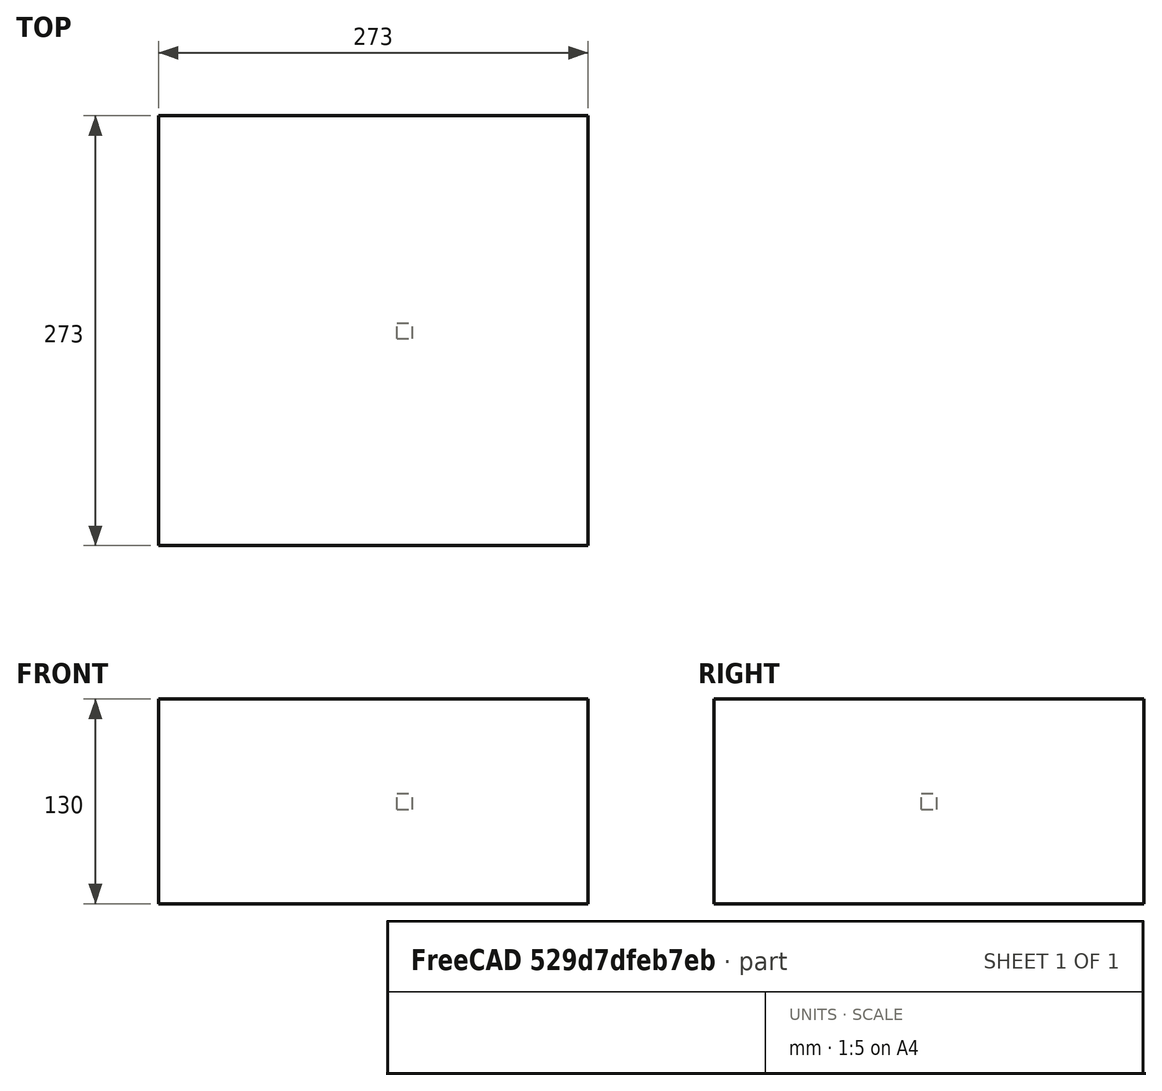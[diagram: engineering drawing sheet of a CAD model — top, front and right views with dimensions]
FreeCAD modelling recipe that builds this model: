
FCSTD DOCUMENT  (FreeCAD 0.20RUnknown)
Label: polarArray-3b
License: All rights reserved
LicenseURL: http://en.wikipedia.org/wiki/All_rights_reserved
objects: App::DocumentObjectGroupPython×1251, Part::FeaturePython×3, App::Part×3
note: 2 computed .brp shape members not serialized (recipe doc carries the construction recipe); baked Part::Feature solids carry a one-line shape summary decoded from their .brp

FEATURE [App::DocumentObjectGroupPython] HALFPI  # scripted group (container) (typed FeaturePython)
  name = HALFPI
  value = pi/2.
FEATURE [App::DocumentObjectGroupPython] PI  # scripted group (container) (typed FeaturePython)
  name = PI
  value = 1.*pi
FEATURE [App::DocumentObjectGroupPython] TWOPI  # scripted group (container) (typed FeaturePython)
  name = TWOPI
  value = 2.*pi
FEATURE [App::DocumentObjectGroupPython] Constants  # scripted group (container) (typed FeaturePython)
  Group = -> [HALFPI,PI,TWOPI]
FEATURE [App::DocumentObjectGroupPython] Variables  # scripted group (container) (typed FeaturePython)
FEATURE [App::DocumentObjectGroupPython] Quantities  # scripted group (container) (typed FeaturePython)
FEATURE [App::DocumentObjectGroupPython] Isotopes  # scripted group (container) (typed FeaturePython)
FEATURE [App::DocumentObjectGroupPython] Elements  # scripted group (container) (typed FeaturePython)
FEATURE [App::DocumentObjectGroupPython] Matrix  # scripted group (container) (typed FeaturePython)
FEATURE [App::DocumentObjectGroupPython] Surfaces  # scripted group (container) (typed FeaturePython)
FEATURE [App::DocumentObjectGroupPython] Opticals  # scripted group (container) (typed FeaturePython)
  Group = -> [Matrix,Surfaces]
FEATURE [App::DocumentObjectGroupPython] G4Isotopes  # scripted group (container) (typed FeaturePython)
FEATURE [App::DocumentObjectGroupPython] H_element  # scripted group (container) (typed FeaturePython)
  Z = 1
  atom_value = 1.008
  formula = H
  name = H_element
FEATURE [App::DocumentObjectGroupPython] He_element  # scripted group (container) (typed FeaturePython)
  Z = 2
  atom_value = 4.0026
  formula = He
  name = He_element
FEATURE [App::DocumentObjectGroupPython] Li_element  # scripted group (container) (typed FeaturePython)
  Z = 3
  atom_value = 6.94
  formula = Li
  name = Li_element
FEATURE [App::DocumentObjectGroupPython] Be_element  # scripted group (container) (typed FeaturePython)
  Z = 4
  atom_value = 9.01218
  formula = Be
  name = Be_element
FEATURE [App::DocumentObjectGroupPython] B_element  # scripted group (container) (typed FeaturePython)
  Z = 5
  atom_value = 10.81
  formula = B
  name = B_element
FEATURE [App::DocumentObjectGroupPython] C_element  # scripted group (container) (typed FeaturePython)
  Z = 6
  atom_value = 12.011
  formula = C
  name = C_element
FEATURE [App::DocumentObjectGroupPython] N_element  # scripted group (container) (typed FeaturePython)
  Z = 7
  atom_value = 14.007
  formula = N
  name = N_element
FEATURE [App::DocumentObjectGroupPython] O_element  # scripted group (container) (typed FeaturePython)
  Z = 8
  atom_value = 15.999
  formula = O
  name = O_element
FEATURE [App::DocumentObjectGroupPython] F_element  # scripted group (container) (typed FeaturePython)
  Z = 9
  atom_value = 18.9984
  formula = F
  name = F_element
FEATURE [App::DocumentObjectGroupPython] Ne_element  # scripted group (container) (typed FeaturePython)
  Z = 10
  atom_value = 20.1797
  formula = Ne
  name = Ne_element
FEATURE [App::DocumentObjectGroupPython] Na_element  # scripted group (container) (typed FeaturePython)
  Z = 11
  atom_value = 22.9898
  formula = Na
  name = Na_element
FEATURE [App::DocumentObjectGroupPython] Mg_element  # scripted group (container) (typed FeaturePython)
  Z = 12
  atom_value = 24.305
  formula = Mg
  name = Mg_element
FEATURE [App::DocumentObjectGroupPython] Al_element  # scripted group (container) (typed FeaturePython)
  Z = 13
  atom_value = 26.9815
  formula = Al
  name = Al_element
FEATURE [App::DocumentObjectGroupPython] Si_element  # scripted group (container) (typed FeaturePython)
  Z = 14
  atom_value = 28.085
  formula = Si
  name = Si_element
FEATURE [App::DocumentObjectGroupPython] P_element  # scripted group (container) (typed FeaturePython)
  Z = 15
  atom_value = 30.9738
  formula = P
  name = P_element
FEATURE [App::DocumentObjectGroupPython] S_element  # scripted group (container) (typed FeaturePython)
  Z = 16
  atom_value = 32.06
  formula = S
  name = S_element
FEATURE [App::DocumentObjectGroupPython] Cl_element  # scripted group (container) (typed FeaturePython)
  Z = 17
  atom_value = 35.45
  formula = Cl
  name = Cl_element
FEATURE [App::DocumentObjectGroupPython] Ar_element  # scripted group (container) (typed FeaturePython)
  Z = 18
  atom_value = 39.95
  formula = Ar
  name = Ar_element
FEATURE [App::DocumentObjectGroupPython] K_element  # scripted group (container) (typed FeaturePython)
  Z = 19
  atom_value = 39.0983
  formula = K
  name = K_element
FEATURE [App::DocumentObjectGroupPython] Ca_element  # scripted group (container) (typed FeaturePython)
  Z = 20
  atom_value = 40.078
  formula = Ca
  name = Ca_element
FEATURE [App::DocumentObjectGroupPython] Sc_element  # scripted group (container) (typed FeaturePython)
  Z = 21
  atom_value = 44.9559
  formula = Sc
  name = Sc_element
FEATURE [App::DocumentObjectGroupPython] Ti_element  # scripted group (container) (typed FeaturePython)
  Z = 22
  atom_value = 47.867
  formula = Ti
  name = Ti_element
FEATURE [App::DocumentObjectGroupPython] V_element  # scripted group (container) (typed FeaturePython)
  Z = 23
  atom_value = 50.9415
  formula = V
  name = V_element
FEATURE [App::DocumentObjectGroupPython] Cr_element  # scripted group (container) (typed FeaturePython)
  Z = 24
  atom_value = 51.9961
  formula = Cr
  name = Cr_element
FEATURE [App::DocumentObjectGroupPython] Mn_element  # scripted group (container) (typed FeaturePython)
  Z = 25
  atom_value = 54.938
  formula = Mn
  name = Mn_element
FEATURE [App::DocumentObjectGroupPython] Fe_element  # scripted group (container) (typed FeaturePython)
  Z = 26
  atom_value = 55.845
  formula = Fe
  name = Fe_element
FEATURE [App::DocumentObjectGroupPython] Co_element  # scripted group (container) (typed FeaturePython)
  Z = 27
  atom_value = 58.9332
  formula = Co
  name = Co_element
FEATURE [App::DocumentObjectGroupPython] Ni_element  # scripted group (container) (typed FeaturePython)
  Z = 28
  atom_value = 58.6934
  formula = Ni
  name = Ni_element
FEATURE [App::DocumentObjectGroupPython] Cu_element  # scripted group (container) (typed FeaturePython)
  Z = 29
  atom_value = 63.546
  formula = Cu
  name = Cu_element
FEATURE [App::DocumentObjectGroupPython] Zn_element  # scripted group (container) (typed FeaturePython)
  Z = 30
  atom_value = 65.38
  formula = Zn
  name = Zn_element
FEATURE [App::DocumentObjectGroupPython] Ga_element  # scripted group (container) (typed FeaturePython)
  Z = 31
  atom_value = 69.723
  formula = Ga
  name = Ga_element
FEATURE [App::DocumentObjectGroupPython] Ge_element  # scripted group (container) (typed FeaturePython)
  Z = 32
  atom_value = 72.63
  formula = Ge
  name = Ge_element
FEATURE [App::DocumentObjectGroupPython] As_element  # scripted group (container) (typed FeaturePython)
  Z = 33
  atom_value = 74.9216
  formula = As
  name = As_element
FEATURE [App::DocumentObjectGroupPython] Se_element  # scripted group (container) (typed FeaturePython)
  Z = 34
  atom_value = 78.971
  formula = Se
  name = Se_element
FEATURE [App::DocumentObjectGroupPython] Br_element  # scripted group (container) (typed FeaturePython)
  Z = 35
  atom_value = 79.904
  formula = Br
  name = Br_element
FEATURE [App::DocumentObjectGroupPython] Kr_element  # scripted group (container) (typed FeaturePython)
  Z = 36
  atom_value = 83.798
  formula = Kr
  name = Kr_element
FEATURE [App::DocumentObjectGroupPython] Rb_element  # scripted group (container) (typed FeaturePython)
  Z = 37
  atom_value = 85.4678
  formula = Rb
  name = Rb_element
FEATURE [App::DocumentObjectGroupPython] Sr_element  # scripted group (container) (typed FeaturePython)
  Z = 38
  atom_value = 87.62
  formula = Sr
  name = Sr_element
FEATURE [App::DocumentObjectGroupPython] Y_element  # scripted group (container) (typed FeaturePython)
  Z = 39
  atom_value = 88.9058
  formula = Y
  name = Y_element
FEATURE [App::DocumentObjectGroupPython] Zr_element  # scripted group (container) (typed FeaturePython)
  Z = 40
  atom_value = 91.224
  formula = Zr
  name = Zr_element
FEATURE [App::DocumentObjectGroupPython] Nb_element  # scripted group (container) (typed FeaturePython)
  Z = 41
  atom_value = 92.9064
  formula = Nb
  name = Nb_element
FEATURE [App::DocumentObjectGroupPython] Mo_element  # scripted group (container) (typed FeaturePython)
  Z = 42
  atom_value = 95.95
  formula = Mo
  name = Mo_element
FEATURE [App::DocumentObjectGroupPython] Tc_element  # scripted group (container) (typed FeaturePython)
  Z = 43
  atom_value = 97
  formula = Tc
  name = Tc_element
FEATURE [App::DocumentObjectGroupPython] Ru_element  # scripted group (container) (typed FeaturePython)
  Z = 44
  atom_value = 101.07
  formula = Ru
  name = Ru_element
FEATURE [App::DocumentObjectGroupPython] Rh_element  # scripted group (container) (typed FeaturePython)
  Z = 45
  atom_value = 102.905
  formula = Rh
  name = Rh_element
FEATURE [App::DocumentObjectGroupPython] Pd_element  # scripted group (container) (typed FeaturePython)
  Z = 46
  atom_value = 106.42
  formula = Pd
  name = Pd_element
FEATURE [App::DocumentObjectGroupPython] Ag_element  # scripted group (container) (typed FeaturePython)
  Z = 47
  atom_value = 107.868
  formula = Ag
  name = Ag_element
FEATURE [App::DocumentObjectGroupPython] Cd_element  # scripted group (container) (typed FeaturePython)
  Z = 48
  atom_value = 112.414
  formula = Cd
  name = Cd_element
FEATURE [App::DocumentObjectGroupPython] In_element  # scripted group (container) (typed FeaturePython)
  Z = 49
  atom_value = 114.818
  formula = In
  name = In_element
FEATURE [App::DocumentObjectGroupPython] Sn_element  # scripted group (container) (typed FeaturePython)
  Z = 50
  atom_value = 118.71
  formula = Sn
  name = Sn_element
FEATURE [App::DocumentObjectGroupPython] Sb_element  # scripted group (container) (typed FeaturePython)
  Z = 51
  atom_value = 121.76
  formula = Sb
  name = Sb_element
FEATURE [App::DocumentObjectGroupPython] Te_element  # scripted group (container) (typed FeaturePython)
  Z = 52
  atom_value = 127.6
  formula = Te
  name = Te_element
FEATURE [App::DocumentObjectGroupPython] I_element  # scripted group (container) (typed FeaturePython)
  Z = 53
  atom_value = 126.904
  formula = I
  name = I_element
FEATURE [App::DocumentObjectGroupPython] Xe_element  # scripted group (container) (typed FeaturePython)
  Z = 54
  atom_value = 131.293
  formula = Xe
  name = Xe_element
FEATURE [App::DocumentObjectGroupPython] Cs_element  # scripted group (container) (typed FeaturePython)
  Z = 55
  atom_value = 132.905
  formula = Cs
  name = Cs_element
FEATURE [App::DocumentObjectGroupPython] Ba_element  # scripted group (container) (typed FeaturePython)
  Z = 56
  atom_value = 137.327
  formula = Ba
  name = Ba_element
FEATURE [App::DocumentObjectGroupPython] La_element  # scripted group (container) (typed FeaturePython)
  Z = 57
  atom_value = 138.905
  formula = La
  name = La_element
FEATURE [App::DocumentObjectGroupPython] Ce_element  # scripted group (container) (typed FeaturePython)
  Z = 58
  atom_value = 140.116
  formula = Ce
  name = Ce_element
FEATURE [App::DocumentObjectGroupPython] Pr_element  # scripted group (container) (typed FeaturePython)
  Z = 59
  atom_value = 140.908
  formula = Pr
  name = Pr_element
FEATURE [App::DocumentObjectGroupPython] Nd_element  # scripted group (container) (typed FeaturePython)
  Z = 60
  atom_value = 144.242
  formula = Nd
  name = Nd_element
FEATURE [App::DocumentObjectGroupPython] Pm_element  # scripted group (container) (typed FeaturePython)
  Z = 61
  atom_value = 145
  formula = Pm
  name = Pm_element
FEATURE [App::DocumentObjectGroupPython] Sm_element  # scripted group (container) (typed FeaturePython)
  Z = 62
  atom_value = 150.36
  formula = Sm
  name = Sm_element
FEATURE [App::DocumentObjectGroupPython] Eu_element  # scripted group (container) (typed FeaturePython)
  Z = 63
  atom_value = 151.964
  formula = Eu
  name = Eu_element
FEATURE [App::DocumentObjectGroupPython] Gd_element  # scripted group (container) (typed FeaturePython)
  Z = 64
  atom_value = 157.25
  formula = Gd
  name = Gd_element
FEATURE [App::DocumentObjectGroupPython] Tb_element  # scripted group (container) (typed FeaturePython)
  Z = 65
  atom_value = 158.925
  formula = Tb
  name = Tb_element
FEATURE [App::DocumentObjectGroupPython] Dy_element  # scripted group (container) (typed FeaturePython)
  Z = 66
  atom_value = 162.5
  formula = Dy
  name = Dy_element
FEATURE [App::DocumentObjectGroupPython] Ho_element  # scripted group (container) (typed FeaturePython)
  Z = 67
  atom_value = 164.93
  formula = Ho
  name = Ho_element
FEATURE [App::DocumentObjectGroupPython] Er_element  # scripted group (container) (typed FeaturePython)
  Z = 68
  atom_value = 167.259
  formula = Er
  name = Er_element
FEATURE [App::DocumentObjectGroupPython] Tm_element  # scripted group (container) (typed FeaturePython)
  Z = 69
  atom_value = 168.934
  formula = Tm
  name = Tm_element
FEATURE [App::DocumentObjectGroupPython] Yb_element  # scripted group (container) (typed FeaturePython)
  Z = 70
  atom_value = 173.045
  formula = Yb
  name = Yb_element
FEATURE [App::DocumentObjectGroupPython] Lu_element  # scripted group (container) (typed FeaturePython)
  Z = 71
  atom_value = 174.967
  formula = Lu
  name = Lu_element
FEATURE [App::DocumentObjectGroupPython] Hf_element  # scripted group (container) (typed FeaturePython)
  Z = 72
  atom_value = 178.49
  formula = Hf
  name = Hf_element
FEATURE [App::DocumentObjectGroupPython] Ta_element  # scripted group (container) (typed FeaturePython)
  Z = 73
  atom_value = 180.948
  formula = Ta
  name = Ta_element
FEATURE [App::DocumentObjectGroupPython] W_element  # scripted group (container) (typed FeaturePython)
  Z = 74
  atom_value = 183.84
  formula = W
  name = W_element
FEATURE [App::DocumentObjectGroupPython] Re_element  # scripted group (container) (typed FeaturePython)
  Z = 75
  atom_value = 186.207
  formula = Re
  name = Re_element
FEATURE [App::DocumentObjectGroupPython] Os_element  # scripted group (container) (typed FeaturePython)
  Z = 76
  atom_value = 190.23
  formula = Os
  name = Os_element
FEATURE [App::DocumentObjectGroupPython] Ir_element  # scripted group (container) (typed FeaturePython)
  Z = 77
  atom_value = 192.217
  formula = Ir
  name = Ir_element
FEATURE [App::DocumentObjectGroupPython] Pt_element  # scripted group (container) (typed FeaturePython)
  Z = 78
  atom_value = 195.084
  formula = Pt
  name = Pt_element
FEATURE [App::DocumentObjectGroupPython] Au_element  # scripted group (container) (typed FeaturePython)
  Z = 79
  atom_value = 196.967
  formula = Au
  name = Au_element
FEATURE [App::DocumentObjectGroupPython] Hg_element  # scripted group (container) (typed FeaturePython)
  Z = 80
  atom_value = 200.592
  formula = Hg
  name = Hg_element
FEATURE [App::DocumentObjectGroupPython] Tl_element  # scripted group (container) (typed FeaturePython)
  Z = 81
  atom_value = 204.38
  formula = Tl
  name = Tl_element
FEATURE [App::DocumentObjectGroupPython] Pb_element  # scripted group (container) (typed FeaturePython)
  Z = 82
  atom_value = 207.2
  formula = Pb
  name = Pb_element
FEATURE [App::DocumentObjectGroupPython] Bi_element  # scripted group (container) (typed FeaturePython)
  Z = 83
  atom_value = 208.98
  formula = Bi
  name = Bi_element
FEATURE [App::DocumentObjectGroupPython] Po_element  # scripted group (container) (typed FeaturePython)
  Z = 84
  atom_value = 209
  formula = Po
  name = Po_element
FEATURE [App::DocumentObjectGroupPython] At_element  # scripted group (container) (typed FeaturePython)
  Z = 85
  atom_value = 210
  formula = At
  name = At_element
FEATURE [App::DocumentObjectGroupPython] Rn_element  # scripted group (container) (typed FeaturePython)
  Z = 86
  atom_value = 222
  formula = Rn
  name = Rn_element
FEATURE [App::DocumentObjectGroupPython] Fr_element  # scripted group (container) (typed FeaturePython)
  Z = 87
  atom_value = 223
  formula = Fr
  name = Fr_element
FEATURE [App::DocumentObjectGroupPython] Ra_element  # scripted group (container) (typed FeaturePython)
  Z = 88
  atom_value = 226
  formula = Ra
  name = Ra_element
FEATURE [App::DocumentObjectGroupPython] Ac_element  # scripted group (container) (typed FeaturePython)
  Z = 89
  atom_value = 227
  formula = Ac
  name = Ac_element
FEATURE [App::DocumentObjectGroupPython] Th_element  # scripted group (container) (typed FeaturePython)
  Z = 90
  atom_value = 232.038
  formula = Th
  name = Th_element
FEATURE [App::DocumentObjectGroupPython] Pa_element  # scripted group (container) (typed FeaturePython)
  Z = 91
  atom_value = 231.036
  formula = Pa
  name = Pa_element
FEATURE [App::DocumentObjectGroupPython] U_element  # scripted group (container) (typed FeaturePython)
  Z = 92
  atom_value = 238.029
  formula = U
  name = U_element
FEATURE [App::DocumentObjectGroupPython] Np_element  # scripted group (container) (typed FeaturePython)
  Z = 93
  atom_value = 237
  formula = Np
  name = Np_element
FEATURE [App::DocumentObjectGroupPython] Pu_element  # scripted group (container) (typed FeaturePython)
  Z = 94
  atom_value = 244
  formula = Pu
  name = Pu_element
FEATURE [App::DocumentObjectGroupPython] Am_element  # scripted group (container) (typed FeaturePython)
  Z = 95
  atom_value = 243
  formula = Am
  name = Am_element
FEATURE [App::DocumentObjectGroupPython] Cm_element  # scripted group (container) (typed FeaturePython)
  Z = 96
  atom_value = 247
  formula = Cm
  name = Cm_element
FEATURE [App::DocumentObjectGroupPython] Bk_element  # scripted group (container) (typed FeaturePython)
  Z = 97
  atom_value = 247
  formula = Bk
  name = Bk_element
FEATURE [App::DocumentObjectGroupPython] Cf_element  # scripted group (container) (typed FeaturePython)
  Z = 98
  atom_value = 251
  formula = Cf
  name = Cf_element
FEATURE [App::DocumentObjectGroupPython] G4Elements  # scripted group (container) (typed FeaturePython)
  Group = -> [H_element,He_element,Li_element,Be_element,B_element,C_element,N_element,O_element,F_element,Ne_element,Na_element,Mg_element,Al_element,Si_element,P_element,S_element,Cl_element,Ar_element,K_element,Ca_element,Sc_element,Ti_element,V_element,Cr_element,Mn_element,Fe_element,Co_element,Ni_element,Cu_element,Zn_element,Ga_element,Ge_element,As_element,Se_element,Br_element,Kr_element,Rb_element,+61 more]
FEATURE [App::DocumentObjectGroupPython] H_element001  label="H_element : 0.101"  # scripted group (container) (typed FeaturePython)
  n = 0.101327
FEATURE [App::DocumentObjectGroupPython] C_element001  label="C_element : 0.775"  # scripted group (container) (typed FeaturePython)
  n = 0.7755
FEATURE [App::DocumentObjectGroupPython] N_element001  label="N_element : 0.035"  # scripted group (container) (typed FeaturePython)
  n = 0.035057
FEATURE [App::DocumentObjectGroupPython] O_element001  label="O_element : 0.052"  # scripted group (container) (typed FeaturePython)
  n = 0.0523159
FEATURE [App::DocumentObjectGroupPython] F_element001  label="F_element : 0.017"  # scripted group (container) (typed FeaturePython)
  n = 0.017422
FEATURE [App::DocumentObjectGroupPython] Ca_element001  label="Ca_element : 0.018"  # scripted group (container) (typed FeaturePython)
  n = 0.018378
FEATURE [App::DocumentObjectGroupPython] G4_A_150_TISSUE  label="G4_A-150_TISSUE"  # scripted group (container) (typed FeaturePython)
  Dunit = g/cm3
  Dvalue = 1.127
  Group = -> [H_element001,C_element001,N_element001,O_element001,F_element001,Ca_element001]
  conduct = 2
  density = 1
  expand = 3
  formula = G4_A-150_TISSUE
  name = G4_A-150_TISSUE
  specific = 4
FEATURE [App::DocumentObjectGroupPython] C_element002  label="C_element : 3"  # scripted group (container) (typed FeaturePython)
  n = 3
  ref = C_element
FEATURE [App::DocumentObjectGroupPython] H_element002  label="H_element : 6"  # scripted group (container) (typed FeaturePython)
  n = 6
  ref = H_element
FEATURE [App::DocumentObjectGroupPython] O_element002  label="O_element : 1"  # scripted group (container) (typed FeaturePython)
  n = 1
  ref = O_element
FEATURE [App::DocumentObjectGroupPython] G4_ACETONE  # scripted group (container) (typed FeaturePython)
  Dunit = g/cm3
  Dvalue = 0.7899
  Group = -> [C_element002,H_element002,O_element002]
  conduct = 2
  density = 1
  expand = 3
  formula = G4_ACETONE
  name = G4_ACETONE
  specific = 4
FEATURE [App::DocumentObjectGroupPython] C_element003  label="C_element : 2"  # scripted group (container) (typed FeaturePython)
  n = 2
  ref = C_element
FEATURE [App::DocumentObjectGroupPython] H_element003  label="H_element : 2"  # scripted group (container) (typed FeaturePython)
  n = 2
  ref = H_element
FEATURE [App::DocumentObjectGroupPython] G4_ACETYLENE  # scripted group (container) (typed FeaturePython)
  Dunit = g/cm3
  Dvalue = 0.0010967
  Group = -> [C_element003,H_element003]
  conduct = 2
  density = 1
  expand = 3
  formula = G4_ACETYLENE
  name = G4_ACETYLENE
  specific = 4
FEATURE [App::DocumentObjectGroupPython] C_element004  label="C_element : 5"  # scripted group (container) (typed FeaturePython)
  n = 5
  ref = C_element
FEATURE [App::DocumentObjectGroupPython] H_element004  label="H_element : 5"  # scripted group (container) (typed FeaturePython)
  n = 5
  ref = H_element
FEATURE [App::DocumentObjectGroupPython] N_element002  label="N_element : 5"  # scripted group (container) (typed FeaturePython)
  n = 5
  ref = N_element
FEATURE [App::DocumentObjectGroupPython] G4_ADENINE  # scripted group (container) (typed FeaturePython)
  Dunit = g/cm3
  Dvalue = 1.6
  Group = -> [C_element004,H_element004,N_element002]
  conduct = 2
  density = 1
  expand = 3
  formula = G4_ADENINE
  name = G4_ADENINE
  specific = 4
FEATURE [App::DocumentObjectGroupPython] H_element005  label="H_element : 0.114"  # scripted group (container) (typed FeaturePython)
  n = 0.114
FEATURE [App::DocumentObjectGroupPython] C_element005  label="C_element : 0.598"  # scripted group (container) (typed FeaturePython)
  n = 0.598
FEATURE [App::DocumentObjectGroupPython] N_element003  label="N_element : 0.007"  # scripted group (container) (typed FeaturePython)
  n = 0.007
FEATURE [App::DocumentObjectGroupPython] O_element003  label="O_element : 0.278"  # scripted group (container) (typed FeaturePython)
  n = 0.278
FEATURE [App::DocumentObjectGroupPython] Na_element001  label="Na_element : 0.001"  # scripted group (container) (typed FeaturePython)
  n = 0.001
FEATURE [App::DocumentObjectGroupPython] S_element001  label="S_element : 0.001"  # scripted group (container) (typed FeaturePython)
  n = 0.001
FEATURE [App::DocumentObjectGroupPython] Cl_element001  label="Cl_element : 0.001"  # scripted group (container) (typed FeaturePython)
  n = 0.001
FEATURE [App::DocumentObjectGroupPython] G4_ADIPOSE_TISSUE_ICRP  # scripted group (container) (typed FeaturePython)
  Dunit = g/cm3
  Dvalue = 0.95
  Group = -> [H_element005,C_element005,N_element003,O_element003,Na_element001,S_element001,Cl_element001]
  conduct = 2
  density = 1
  expand = 3
  formula = G4_ADIPOSE_TISSUE_ICRP
  name = G4_ADIPOSE_TISSUE_ICRP
  specific = 4
FEATURE [App::DocumentObjectGroupPython] C_element006  label="C_element : 0.000"  # scripted group (container) (typed FeaturePython)
  n = 0.000124
FEATURE [App::DocumentObjectGroupPython] N_element004  label="N_element : 0.755"  # scripted group (container) (typed FeaturePython)
  n = 0.755268
FEATURE [App::DocumentObjectGroupPython] O_element004  label="O_element : 0.232"  # scripted group (container) (typed FeaturePython)
  n = 0.231781
FEATURE [App::DocumentObjectGroupPython] Ar_element001  label="Ar_element : 0.013"  # scripted group (container) (typed FeaturePython)
  n = 0.012827
FEATURE [App::DocumentObjectGroupPython] G4_AIR  # scripted group (container) (typed FeaturePython)
  Dunit = g/cm3
  Dvalue = 0.00120479
  Group = -> [C_element006,N_element004,O_element004,Ar_element001]
  conduct = 2
  density = 1
  expand = 3
  formula = G4_AIR
  name = G4_AIR
  specific = 4
FEATURE [App::DocumentObjectGroupPython] C_element007  label="C_element : 006"  # scripted group (container) (typed FeaturePython)
  n = 3
  ref = C_element
FEATURE [App::DocumentObjectGroupPython] H_element006  label="H_element : 7"  # scripted group (container) (typed FeaturePython)
  n = 7
  ref = H_element
FEATURE [App::DocumentObjectGroupPython] N_element005  label="N_element : 1"  # scripted group (container) (typed FeaturePython)
  n = 1
  ref = N_element
FEATURE [App::DocumentObjectGroupPython] O_element005  label="O_element : 2"  # scripted group (container) (typed FeaturePython)
  n = 2
  ref = O_element
FEATURE [App::DocumentObjectGroupPython] G4_ALANINE  # scripted group (container) (typed FeaturePython)
  Dunit = g/cm3
  Dvalue = 1.42
  Group = -> [C_element007,H_element006,N_element005,O_element005]
  conduct = 2
  density = 1
  expand = 3
  formula = G4_ALANINE
  name = G4_ALANINE
  specific = 4
FEATURE [App::DocumentObjectGroupPython] Al_element001  label="Al_element : 2"  # scripted group (container) (typed FeaturePython)
  n = 2
  ref = Al_element
FEATURE [App::DocumentObjectGroupPython] O_element006  label="O_element : 3"  # scripted group (container) (typed FeaturePython)
  n = 3
  ref = O_element
FEATURE [App::DocumentObjectGroupPython] G4_ALUMINUM_OXIDE  # scripted group (container) (typed FeaturePython)
  Dunit = g/cm3
  Dvalue = 3.97
  Group = -> [Al_element001,O_element006]
  conduct = 2
  density = 1
  expand = 3
  formula = G4_ALUMINUM_OXIDE
  name = G4_ALUMINUM_OXIDE
  specific = 4
FEATURE [App::DocumentObjectGroupPython] H_element007  label="H_element : 0.106"  # scripted group (container) (typed FeaturePython)
  n = 0.10593
FEATURE [App::DocumentObjectGroupPython] C_element008  label="C_element : 0.789"  # scripted group (container) (typed FeaturePython)
  n = 0.788974
FEATURE [App::DocumentObjectGroupPython] O_element007  label="O_element : 0.105"  # scripted group (container) (typed FeaturePython)
  n = 0.105096
FEATURE [App::DocumentObjectGroupPython] G4_AMBER  # scripted group (container) (typed FeaturePython)
  Dunit = g/cm3
  Dvalue = 1.1
  Group = -> [H_element007,C_element008,O_element007]
  conduct = 2
  density = 1
  expand = 3
  formula = G4_AMBER
  name = G4_AMBER
  specific = 4
FEATURE [App::DocumentObjectGroupPython] N_element006  label="N_element : 006"  # scripted group (container) (typed FeaturePython)
  n = 1
  ref = N_element
FEATURE [App::DocumentObjectGroupPython] H_element008  label="H_element : 3"  # scripted group (container) (typed FeaturePython)
  n = 3
  ref = H_element
FEATURE [App::DocumentObjectGroupPython] G4_AMMONIA  # scripted group (container) (typed FeaturePython)
  Dunit = g/cm3
  Dvalue = 0.000826019
  Group = -> [N_element006,H_element008]
  conduct = 2
  density = 1
  expand = 3
  formula = G4_AMMONIA
  name = G4_AMMONIA
  specific = 4
FEATURE [App::DocumentObjectGroupPython] C_element009  label="C_element : 6"  # scripted group (container) (typed FeaturePython)
  n = 6
  ref = C_element
FEATURE [App::DocumentObjectGroupPython] H_element009  label="H_element : 008"  # scripted group (container) (typed FeaturePython)
  n = 7
  ref = H_element
FEATURE [App::DocumentObjectGroupPython] N_element007  label="N_element : 007"  # scripted group (container) (typed FeaturePython)
  n = 1
  ref = N_element
FEATURE [App::DocumentObjectGroupPython] G4_ANILINE  # scripted group (container) (typed FeaturePython)
  Dunit = g/cm3
  Dvalue = 1.0235
  Group = -> [C_element009,H_element009,N_element007]
  conduct = 2
  density = 1
  expand = 3
  formula = G4_ANILINE
  name = G4_ANILINE
  specific = 4
FEATURE [App::DocumentObjectGroupPython] C_element010  label="C_element : 14"  # scripted group (container) (typed FeaturePython)
  n = 14
  ref = C_element
FEATURE [App::DocumentObjectGroupPython] H_element010  label="H_element : 10"  # scripted group (container) (typed FeaturePython)
  n = 10
  ref = H_element
FEATURE [App::DocumentObjectGroupPython] G4_ANTHRACENE  # scripted group (container) (typed FeaturePython)
  Dunit = g/cm3
  Dvalue = 1.283
  Group = -> [C_element010,H_element010]
  conduct = 2
  density = 1
  expand = 3
  formula = G4_ANTHRACENE
  name = G4_ANTHRACENE
  specific = 4
FEATURE [App::DocumentObjectGroupPython] H_element011  label="H_element : 0.065"  # scripted group (container) (typed FeaturePython)
  n = 0.0654709
FEATURE [App::DocumentObjectGroupPython] C_element011  label="C_element : 0.537"  # scripted group (container) (typed FeaturePython)
  n = 0.536944
FEATURE [App::DocumentObjectGroupPython] N_element008  label="N_element : 0.021"  # scripted group (container) (typed FeaturePython)
  n = 0.0215
FEATURE [App::DocumentObjectGroupPython] O_element008  label="O_element : 0.032"  # scripted group (container) (typed FeaturePython)
  n = 0.032085
FEATURE [App::DocumentObjectGroupPython] F_element002  label="F_element : 0.167"  # scripted group (container) (typed FeaturePython)
  n = 0.167411
FEATURE [App::DocumentObjectGroupPython] Ca_element002  label="Ca_element : 0.177"  # scripted group (container) (typed FeaturePython)
  n = 0.176589
FEATURE [App::DocumentObjectGroupPython] G4_B_100_BONE  label="G4_B-100_BONE"  # scripted group (container) (typed FeaturePython)
  Dunit = g/cm3
  Dvalue = 1.45
  Group = -> [H_element011,C_element011,N_element008,O_element008,F_element002,Ca_element002]
  conduct = 2
  density = 1
  expand = 3
  formula = G4_B-100_BONE
  name = G4_B-100_BONE
  specific = 4
FEATURE [App::DocumentObjectGroupPython] H_element012  label="H_element : 0.057"  # scripted group (container) (typed FeaturePython)
  n = 0.057441
FEATURE [App::DocumentObjectGroupPython] C_element012  label="C_element : 0.790"  # scripted group (container) (typed FeaturePython)
  n = 0.774591
FEATURE [App::DocumentObjectGroupPython] O_element009  label="O_element : 0.168"  # scripted group (container) (typed FeaturePython)
  n = 0.167968
FEATURE [App::DocumentObjectGroupPython] G4_BAKELITE  # scripted group (container) (typed FeaturePython)
  Dunit = g/cm3
  Dvalue = 1.25
  Group = -> [H_element012,C_element012,O_element009]
  conduct = 2
  density = 1
  expand = 3
  formula = G4_BAKELITE
  name = G4_BAKELITE
  specific = 4
FEATURE [App::DocumentObjectGroupPython] Ba_element001  label="Ba_element : 1"  # scripted group (container) (typed FeaturePython)
  n = 1
  ref = Ba_element
FEATURE [App::DocumentObjectGroupPython] F_element003  label="F_element : 2"  # scripted group (container) (typed FeaturePython)
  n = 2
  ref = F_element
FEATURE [App::DocumentObjectGroupPython] G4_BARIUM_FLUORIDE  # scripted group (container) (typed FeaturePython)
  Dunit = g/cm3
  Dvalue = 4.89
  Group = -> [Ba_element001,F_element003]
  conduct = 2
  density = 1
  expand = 3
  formula = G4_BARIUM_FLUORIDE
  name = G4_BARIUM_FLUORIDE
  specific = 4
FEATURE [App::DocumentObjectGroupPython] Ba_element002  label="Ba_element : 002"  # scripted group (container) (typed FeaturePython)
  n = 1
  ref = Ba_element
FEATURE [App::DocumentObjectGroupPython] S_element002  label="S_element : 1"  # scripted group (container) (typed FeaturePython)
  n = 1
  ref = S_element
FEATURE [App::DocumentObjectGroupPython] O_element010  label="O_element : 4"  # scripted group (container) (typed FeaturePython)
  n = 4
  ref = O_element
FEATURE [App::DocumentObjectGroupPython] G4_BARIUM_SULFATE  # scripted group (container) (typed FeaturePython)
  Dunit = g/cm3
  Dvalue = 4.5
  Group = -> [Ba_element002,S_element002,O_element010]
  conduct = 2
  density = 1
  expand = 3
  formula = G4_BARIUM_SULFATE
  name = G4_BARIUM_SULFATE
  specific = 4
FEATURE [App::DocumentObjectGroupPython] C_element013  label="C_element : 007"  # scripted group (container) (typed FeaturePython)
  n = 6
  ref = C_element
FEATURE [App::DocumentObjectGroupPython] H_element013  label="H_element : 009"  # scripted group (container) (typed FeaturePython)
  n = 6
  ref = H_element
FEATURE [App::DocumentObjectGroupPython] G4_BENZENE  # scripted group (container) (typed FeaturePython)
  Dunit = g/cm3
  Dvalue = 0.87865
  Group = -> [C_element013,H_element013]
  conduct = 2
  density = 1
  expand = 3
  formula = G4_BENZENE
  name = G4_BENZENE
  specific = 4
FEATURE [App::DocumentObjectGroupPython] Be_element001  label="Be_element : 1"  # scripted group (container) (typed FeaturePython)
  n = 1
  ref = Be_element
FEATURE [App::DocumentObjectGroupPython] O_element011  label="O_element : 005"  # scripted group (container) (typed FeaturePython)
  n = 1
  ref = O_element
FEATURE [App::DocumentObjectGroupPython] G4_BERYLLIUM_OXIDE  # scripted group (container) (typed FeaturePython)
  Dunit = g/cm3
  Dvalue = 3.01
  Group = -> [Be_element001,O_element011]
  conduct = 2
  density = 1
  expand = 3
  formula = G4_BERYLLIUM_OXIDE
  name = G4_BERYLLIUM_OXIDE
  specific = 4
FEATURE [App::DocumentObjectGroupPython] Bi_element001  label="Bi_element : 4"  # scripted group (container) (typed FeaturePython)
  n = 4
  ref = Bi_element
FEATURE [App::DocumentObjectGroupPython] Ge_element001  label="Ge_element : 3"  # scripted group (container) (typed FeaturePython)
  n = 3
  ref = Ge_element
FEATURE [App::DocumentObjectGroupPython] O_element012  label="O_element : 12"  # scripted group (container) (typed FeaturePython)
  n = 12
  ref = O_element
FEATURE [App::DocumentObjectGroupPython] G4_BGO  # scripted group (container) (typed FeaturePython)
  Dunit = g/cm3
  Dvalue = 7.13
  Group = -> [Bi_element001,Ge_element001,O_element012]
  conduct = 2
  density = 1
  expand = 3
  formula = G4_BGO
  name = G4_BGO
  specific = 4
FEATURE [App::DocumentObjectGroupPython] H_element014  label="H_element : 0.102"  # scripted group (container) (typed FeaturePython)
  n = 0.102
FEATURE [App::DocumentObjectGroupPython] C_element014  label="C_element : 0.110"  # scripted group (container) (typed FeaturePython)
  n = 0.11
FEATURE [App::DocumentObjectGroupPython] N_element009  label="N_element : 0.033"  # scripted group (container) (typed FeaturePython)
  n = 0.033
FEATURE [App::DocumentObjectGroupPython] O_element013  label="O_element : 0.745"  # scripted group (container) (typed FeaturePython)
  n = 0.745
FEATURE [App::DocumentObjectGroupPython] Na_element002  label="Na_element : 0.002"  # scripted group (container) (typed FeaturePython)
  n = 0.001
FEATURE [App::DocumentObjectGroupPython] P_element001  label="P_element : 0.001"  # scripted group (container) (typed FeaturePython)
  n = 0.001
FEATURE [App::DocumentObjectGroupPython] S_element003  label="S_element : 0.002"  # scripted group (container) (typed FeaturePython)
  n = 0.002
FEATURE [App::DocumentObjectGroupPython] Cl_element002  label="Cl_element : 0.003"  # scripted group (container) (typed FeaturePython)
  n = 0.003
FEATURE [App::DocumentObjectGroupPython] K_element001  label="K_element : 0.002"  # scripted group (container) (typed FeaturePython)
  n = 0.002
FEATURE [App::DocumentObjectGroupPython] Fe_element001  label="Fe_element : 0.001"  # scripted group (container) (typed FeaturePython)
  n = 0.001
FEATURE [App::DocumentObjectGroupPython] G4_BLOOD_ICRP  # scripted group (container) (typed FeaturePython)
  Dunit = g/cm3
  Dvalue = 1.06
  Group = -> [H_element014,C_element014,N_element009,O_element013,Na_element002,P_element001,S_element003,Cl_element002,K_element001,Fe_element001]
  conduct = 2
  density = 1
  expand = 3
  formula = G4_BLOOD_ICRP
  name = G4_BLOOD_ICRP
  specific = 4
FEATURE [App::DocumentObjectGroupPython] H_element015  label="H_element : 0.064"  # scripted group (container) (typed FeaturePython)
  n = 0.064
FEATURE [App::DocumentObjectGroupPython] C_element015  label="C_element : 0.278"  # scripted group (container) (typed FeaturePython)
  n = 0.278
FEATURE [App::DocumentObjectGroupPython] N_element010  label="N_element : 0.027"  # scripted group (container) (typed FeaturePython)
  n = 0.027
FEATURE [App::DocumentObjectGroupPython] O_element014  label="O_element : 0.410"  # scripted group (container) (typed FeaturePython)
  n = 0.41
FEATURE [App::DocumentObjectGroupPython] Mg_element001  label="Mg_element : 0.002"  # scripted group (container) (typed FeaturePython)
  n = 0.002
FEATURE [App::DocumentObjectGroupPython] P_element002  label="P_element : 0.070"  # scripted group (container) (typed FeaturePython)
  n = 0.07
FEATURE [App::DocumentObjectGroupPython] S_element004  label="S_element : 0.003"  # scripted group (container) (typed FeaturePython)
  n = 0.002
FEATURE [App::DocumentObjectGroupPython] Ca_element003  label="Ca_element : 0.147"  # scripted group (container) (typed FeaturePython)
  n = 0.147
FEATURE [App::DocumentObjectGroupPython] G4_BONE_COMPACT_ICRU  # scripted group (container) (typed FeaturePython)
  Dunit = g/cm3
  Dvalue = 1.85
  Group = -> [H_element015,C_element015,N_element010,O_element014,Mg_element001,P_element002,S_element004,Ca_element003]
  conduct = 2
  density = 1
  expand = 3
  formula = G4_BONE_COMPACT_ICRU
  name = G4_BONE_COMPACT_ICRU
  specific = 4
FEATURE [App::DocumentObjectGroupPython] H_element016  label="H_element : 0.034"  # scripted group (container) (typed FeaturePython)
  n = 0.034
FEATURE [App::DocumentObjectGroupPython] C_element016  label="C_element : 0.155"  # scripted group (container) (typed FeaturePython)
  n = 0.155
FEATURE [App::DocumentObjectGroupPython] N_element011  label="N_element : 0.042"  # scripted group (container) (typed FeaturePython)
  n = 0.042
FEATURE [App::DocumentObjectGroupPython] O_element015  label="O_element : 0.435"  # scripted group (container) (typed FeaturePython)
  n = 0.435
FEATURE [App::DocumentObjectGroupPython] Na_element003  label="Na_element : 0.003"  # scripted group (container) (typed FeaturePython)
  n = 0.001
FEATURE [App::DocumentObjectGroupPython] Mg_element002  label="Mg_element : 0.003"  # scripted group (container) (typed FeaturePython)
  n = 0.002
FEATURE [App::DocumentObjectGroupPython] P_element003  label="P_element : 0.103"  # scripted group (container) (typed FeaturePython)
  n = 0.103
FEATURE [App::DocumentObjectGroupPython] S_element005  label="S_element : 0.004"  # scripted group (container) (typed FeaturePython)
  n = 0.003
FEATURE [App::DocumentObjectGroupPython] Ca_element004  label="Ca_element : 0.225"  # scripted group (container) (typed FeaturePython)
  n = 0.225
FEATURE [App::DocumentObjectGroupPython] G4_BONE_CORTICAL_ICRP  # scripted group (container) (typed FeaturePython)
  Dunit = g/cm3
  Dvalue = 1.92
  Group = -> [H_element016,C_element016,N_element011,O_element015,Na_element003,Mg_element002,P_element003,S_element005,Ca_element004]
  conduct = 2
  density = 1
  expand = 3
  formula = G4_BONE_CORTICAL_ICRP
  name = G4_BONE_CORTICAL_ICRP
  specific = 4
FEATURE [App::DocumentObjectGroupPython] B_element001  label="B_element : 4"  # scripted group (container) (typed FeaturePython)
  n = 4
  ref = B_element
FEATURE [App::DocumentObjectGroupPython] C_element017  label="C_element : 1"  # scripted group (container) (typed FeaturePython)
  n = 1
  ref = C_element
FEATURE [App::DocumentObjectGroupPython] G4_BORON_CARBIDE  # scripted group (container) (typed FeaturePython)
  Dunit = g/cm3
  Dvalue = 2.52
  Group = -> [B_element001,C_element017]
  conduct = 2
  density = 1
  expand = 3
  formula = G4_BORON_CARBIDE
  name = G4_BORON_CARBIDE
  specific = 4
FEATURE [App::DocumentObjectGroupPython] B_element002  label="B_element : 2"  # scripted group (container) (typed FeaturePython)
  n = 2
  ref = B_element
FEATURE [App::DocumentObjectGroupPython] O_element016  label="O_element : 006"  # scripted group (container) (typed FeaturePython)
  n = 3
  ref = O_element
FEATURE [App::DocumentObjectGroupPython] G4_BORON_OXIDE  # scripted group (container) (typed FeaturePython)
  Dunit = g/cm3
  Dvalue = 1.812
  Group = -> [B_element002,O_element016]
  conduct = 2
  density = 1
  expand = 3
  formula = G4_BORON_OXIDE
  name = G4_BORON_OXIDE
  specific = 4
FEATURE [App::DocumentObjectGroupPython] H_element017  label="H_element : 0.107"  # scripted group (container) (typed FeaturePython)
  n = 0.107
FEATURE [App::DocumentObjectGroupPython] C_element018  label="C_element : 0.145"  # scripted group (container) (typed FeaturePython)
  n = 0.145
FEATURE [App::DocumentObjectGroupPython] N_element012  label="N_element : 0.022"  # scripted group (container) (typed FeaturePython)
  n = 0.022
FEATURE [App::DocumentObjectGroupPython] O_element017  label="O_element : 0.712"  # scripted group (container) (typed FeaturePython)
  n = 0.712
FEATURE [App::DocumentObjectGroupPython] Na_element004  label="Na_element : 0.004"  # scripted group (container) (typed FeaturePython)
  n = 0.002
FEATURE [App::DocumentObjectGroupPython] P_element004  label="P_element : 0.004"  # scripted group (container) (typed FeaturePython)
  n = 0.004
FEATURE [App::DocumentObjectGroupPython] S_element006  label="S_element : 0.005"  # scripted group (container) (typed FeaturePython)
  n = 0.002
FEATURE [App::DocumentObjectGroupPython] Cl_element003  label="Cl_element : 0.004"  # scripted group (container) (typed FeaturePython)
  n = 0.003
FEATURE [App::DocumentObjectGroupPython] K_element002  label="K_element : 0.003"  # scripted group (container) (typed FeaturePython)
  n = 0.003
FEATURE [App::DocumentObjectGroupPython] G4_BRAIN_ICRP  # scripted group (container) (typed FeaturePython)
  Dunit = g/cm3
  Dvalue = 1.04
  Group = -> [H_element017,C_element018,N_element012,O_element017,Na_element004,P_element004,S_element006,Cl_element003,K_element002]
  conduct = 2
  density = 1
  expand = 3
  formula = G4_BRAIN_ICRP
  name = G4_BRAIN_ICRP
  specific = 4
FEATURE [App::DocumentObjectGroupPython] C_element019  label="C_element : 4"  # scripted group (container) (typed FeaturePython)
  n = 4
  ref = C_element
FEATURE [App::DocumentObjectGroupPython] H_element018  label="H_element : 010"  # scripted group (container) (typed FeaturePython)
  n = 10
  ref = H_element
FEATURE [App::DocumentObjectGroupPython] G4_BUTANE  # scripted group (container) (typed FeaturePython)
  Dunit = g/cm3
  Dvalue = 0.00249343
  Group = -> [C_element019,H_element018]
  conduct = 2
  density = 1
  expand = 3
  formula = G4_BUTANE
  name = G4_BUTANE
  specific = 4
FEATURE [App::DocumentObjectGroupPython] C_element020  label="C_element : 008"  # scripted group (container) (typed FeaturePython)
  n = 4
  ref = C_element
FEATURE [App::DocumentObjectGroupPython] H_element019  label="H_element : 011"  # scripted group (container) (typed FeaturePython)
  n = 10
  ref = H_element
FEATURE [App::DocumentObjectGroupPython] O_element018  label="O_element : 007"  # scripted group (container) (typed FeaturePython)
  n = 1
  ref = O_element
FEATURE [App::DocumentObjectGroupPython] G4_N_BUTYL_ALCOHOL  label="G4_N-BUTYL_ALCOHOL"  # scripted group (container) (typed FeaturePython)
  Dunit = g/cm3
  Dvalue = 0.8098
  Group = -> [C_element020,H_element019,O_element018]
  conduct = 2
  density = 1
  expand = 3
  formula = G4_N-BUTYL_ALCOHOL
  name = G4_N-BUTYL_ALCOHOL
  specific = 4
FEATURE [App::DocumentObjectGroupPython] H_element020  label="H_element : 0.025"  # scripted group (container) (typed FeaturePython)
  n = 0.02468
FEATURE [App::DocumentObjectGroupPython] C_element021  label="C_element : 0.502"  # scripted group (container) (typed FeaturePython)
  n = 0.501611
FEATURE [App::DocumentObjectGroupPython] O_element019  label="O_element : 0.005"  # scripted group (container) (typed FeaturePython)
  n = 0.004527
FEATURE [App::DocumentObjectGroupPython] F_element004  label="F_element : 0.465"  # scripted group (container) (typed FeaturePython)
  n = 0.465209
FEATURE [App::DocumentObjectGroupPython] Si_element001  label="Si_element : 0.004"  # scripted group (container) (typed FeaturePython)
  n = 0.003973
FEATURE [App::DocumentObjectGroupPython] G4_C_552  label="G4_C-552"  # scripted group (container) (typed FeaturePython)
  Dunit = g/cm3
  Dvalue = 1.76
  Group = -> [H_element020,C_element021,O_element019,F_element004,Si_element001]
  conduct = 2
  density = 1
  expand = 3
  formula = G4_C-552
  name = G4_C-552
  specific = 4
FEATURE [App::DocumentObjectGroupPython] Cd_element001  label="Cd_element : 1"  # scripted group (container) (typed FeaturePython)
  n = 1
  ref = Cd_element
FEATURE [App::DocumentObjectGroupPython] Te_element001  label="Te_element : 1"  # scripted group (container) (typed FeaturePython)
  n = 1
  ref = Te_element
FEATURE [App::DocumentObjectGroupPython] G4_CADMIUM_TELLURIDE  # scripted group (container) (typed FeaturePython)
  Dunit = g/cm3
  Dvalue = 6.2
  Group = -> [Cd_element001,Te_element001]
  conduct = 2
  density = 1
  expand = 3
  formula = G4_CADMIUM_TELLURIDE
  name = G4_CADMIUM_TELLURIDE
  specific = 4
FEATURE [App::DocumentObjectGroupPython] Cd_element002  label="Cd_element : 002"  # scripted group (container) (typed FeaturePython)
  n = 1
  ref = Cd_element
FEATURE [App::DocumentObjectGroupPython] W_element001  label="W_element : 1"  # scripted group (container) (typed FeaturePython)
  n = 1
  ref = W_element
FEATURE [App::DocumentObjectGroupPython] O_element020  label="O_element : 008"  # scripted group (container) (typed FeaturePython)
  n = 4
  ref = O_element
FEATURE [App::DocumentObjectGroupPython] G4_CADMIUM_TUNGSTATE  # scripted group (container) (typed FeaturePython)
  Dunit = g/cm3
  Dvalue = 7.9
  Group = -> [Cd_element002,W_element001,O_element020]
  conduct = 2
  density = 1
  expand = 3
  formula = G4_CADMIUM_TUNGSTATE
  name = G4_CADMIUM_TUNGSTATE
  specific = 4
FEATURE [App::DocumentObjectGroupPython] Ca_element005  label="Ca_element : 1"  # scripted group (container) (typed FeaturePython)
  n = 1
  ref = Ca_element
FEATURE [App::DocumentObjectGroupPython] C_element022  label="C_element : 009"  # scripted group (container) (typed FeaturePython)
  n = 1
  ref = C_element
FEATURE [App::DocumentObjectGroupPython] O_element021  label="O_element : 009"  # scripted group (container) (typed FeaturePython)
  n = 3
  ref = O_element
FEATURE [App::DocumentObjectGroupPython] G4_CALCIUM_CARBONATE  # scripted group (container) (typed FeaturePython)
  Dunit = g/cm3
  Dvalue = 2.8
  Group = -> [Ca_element005,C_element022,O_element021]
  conduct = 2
  density = 1
  expand = 3
  formula = G4_CALCIUM_CARBONATE
  name = G4_CALCIUM_CARBONATE
  specific = 4
FEATURE [App::DocumentObjectGroupPython] Ca_element006  label="Ca_element : 002"  # scripted group (container) (typed FeaturePython)
  n = 1
  ref = Ca_element
FEATURE [App::DocumentObjectGroupPython] F_element005  label="F_element : 003"  # scripted group (container) (typed FeaturePython)
  n = 2
  ref = F_element
FEATURE [App::DocumentObjectGroupPython] G4_CALCIUM_FLUORIDE  # scripted group (container) (typed FeaturePython)
  Dunit = g/cm3
  Dvalue = 3.18
  Group = -> [Ca_element006,F_element005]
  conduct = 2
  density = 1
  expand = 3
  formula = G4_CALCIUM_FLUORIDE
  name = G4_CALCIUM_FLUORIDE
  specific = 4
FEATURE [App::DocumentObjectGroupPython] Ca_element007  label="Ca_element : 003"  # scripted group (container) (typed FeaturePython)
  n = 1
  ref = Ca_element
FEATURE [App::DocumentObjectGroupPython] O_element022  label="O_element : 010"  # scripted group (container) (typed FeaturePython)
  n = 1
  ref = O_element
FEATURE [App::DocumentObjectGroupPython] G4_CALCIUM_OXIDE  # scripted group (container) (typed FeaturePython)
  Dunit = g/cm3
  Dvalue = 3.3
  Group = -> [Ca_element007,O_element022]
  conduct = 2
  density = 1
  expand = 3
  formula = G4_CALCIUM_OXIDE
  name = G4_CALCIUM_OXIDE
  specific = 4
FEATURE [App::DocumentObjectGroupPython] Ca_element008  label="Ca_element : 004"  # scripted group (container) (typed FeaturePython)
  n = 1
  ref = Ca_element
FEATURE [App::DocumentObjectGroupPython] S_element007  label="S_element : 002"  # scripted group (container) (typed FeaturePython)
  n = 1
  ref = S_element
FEATURE [App::DocumentObjectGroupPython] O_element023  label="O_element : 011"  # scripted group (container) (typed FeaturePython)
  n = 4
  ref = O_element
FEATURE [App::DocumentObjectGroupPython] G4_CALCIUM_SULFATE  # scripted group (container) (typed FeaturePython)
  Dunit = g/cm3
  Dvalue = 2.96
  Group = -> [Ca_element008,S_element007,O_element023]
  conduct = 2
  density = 1
  expand = 3
  formula = G4_CALCIUM_SULFATE
  name = G4_CALCIUM_SULFATE
  specific = 4
FEATURE [App::DocumentObjectGroupPython] Ca_element009  label="Ca_element : 005"  # scripted group (container) (typed FeaturePython)
  n = 1
  ref = Ca_element
FEATURE [App::DocumentObjectGroupPython] W_element002  label="W_element : 002"  # scripted group (container) (typed FeaturePython)
  n = 1
  ref = W_element
FEATURE [App::DocumentObjectGroupPython] O_element024  label="O_element : 012"  # scripted group (container) (typed FeaturePython)
  n = 4
  ref = O_element
FEATURE [App::DocumentObjectGroupPython] G4_CALCIUM_TUNGSTATE  # scripted group (container) (typed FeaturePython)
  Dunit = g/cm3
  Dvalue = 6.062
  Group = -> [Ca_element009,W_element002,O_element024]
  conduct = 2
  density = 1
  expand = 3
  formula = G4_CALCIUM_TUNGSTATE
  name = G4_CALCIUM_TUNGSTATE
  specific = 4
FEATURE [App::DocumentObjectGroupPython] C_element023  label="C_element : 010"  # scripted group (container) (typed FeaturePython)
  n = 1
  ref = C_element
FEATURE [App::DocumentObjectGroupPython] O_element025  label="O_element : 013"  # scripted group (container) (typed FeaturePython)
  n = 2
  ref = O_element
FEATURE [App::DocumentObjectGroupPython] G4_CARBON_DIOXIDE  # scripted group (container) (typed FeaturePython)
  Dunit = g/cm3
  Dvalue = 0.00184212
  Group = -> [C_element023,O_element025]
  conduct = 2
  density = 1
  expand = 3
  formula = G4_CARBON_DIOXIDE
  name = G4_CARBON_DIOXIDE
  specific = 4
FEATURE [App::DocumentObjectGroupPython] C_element024  label="C_element : 011"  # scripted group (container) (typed FeaturePython)
  n = 1
  ref = C_element
FEATURE [App::DocumentObjectGroupPython] Cl_element004  label="Cl_element : 4"  # scripted group (container) (typed FeaturePython)
  n = 4
  ref = Cl_element
FEATURE [App::DocumentObjectGroupPython] G4_CARBON_TETRACHLORIDE  # scripted group (container) (typed FeaturePython)
  Dunit = g/cm3
  Dvalue = 1.594
  Group = -> [C_element024,Cl_element004]
  conduct = 2
  density = 1
  expand = 3
  formula = G4_CARBON_TETRACHLORIDE
  name = G4_CARBON_TETRACHLORIDE
  specific = 4
FEATURE [App::DocumentObjectGroupPython] C_element025  label="C_element : 012"  # scripted group (container) (typed FeaturePython)
  n = 6
  ref = C_element
FEATURE [App::DocumentObjectGroupPython] H_element021  label="H_element : 012"  # scripted group (container) (typed FeaturePython)
  n = 10
  ref = H_element
FEATURE [App::DocumentObjectGroupPython] O_element026  label="O_element : 5"  # scripted group (container) (typed FeaturePython)
  n = 5
  ref = O_element
FEATURE [App::DocumentObjectGroupPython] G4_CELLULOSE_CELLOPHANE  # scripted group (container) (typed FeaturePython)
  Dunit = g/cm3
  Dvalue = 1.42
  Group = -> [C_element025,H_element021,O_element026]
  conduct = 2
  density = 1
  expand = 3
  formula = G4_CELLULOSE_CELLOPHANE
  name = G4_CELLULOSE_CELLOPHANE
  specific = 4
FEATURE [App::DocumentObjectGroupPython] H_element022  label="H_element : 0.067"  # scripted group (container) (typed FeaturePython)
  n = 0.067125
FEATURE [App::DocumentObjectGroupPython] C_element026  label="C_element : 0.545"  # scripted group (container) (typed FeaturePython)
  n = 0.545403
FEATURE [App::DocumentObjectGroupPython] O_element027  label="O_element : 0.387"  # scripted group (container) (typed FeaturePython)
  n = 0.387472
FEATURE [App::DocumentObjectGroupPython] G4_CELLULOSE_BUTYRATE  # scripted group (container) (typed FeaturePython)
  Dunit = g/cm3
  Dvalue = 1.2
  Group = -> [H_element022,C_element026,O_element027]
  conduct = 2
  density = 1
  expand = 3
  formula = G4_CELLULOSE_BUTYRATE
  name = G4_CELLULOSE_BUTYRATE
  specific = 4
FEATURE [App::DocumentObjectGroupPython] H_element023  label="H_element : 0.029"  # scripted group (container) (typed FeaturePython)
  n = 0.029216
FEATURE [App::DocumentObjectGroupPython] C_element027  label="C_element : 0.271"  # scripted group (container) (typed FeaturePython)
  n = 0.271296
FEATURE [App::DocumentObjectGroupPython] N_element013  label="N_element : 0.121"  # scripted group (container) (typed FeaturePython)
  n = 0.121276
FEATURE [App::DocumentObjectGroupPython] O_element028  label="O_element : 0.578"  # scripted group (container) (typed FeaturePython)
  n = 0.578212
FEATURE [App::DocumentObjectGroupPython] G4_CELLULOSE_NITRATE  # scripted group (container) (typed FeaturePython)
  Dunit = g/cm3
  Dvalue = 1.49
  Group = -> [H_element023,C_element027,N_element013,O_element028]
  conduct = 2
  density = 1
  expand = 3
  formula = G4_CELLULOSE_NITRATE
  name = G4_CELLULOSE_NITRATE
  specific = 4
FEATURE [App::DocumentObjectGroupPython] H_element024  label="H_element : 0.108"  # scripted group (container) (typed FeaturePython)
  n = 0.107596
FEATURE [App::DocumentObjectGroupPython] N_element014  label="N_element : 0.001"  # scripted group (container) (typed FeaturePython)
  n = 0.0008
FEATURE [App::DocumentObjectGroupPython] O_element029  label="O_element : 0.875"  # scripted group (container) (typed FeaturePython)
  n = 0.874976
FEATURE [App::DocumentObjectGroupPython] S_element008  label="S_element : 0.015"  # scripted group (container) (typed FeaturePython)
  n = 0.014627
FEATURE [App::DocumentObjectGroupPython] Ce_element001  label="Ce_element : 0.002"  # scripted group (container) (typed FeaturePython)
  n = 0.002001
FEATURE [App::DocumentObjectGroupPython] G4_CERIC_SULFATE  # scripted group (container) (typed FeaturePython)
  Dunit = g/cm3
  Dvalue = 1.03
  Group = -> [H_element024,N_element014,O_element029,S_element008,Ce_element001]
  conduct = 2
  density = 1
  expand = 3
  formula = G4_CERIC_SULFATE
  name = G4_CERIC_SULFATE
  specific = 4
FEATURE [App::DocumentObjectGroupPython] Cs_element001  label="Cs_element : 1"  # scripted group (container) (typed FeaturePython)
  n = 1
  ref = Cs_element
FEATURE [App::DocumentObjectGroupPython] F_element006  label="F_element : 1"  # scripted group (container) (typed FeaturePython)
  n = 1
  ref = F_element
FEATURE [App::DocumentObjectGroupPython] G4_CESIUM_FLUORIDE  # scripted group (container) (typed FeaturePython)
  Dunit = g/cm3
  Dvalue = 4.115
  Group = -> [Cs_element001,F_element006]
  conduct = 2
  density = 1
  expand = 3
  formula = G4_CESIUM_FLUORIDE
  name = G4_CESIUM_FLUORIDE
  specific = 4
FEATURE [App::DocumentObjectGroupPython] Cs_element002  label="Cs_element : 002"  # scripted group (container) (typed FeaturePython)
  n = 1
  ref = Cs_element
FEATURE [App::DocumentObjectGroupPython] I_element001  label="I_element : 1"  # scripted group (container) (typed FeaturePython)
  n = 1
  ref = I_element
FEATURE [App::DocumentObjectGroupPython] G4_CESIUM_IODIDE  # scripted group (container) (typed FeaturePython)
  Dunit = g/cm3
  Dvalue = 4.51
  Group = -> [Cs_element002,I_element001]
  conduct = 2
  density = 1
  expand = 3
  formula = G4_CESIUM_IODIDE
  name = G4_CESIUM_IODIDE
  specific = 4
FEATURE [App::DocumentObjectGroupPython] C_element028  label="C_element : 013"  # scripted group (container) (typed FeaturePython)
  n = 6
  ref = C_element
FEATURE [App::DocumentObjectGroupPython] H_element025  label="H_element : 013"  # scripted group (container) (typed FeaturePython)
  n = 5
  ref = H_element
FEATURE [App::DocumentObjectGroupPython] Cl_element005  label="Cl_element : 1"  # scripted group (container) (typed FeaturePython)
  n = 1
  ref = Cl_element
FEATURE [App::DocumentObjectGroupPython] G4_CHLOROBENZENE  # scripted group (container) (typed FeaturePython)
  Dunit = g/cm3
  Dvalue = 1.1058
  Group = -> [C_element028,H_element025,Cl_element005]
  conduct = 2
  density = 1
  expand = 3
  formula = G4_CHLOROBENZENE
  name = G4_CHLOROBENZENE
  specific = 4
FEATURE [App::DocumentObjectGroupPython] C_element029  label="C_element : 014"  # scripted group (container) (typed FeaturePython)
  n = 1
  ref = C_element
FEATURE [App::DocumentObjectGroupPython] H_element026  label="H_element : 1"  # scripted group (container) (typed FeaturePython)
  n = 1
  ref = H_element
FEATURE [App::DocumentObjectGroupPython] Cl_element006  label="Cl_element : 3"  # scripted group (container) (typed FeaturePython)
  n = 3
  ref = Cl_element
FEATURE [App::DocumentObjectGroupPython] G4_CHLOROFORM  # scripted group (container) (typed FeaturePython)
  Dunit = g/cm3
  Dvalue = 1.4832
  Group = -> [C_element029,H_element026,Cl_element006]
  conduct = 2
  density = 1
  expand = 3
  formula = G4_CHLOROFORM
  name = G4_CHLOROFORM
  specific = 4
FEATURE [App::DocumentObjectGroupPython] H_element027  label="H_element : 0.010"  # scripted group (container) (typed FeaturePython)
  n = 0.01
FEATURE [App::DocumentObjectGroupPython] C_element030  label="C_element : 0.001"  # scripted group (container) (typed FeaturePython)
  n = 0.001
FEATURE [App::DocumentObjectGroupPython] O_element030  label="O_element : 0.529"  # scripted group (container) (typed FeaturePython)
  n = 0.529107
FEATURE [App::DocumentObjectGroupPython] Na_element005  label="Na_element : 0.016"  # scripted group (container) (typed FeaturePython)
  n = 0.016
FEATURE [App::DocumentObjectGroupPython] Mg_element003  label="Mg_element : 0.004"  # scripted group (container) (typed FeaturePython)
  n = 0.002
FEATURE [App::DocumentObjectGroupPython] Al_element002  label="Al_element : 0.034"  # scripted group (container) (typed FeaturePython)
  n = 0.033872
FEATURE [App::DocumentObjectGroupPython] Si_element002  label="Si_element : 0.337"  # scripted group (container) (typed FeaturePython)
  n = 0.337021
FEATURE [App::DocumentObjectGroupPython] K_element003  label="K_element : 0.013"  # scripted group (container) (typed FeaturePython)
  n = 0.013
FEATURE [App::DocumentObjectGroupPython] Ca_element010  label="Ca_element : 0.044"  # scripted group (container) (typed FeaturePython)
  n = 0.044
FEATURE [App::DocumentObjectGroupPython] Fe_element002  label="Fe_element : 0.014"  # scripted group (container) (typed FeaturePython)
  n = 0.014
FEATURE [App::DocumentObjectGroupPython] G4_CONCRETE  # scripted group (container) (typed FeaturePython)
  Dunit = g/cm3
  Dvalue = 2.3
  Group = -> [H_element027,C_element030,O_element030,Na_element005,Mg_element003,Al_element002,Si_element002,K_element003,Ca_element010,Fe_element002]
  conduct = 2
  density = 1
  expand = 3
  formula = G4_CONCRETE
  name = G4_CONCRETE
  specific = 4
FEATURE [App::DocumentObjectGroupPython] C_element031  label="C_element : 015"  # scripted group (container) (typed FeaturePython)
  n = 6
  ref = C_element
FEATURE [App::DocumentObjectGroupPython] H_element028  label="H_element : 12"  # scripted group (container) (typed FeaturePython)
  n = 12
  ref = H_element
FEATURE [App::DocumentObjectGroupPython] G4_CYCLOHEXANE  # scripted group (container) (typed FeaturePython)
  Dunit = g/cm3
  Dvalue = 0.779
  Group = -> [C_element031,H_element028]
  conduct = 2
  density = 1
  expand = 3
  formula = G4_CYCLOHEXANE
  name = G4_CYCLOHEXANE
  specific = 4
FEATURE [App::DocumentObjectGroupPython] C_element032  label="C_element : 016"  # scripted group (container) (typed FeaturePython)
  n = 6
  ref = C_element
FEATURE [App::DocumentObjectGroupPython] H_element029  label="H_element : 4"  # scripted group (container) (typed FeaturePython)
  n = 4
  ref = H_element
FEATURE [App::DocumentObjectGroupPython] Cl_element007  label="Cl_element : 2"  # scripted group (container) (typed FeaturePython)
  n = 2
  ref = Cl_element
FEATURE [App::DocumentObjectGroupPython] G4_1_2_DICHLOROBENZENE  label="G4_1.2-DICHLOROBENZENE"  # scripted group (container) (typed FeaturePython)
  Dunit = g/cm3
  Dvalue = 1.3048
  Group = -> [C_element032,H_element029,Cl_element007]
  conduct = 2
  density = 1
  expand = 3
  formula = G4_1.2-DICHLOROBENZENE
  name = G4_1.2-DICHLOROBENZENE
  specific = 4
FEATURE [App::DocumentObjectGroupPython] C_element033  label="C_element : 017"  # scripted group (container) (typed FeaturePython)
  n = 4
  ref = C_element
FEATURE [App::DocumentObjectGroupPython] H_element030  label="H_element : 8"  # scripted group (container) (typed FeaturePython)
  n = 8
  ref = H_element
FEATURE [App::DocumentObjectGroupPython] O_element031  label="O_element : 014"  # scripted group (container) (typed FeaturePython)
  n = 1
  ref = O_element
FEATURE [App::DocumentObjectGroupPython] Cl_element008  label="Cl_element : 005"  # scripted group (container) (typed FeaturePython)
  n = 2
  ref = Cl_element
FEATURE [App::DocumentObjectGroupPython] G4_DICHLORODIETHYL_ETHER  # scripted group (container) (typed FeaturePython)
  Dunit = g/cm3
  Dvalue = 1.2199
  Group = -> [C_element033,H_element030,O_element031,Cl_element008]
  conduct = 2
  density = 1
  expand = 3
  formula = G4_DICHLORODIETHYL_ETHER
  name = G4_DICHLORODIETHYL_ETHER
  specific = 4
FEATURE [App::DocumentObjectGroupPython] C_element034  label="C_element : 018"  # scripted group (container) (typed FeaturePython)
  n = 2
  ref = C_element
FEATURE [App::DocumentObjectGroupPython] H_element031  label="H_element : 014"  # scripted group (container) (typed FeaturePython)
  n = 4
  ref = H_element
FEATURE [App::DocumentObjectGroupPython] Cl_element009  label="Cl_element : 006"  # scripted group (container) (typed FeaturePython)
  n = 2
  ref = Cl_element
FEATURE [App::DocumentObjectGroupPython] G4_1_2_DICHLOROETHANE  label="G4_1.2-DICHLOROETHANE"  # scripted group (container) (typed FeaturePython)
  Dunit = g/cm3
  Dvalue = 1.2351
  Group = -> [C_element034,H_element031,Cl_element009]
  conduct = 2
  density = 1
  expand = 3
  formula = G4_1.2-DICHLOROETHANE
  name = G4_1.2-DICHLOROETHANE
  specific = 4
FEATURE [App::DocumentObjectGroupPython] C_element035  label="C_element : 019"  # scripted group (container) (typed FeaturePython)
  n = 4
  ref = C_element
FEATURE [App::DocumentObjectGroupPython] H_element032  label="H_element : 015"  # scripted group (container) (typed FeaturePython)
  n = 10
  ref = H_element
FEATURE [App::DocumentObjectGroupPython] O_element032  label="O_element : 015"  # scripted group (container) (typed FeaturePython)
  n = 1
  ref = O_element
FEATURE [App::DocumentObjectGroupPython] G4_DIETHYL_ETHER  # scripted group (container) (typed FeaturePython)
  Dunit = g/cm3
  Dvalue = 0.71378
  Group = -> [C_element035,H_element032,O_element032]
  conduct = 2
  density = 1
  expand = 3
  formula = G4_DIETHYL_ETHER
  name = G4_DIETHYL_ETHER
  specific = 4
FEATURE [App::DocumentObjectGroupPython] C_element036  label="C_element : 020"  # scripted group (container) (typed FeaturePython)
  n = 3
  ref = C_element
FEATURE [App::DocumentObjectGroupPython] H_element033  label="H_element : 016"  # scripted group (container) (typed FeaturePython)
  n = 7
  ref = H_element
FEATURE [App::DocumentObjectGroupPython] N_element015  label="N_element : 008"  # scripted group (container) (typed FeaturePython)
  n = 1
  ref = N_element
FEATURE [App::DocumentObjectGroupPython] O_element033  label="O_element : 016"  # scripted group (container) (typed FeaturePython)
  n = 1
  ref = O_element
FEATURE [App::DocumentObjectGroupPython] G4_N_N_DIMETHYL_FORMAMIDE  label="G4_N.N-DIMETHYL_FORMAMIDE"  # scripted group (container) (typed FeaturePython)
  Dunit = g/cm3
  Dvalue = 0.9487
  Group = -> [C_element036,H_element033,N_element015,O_element033]
  conduct = 2
  density = 1
  expand = 3
  formula = G4_N.N-DIMETHYL_FORMAMIDE
  name = G4_N.N-DIMETHYL_FORMAMIDE
  specific = 4
FEATURE [App::DocumentObjectGroupPython] C_element037  label="C_element : 021"  # scripted group (container) (typed FeaturePython)
  n = 2
  ref = C_element
FEATURE [App::DocumentObjectGroupPython] H_element034  label="H_element : 017"  # scripted group (container) (typed FeaturePython)
  n = 6
  ref = H_element
FEATURE [App::DocumentObjectGroupPython] O_element034  label="O_element : 017"  # scripted group (container) (typed FeaturePython)
  n = 1
  ref = O_element
FEATURE [App::DocumentObjectGroupPython] S_element009  label="S_element : 003"  # scripted group (container) (typed FeaturePython)
  n = 1
  ref = S_element
FEATURE [App::DocumentObjectGroupPython] G4_DIMETHYL_SULFOXIDE  # scripted group (container) (typed FeaturePython)
  Dunit = g/cm3
  Dvalue = 1.1014
  Group = -> [C_element037,H_element034,O_element034,S_element009]
  conduct = 2
  density = 1
  expand = 3
  formula = G4_DIMETHYL_SULFOXIDE
  name = G4_DIMETHYL_SULFOXIDE
  specific = 4
FEATURE [App::DocumentObjectGroupPython] C_element038  label="C_element : 022"  # scripted group (container) (typed FeaturePython)
  n = 2
  ref = C_element
FEATURE [App::DocumentObjectGroupPython] H_element035  label="H_element : 018"  # scripted group (container) (typed FeaturePython)
  n = 6
  ref = H_element
FEATURE [App::DocumentObjectGroupPython] G4_ETHANE  # scripted group (container) (typed FeaturePython)
  Dunit = g/cm3
  Dvalue = 0.00125324
  Group = -> [C_element038,H_element035]
  conduct = 2
  density = 1
  expand = 3
  formula = G4_ETHANE
  name = G4_ETHANE
  specific = 4
FEATURE [App::DocumentObjectGroupPython] C_element039  label="C_element : 023"  # scripted group (container) (typed FeaturePython)
  n = 2
  ref = C_element
FEATURE [App::DocumentObjectGroupPython] H_element036  label="H_element : 019"  # scripted group (container) (typed FeaturePython)
  n = 6
  ref = H_element
FEATURE [App::DocumentObjectGroupPython] O_element035  label="O_element : 018"  # scripted group (container) (typed FeaturePython)
  n = 1
  ref = O_element
FEATURE [App::DocumentObjectGroupPython] G4_ETHYL_ALCOHOL  # scripted group (container) (typed FeaturePython)
  Dunit = g/cm3
  Dvalue = 0.7893
  Group = -> [C_element039,H_element036,O_element035]
  conduct = 2
  density = 1
  expand = 3
  formula = G4_ETHYL_ALCOHOL
  name = G4_ETHYL_ALCOHOL
  specific = 4
FEATURE [App::DocumentObjectGroupPython] H_element037  label="H_element : 0.090"  # scripted group (container) (typed FeaturePython)
  n = 0.090027
FEATURE [App::DocumentObjectGroupPython] C_element040  label="C_element : 0.585"  # scripted group (container) (typed FeaturePython)
  n = 0.585182
FEATURE [App::DocumentObjectGroupPython] O_element036  label="O_element : 0.325"  # scripted group (container) (typed FeaturePython)
  n = 0.324791
FEATURE [App::DocumentObjectGroupPython] G4_ETHYL_CELLULOSE  # scripted group (container) (typed FeaturePython)
  Dunit = g/cm3
  Dvalue = 1.13
  Group = -> [H_element037,C_element040,O_element036]
  conduct = 2
  density = 1
  expand = 3
  formula = G4_ETHYL_CELLULOSE
  name = G4_ETHYL_CELLULOSE
  specific = 4
FEATURE [App::DocumentObjectGroupPython] C_element041  label="C_element : 024"  # scripted group (container) (typed FeaturePython)
  n = 2
  ref = C_element
FEATURE [App::DocumentObjectGroupPython] H_element038  label="H_element : 020"  # scripted group (container) (typed FeaturePython)
  n = 4
  ref = H_element
FEATURE [App::DocumentObjectGroupPython] G4_ETHYLENE  # scripted group (container) (typed FeaturePython)
  Dunit = g/cm3
  Dvalue = 0.00117497
  Group = -> [C_element041,H_element038]
  conduct = 2
  density = 1
  expand = 3
  formula = G4_ETHYLENE
  name = G4_ETHYLENE
  specific = 4
FEATURE [App::DocumentObjectGroupPython] H_element039  label="H_element : 0.096"  # scripted group (container) (typed FeaturePython)
  n = 0.096
FEATURE [App::DocumentObjectGroupPython] C_element042  label="C_element : 0.195"  # scripted group (container) (typed FeaturePython)
  n = 0.195
FEATURE [App::DocumentObjectGroupPython] N_element016  label="N_element : 0.057"  # scripted group (container) (typed FeaturePython)
  n = 0.057
FEATURE [App::DocumentObjectGroupPython] O_element037  label="O_element : 0.646"  # scripted group (container) (typed FeaturePython)
  n = 0.646
FEATURE [App::DocumentObjectGroupPython] Na_element006  label="Na_element : 0.017"  # scripted group (container) (typed FeaturePython)
  n = 0.001
FEATURE [App::DocumentObjectGroupPython] P_element005  label="P_element : 0.104"  # scripted group (container) (typed FeaturePython)
  n = 0.001
FEATURE [App::DocumentObjectGroupPython] S_element010  label="S_element : 0.016"  # scripted group (container) (typed FeaturePython)
  n = 0.003
FEATURE [App::DocumentObjectGroupPython] Cl_element010  label="Cl_element : 0.005"  # scripted group (container) (typed FeaturePython)
  n = 0.001
FEATURE [App::DocumentObjectGroupPython] G4_EYE_LENS_ICRP  # scripted group (container) (typed FeaturePython)
  Dunit = g/cm3
  Dvalue = 1.07
  Group = -> [H_element039,C_element042,N_element016,O_element037,Na_element006,P_element005,S_element010,Cl_element010]
  conduct = 2
  density = 1
  expand = 3
  formula = G4_EYE_LENS_ICRP
  name = G4_EYE_LENS_ICRP
  specific = 4
FEATURE [App::DocumentObjectGroupPython] Fe_element003  label="Fe_element : 2"  # scripted group (container) (typed FeaturePython)
  n = 2
  ref = Fe_element
FEATURE [App::DocumentObjectGroupPython] O_element038  label="O_element : 019"  # scripted group (container) (typed FeaturePython)
  n = 3
  ref = O_element
FEATURE [App::DocumentObjectGroupPython] G4_FERRIC_OXIDE  # scripted group (container) (typed FeaturePython)
  Dunit = g/cm3
  Dvalue = 5.2
  Group = -> [Fe_element003,O_element038]
  conduct = 2
  density = 1
  expand = 3
  formula = G4_FERRIC_OXIDE
  name = G4_FERRIC_OXIDE
  specific = 4
FEATURE [App::DocumentObjectGroupPython] Fe_element004  label="Fe_element : 1"  # scripted group (container) (typed FeaturePython)
  n = 1
  ref = Fe_element
FEATURE [App::DocumentObjectGroupPython] B_element003  label="B_element : 1"  # scripted group (container) (typed FeaturePython)
  n = 1
  ref = B_element
FEATURE [App::DocumentObjectGroupPython] G4_FERROBORIDE  # scripted group (container) (typed FeaturePython)
  Dunit = g/cm3
  Dvalue = 7.15
  Group = -> [Fe_element004,B_element003]
  conduct = 2
  density = 1
  expand = 3
  formula = G4_FERROBORIDE
  name = G4_FERROBORIDE
  specific = 4
FEATURE [App::DocumentObjectGroupPython] Fe_element005  label="Fe_element : 003"  # scripted group (container) (typed FeaturePython)
  n = 1
  ref = Fe_element
FEATURE [App::DocumentObjectGroupPython] O_element039  label="O_element : 020"  # scripted group (container) (typed FeaturePython)
  n = 1
  ref = O_element
FEATURE [App::DocumentObjectGroupPython] G4_FERROUS_OXIDE  # scripted group (container) (typed FeaturePython)
  Dunit = g/cm3
  Dvalue = 5.7
  Group = -> [Fe_element005,O_element039]
  conduct = 2
  density = 1
  expand = 3
  formula = G4_FERROUS_OXIDE
  name = G4_FERROUS_OXIDE
  specific = 4
FEATURE [App::DocumentObjectGroupPython] H_element040  label="H_element : 0.115"  # scripted group (container) (typed FeaturePython)
  n = 0.108259
FEATURE [App::DocumentObjectGroupPython] N_element017  label="N_element : 0.000"  # scripted group (container) (typed FeaturePython)
  n = 2.7e-05
FEATURE [App::DocumentObjectGroupPython] O_element040  label="O_element : 0.879"  # scripted group (container) (typed FeaturePython)
  n = 0.878636
FEATURE [App::DocumentObjectGroupPython] Na_element007  label="Na_element : 0.000"  # scripted group (container) (typed FeaturePython)
  n = 2.2e-05
FEATURE [App::DocumentObjectGroupPython] S_element011  label="S_element : 0.013"  # scripted group (container) (typed FeaturePython)
  n = 0.012968
FEATURE [App::DocumentObjectGroupPython] Cl_element011  label="Cl_element : 0.000"  # scripted group (container) (typed FeaturePython)
  n = 3.4e-05
FEATURE [App::DocumentObjectGroupPython] Fe_element006  label="Fe_element : 0.000"  # scripted group (container) (typed FeaturePython)
  n = 5.4e-05
FEATURE [App::DocumentObjectGroupPython] G4_FERROUS_SULFATE  # scripted group (container) (typed FeaturePython)
  Dunit = g/cm3
  Dvalue = 1.024
  Group = -> [H_element040,N_element017,O_element040,Na_element007,S_element011,Cl_element011,Fe_element006]
  conduct = 2
  density = 1
  expand = 3
  formula = G4_FERROUS_SULFATE
  name = G4_FERROUS_SULFATE
  specific = 4
FEATURE [App::DocumentObjectGroupPython] C_element043  label="C_element : 0.099"  # scripted group (container) (typed FeaturePython)
  n = 0.099335
FEATURE [App::DocumentObjectGroupPython] F_element007  label="F_element : 0.314"  # scripted group (container) (typed FeaturePython)
  n = 0.314247
FEATURE [App::DocumentObjectGroupPython] Cl_element012  label="Cl_element : 0.586"  # scripted group (container) (typed FeaturePython)
  n = 0.586418
FEATURE [App::DocumentObjectGroupPython] G4_FREON_12  label="G4_FREON-12"  # scripted group (container) (typed FeaturePython)
  Dunit = g/cm3
  Dvalue = 1.12
  Group = -> [C_element043,F_element007,Cl_element012]
  conduct = 2
  density = 1
  expand = 3
  formula = G4_FREON-12
  name = G4_FREON-12
  specific = 4
FEATURE [App::DocumentObjectGroupPython] C_element044  label="C_element : 0.057"  # scripted group (container) (typed FeaturePython)
  n = 0.057245
FEATURE [App::DocumentObjectGroupPython] F_element008  label="F_element : 0.181"  # scripted group (container) (typed FeaturePython)
  n = 0.181096
FEATURE [App::DocumentObjectGroupPython] Br_element001  label="Br_element : 0.762"  # scripted group (container) (typed FeaturePython)
  n = 0.761659
FEATURE [App::DocumentObjectGroupPython] G4_FREON_12B2  label="G4_FREON-12B2"  # scripted group (container) (typed FeaturePython)
  Dunit = g/cm3
  Dvalue = 1.8
  Group = -> [C_element044,F_element008,Br_element001]
  conduct = 2
  density = 1
  expand = 3
  formula = G4_FREON-12B2
  name = G4_FREON-12B2
  specific = 4
FEATURE [App::DocumentObjectGroupPython] C_element045  label="C_element : 0.115"  # scripted group (container) (typed FeaturePython)
  n = 0.114983
FEATURE [App::DocumentObjectGroupPython] F_element009  label="F_element : 0.546"  # scripted group (container) (typed FeaturePython)
  n = 0.545621
FEATURE [App::DocumentObjectGroupPython] Cl_element013  label="Cl_element : 0.339"  # scripted group (container) (typed FeaturePython)
  n = 0.339396
FEATURE [App::DocumentObjectGroupPython] G4_FREON_13  label="G4_FREON-13"  # scripted group (container) (typed FeaturePython)
  Dunit = g/cm3
  Dvalue = 0.95
  Group = -> [C_element045,F_element009,Cl_element013]
  conduct = 2
  density = 1
  expand = 3
  formula = G4_FREON-13
  name = G4_FREON-13
  specific = 4
FEATURE [App::DocumentObjectGroupPython] C_element046  label="C_element : 025"  # scripted group (container) (typed FeaturePython)
  n = 1
  ref = C_element
FEATURE [App::DocumentObjectGroupPython] F_element010  label="F_element : 3"  # scripted group (container) (typed FeaturePython)
  n = 3
  ref = F_element
FEATURE [App::DocumentObjectGroupPython] Br_element002  label="Br_element : 1"  # scripted group (container) (typed FeaturePython)
  n = 1
  ref = Br_element
FEATURE [App::DocumentObjectGroupPython] G4_FREON_13B1  label="G4_FREON-13B1"  # scripted group (container) (typed FeaturePython)
  Dunit = g/cm3
  Dvalue = 1.5
  Group = -> [C_element046,F_element010,Br_element002]
  conduct = 2
  density = 1
  expand = 3
  formula = G4_FREON-13B1
  name = G4_FREON-13B1
  specific = 4
FEATURE [App::DocumentObjectGroupPython] C_element047  label="C_element : 0.061"  # scripted group (container) (typed FeaturePython)
  n = 0.061309
FEATURE [App::DocumentObjectGroupPython] F_element011  label="F_element : 0.291"  # scripted group (container) (typed FeaturePython)
  n = 0.290924
FEATURE [App::DocumentObjectGroupPython] I_element002  label="I_element : 0.648"  # scripted group (container) (typed FeaturePython)
  n = 0.647767
FEATURE [App::DocumentObjectGroupPython] G4_FREON_13I1  label="G4_FREON-13I1"  # scripted group (container) (typed FeaturePython)
  Dunit = g/cm3
  Dvalue = 1.8
  Group = -> [C_element047,F_element011,I_element002]
  conduct = 2
  density = 1
  expand = 3
  formula = G4_FREON-13I1
  name = G4_FREON-13I1
  specific = 4
FEATURE [App::DocumentObjectGroupPython] Gd_element001  label="Gd_element : 2"  # scripted group (container) (typed FeaturePython)
  n = 2
  ref = Gd_element
FEATURE [App::DocumentObjectGroupPython] O_element041  label="O_element : 021"  # scripted group (container) (typed FeaturePython)
  n = 2
  ref = O_element
FEATURE [App::DocumentObjectGroupPython] S_element012  label="S_element : 004"  # scripted group (container) (typed FeaturePython)
  n = 1
  ref = S_element
FEATURE [App::DocumentObjectGroupPython] G4_GADOLINIUM_OXYSULFIDE  # scripted group (container) (typed FeaturePython)
  Dunit = g/cm3
  Dvalue = 7.44
  Group = -> [Gd_element001,O_element041,S_element012]
  conduct = 2
  density = 1
  expand = 3
  formula = G4_GADOLINIUM_OXYSULFIDE
  name = G4_GADOLINIUM_OXYSULFIDE
  specific = 4
FEATURE [App::DocumentObjectGroupPython] Ga_element001  label="Ga_element : 1"  # scripted group (container) (typed FeaturePython)
  n = 1
  ref = Ga_element
FEATURE [App::DocumentObjectGroupPython] As_element001  label="As_element : 1"  # scripted group (container) (typed FeaturePython)
  n = 1
  ref = As_element
FEATURE [App::DocumentObjectGroupPython] G4_GALLIUM_ARSENIDE  # scripted group (container) (typed FeaturePython)
  Dunit = g/cm3
  Dvalue = 5.31
  Group = -> [Ga_element001,As_element001]
  conduct = 2
  density = 1
  expand = 3
  formula = G4_GALLIUM_ARSENIDE
  name = G4_GALLIUM_ARSENIDE
  specific = 4
FEATURE [App::DocumentObjectGroupPython] H_element041  label="H_element : 0.081"  # scripted group (container) (typed FeaturePython)
  n = 0.08118
FEATURE [App::DocumentObjectGroupPython] C_element048  label="C_element : 0.416"  # scripted group (container) (typed FeaturePython)
  n = 0.41606
FEATURE [App::DocumentObjectGroupPython] N_element018  label="N_element : 0.111"  # scripted group (container) (typed FeaturePython)
  n = 0.11124
FEATURE [App::DocumentObjectGroupPython] O_element042  label="O_element : 0.381"  # scripted group (container) (typed FeaturePython)
  n = 0.38064
FEATURE [App::DocumentObjectGroupPython] S_element013  label="S_element : 0.011"  # scripted group (container) (typed FeaturePython)
  n = 0.01088
FEATURE [App::DocumentObjectGroupPython] G4_GEL_PHOTO_EMULSION  # scripted group (container) (typed FeaturePython)
  Dunit = g/cm3
  Dvalue = 1.2914
  Group = -> [H_element041,C_element048,N_element018,O_element042,S_element013]
  conduct = 2
  density = 1
  expand = 3
  formula = G4_GEL_PHOTO_EMULSION
  name = G4_GEL_PHOTO_EMULSION
  specific = 4
FEATURE [App::DocumentObjectGroupPython] B_element004  label="B_element : 0.040"  # scripted group (container) (typed FeaturePython)
  n = 0.0400639
FEATURE [App::DocumentObjectGroupPython] O_element043  label="O_element : 0.540"  # scripted group (container) (typed FeaturePython)
  n = 0.539561
FEATURE [App::DocumentObjectGroupPython] Na_element008  label="Na_element : 0.028"  # scripted group (container) (typed FeaturePython)
  n = 0.0281909
FEATURE [App::DocumentObjectGroupPython] Al_element003  label="Al_element : 0.012"  # scripted group (container) (typed FeaturePython)
  n = 0.011644
FEATURE [App::DocumentObjectGroupPython] Si_element003  label="Si_element : 0.377"  # scripted group (container) (typed FeaturePython)
  n = 0.377219
FEATURE [App::DocumentObjectGroupPython] K_element004  label="K_element : 0.014"  # scripted group (container) (typed FeaturePython)
  n = 0.00332099
FEATURE [App::DocumentObjectGroupPython] G4_Pyrex_Glass  # scripted group (container) (typed FeaturePython)
  Dunit = g/cm3
  Dvalue = 2.23
  Group = -> [B_element004,O_element043,Na_element008,Al_element003,Si_element003,K_element004]
  conduct = 2
  density = 1
  expand = 3
  formula = G4_Pyrex_Glass
  name = G4_Pyrex_Glass
  specific = 4
FEATURE [App::DocumentObjectGroupPython] O_element044  label="O_element : 0.156"  # scripted group (container) (typed FeaturePython)
  n = 0.156453
FEATURE [App::DocumentObjectGroupPython] Si_element004  label="Si_element : 0.081"  # scripted group (container) (typed FeaturePython)
  n = 0.080866
FEATURE [App::DocumentObjectGroupPython] Ti_element001  label="Ti_element : 0.008"  # scripted group (container) (typed FeaturePython)
  n = 0.008092
FEATURE [App::DocumentObjectGroupPython] As_element002  label="As_element : 0.003"  # scripted group (container) (typed FeaturePython)
  n = 0.002651
FEATURE [App::DocumentObjectGroupPython] Pb_element001  label="Pb_element : 0.752"  # scripted group (container) (typed FeaturePython)
  n = 0.751938
FEATURE [App::DocumentObjectGroupPython] G4_GLASS_LEAD  # scripted group (container) (typed FeaturePython)
  Dunit = g/cm3
  Dvalue = 6.22
  Group = -> [O_element044,Si_element004,Ti_element001,As_element002,Pb_element001]
  conduct = 2
  density = 1
  expand = 3
  formula = G4_GLASS_LEAD
  name = G4_GLASS_LEAD
  specific = 4
FEATURE [App::DocumentObjectGroupPython] O_element045  label="O_element : 0.460"  # scripted group (container) (typed FeaturePython)
  n = 0.4598
FEATURE [App::DocumentObjectGroupPython] Na_element009  label="Na_element : 0.096"  # scripted group (container) (typed FeaturePython)
  n = 0.0964411
FEATURE [App::DocumentObjectGroupPython] Si_element005  label="Si_element : 0.378"  # scripted group (container) (typed FeaturePython)
  n = 0.336553
FEATURE [App::DocumentObjectGroupPython] Ca_element011  label="Ca_element : 0.107"  # scripted group (container) (typed FeaturePython)
  n = 0.107205
FEATURE [App::DocumentObjectGroupPython] G4_GLASS_PLATE  # scripted group (container) (typed FeaturePython)
  Dunit = g/cm3
  Dvalue = 2.4
  Group = -> [O_element045,Na_element009,Si_element005,Ca_element011]
  conduct = 2
  density = 1
  expand = 3
  formula = G4_GLASS_PLATE
  name = G4_GLASS_PLATE
  specific = 4
FEATURE [App::DocumentObjectGroupPython] C_element049  label="C_element : 026"  # scripted group (container) (typed FeaturePython)
  n = 5
  ref = C_element
FEATURE [App::DocumentObjectGroupPython] H_element042  label="H_element : 021"  # scripted group (container) (typed FeaturePython)
  n = 10
  ref = H_element
FEATURE [App::DocumentObjectGroupPython] N_element019  label="N_element : 2"  # scripted group (container) (typed FeaturePython)
  n = 2
  ref = N_element
FEATURE [App::DocumentObjectGroupPython] O_element046  label="O_element : 022"  # scripted group (container) (typed FeaturePython)
  n = 3
  ref = O_element
FEATURE [App::DocumentObjectGroupPython] G4_GLUTAMINE  # scripted group (container) (typed FeaturePython)
  Dunit = g/cm3
  Dvalue = 1.46
  Group = -> [C_element049,H_element042,N_element019,O_element046]
  conduct = 2
  density = 1
  expand = 3
  formula = G4_GLUTAMINE
  name = G4_GLUTAMINE
  specific = 4
FEATURE [App::DocumentObjectGroupPython] C_element050  label="C_element : 027"  # scripted group (container) (typed FeaturePython)
  n = 3
  ref = C_element
FEATURE [App::DocumentObjectGroupPython] H_element043  label="H_element : 022"  # scripted group (container) (typed FeaturePython)
  n = 8
  ref = H_element
FEATURE [App::DocumentObjectGroupPython] O_element047  label="O_element : 023"  # scripted group (container) (typed FeaturePython)
  n = 3
  ref = O_element
FEATURE [App::DocumentObjectGroupPython] G4_GLYCEROL  # scripted group (container) (typed FeaturePython)
  Dunit = g/cm3
  Dvalue = 1.2613
  Group = -> [C_element050,H_element043,O_element047]
  conduct = 2
  density = 1
  expand = 3
  formula = G4_GLYCEROL
  name = G4_GLYCEROL
  specific = 4
FEATURE [App::DocumentObjectGroupPython] C_element051  label="C_element : 028"  # scripted group (container) (typed FeaturePython)
  n = 5
  ref = C_element
FEATURE [App::DocumentObjectGroupPython] H_element044  label="H_element : 023"  # scripted group (container) (typed FeaturePython)
  n = 5
  ref = H_element
FEATURE [App::DocumentObjectGroupPython] N_element020  label="N_element : 009"  # scripted group (container) (typed FeaturePython)
  n = 5
  ref = N_element
FEATURE [App::DocumentObjectGroupPython] O_element048  label="O_element : 024"  # scripted group (container) (typed FeaturePython)
  n = 1
  ref = O_element
FEATURE [App::DocumentObjectGroupPython] G4_GUANINE  # scripted group (container) (typed FeaturePython)
  Dunit = g/cm3
  Dvalue = 2.2
  Group = -> [C_element051,H_element044,N_element020,O_element048]
  conduct = 2
  density = 1
  expand = 3
  formula = G4_GUANINE
  name = G4_GUANINE
  specific = 4
FEATURE [App::DocumentObjectGroupPython] Ca_element012  label="Ca_element : 006"  # scripted group (container) (typed FeaturePython)
  n = 1
  ref = Ca_element
FEATURE [App::DocumentObjectGroupPython] S_element014  label="S_element : 005"  # scripted group (container) (typed FeaturePython)
  n = 1
  ref = S_element
FEATURE [App::DocumentObjectGroupPython] O_element049  label="O_element : 6"  # scripted group (container) (typed FeaturePython)
  n = 6
  ref = O_element
FEATURE [App::DocumentObjectGroupPython] H_element045  label="H_element : 024"  # scripted group (container) (typed FeaturePython)
  n = 4
  ref = H_element
FEATURE [App::DocumentObjectGroupPython] G4_GYPSUM  # scripted group (container) (typed FeaturePython)
  Dunit = g/cm3
  Dvalue = 2.32
  Group = -> [Ca_element012,S_element014,O_element049,H_element045]
  conduct = 2
  density = 1
  expand = 3
  formula = G4_GYPSUM
  name = G4_GYPSUM
  specific = 4
FEATURE [App::DocumentObjectGroupPython] C_element052  label="C_element : 7"  # scripted group (container) (typed FeaturePython)
  n = 7
  ref = C_element
FEATURE [App::DocumentObjectGroupPython] H_element046  label="H_element : 16"  # scripted group (container) (typed FeaturePython)
  n = 16
  ref = H_element
FEATURE [App::DocumentObjectGroupPython] G4_N_HEPTANE  label="G4_N-HEPTANE"  # scripted group (container) (typed FeaturePython)
  Dunit = g/cm3
  Dvalue = 0.68376
  Group = -> [C_element052,H_element046]
  conduct = 2
  density = 1
  expand = 3
  formula = G4_N-HEPTANE
  name = G4_N-HEPTANE
  specific = 4
FEATURE [App::DocumentObjectGroupPython] C_element053  label="C_element : 029"  # scripted group (container) (typed FeaturePython)
  n = 6
  ref = C_element
FEATURE [App::DocumentObjectGroupPython] H_element047  label="H_element : 14"  # scripted group (container) (typed FeaturePython)
  n = 14
  ref = H_element
FEATURE [App::DocumentObjectGroupPython] G4_N_HEXANE  label="G4_N-HEXANE"  # scripted group (container) (typed FeaturePython)
  Dunit = g/cm3
  Dvalue = 0.6603
  Group = -> [C_element053,H_element047]
  conduct = 2
  density = 1
  expand = 3
  formula = G4_N-HEXANE
  name = G4_N-HEXANE
  specific = 4
FEATURE [App::DocumentObjectGroupPython] C_element054  label="C_element : 22"  # scripted group (container) (typed FeaturePython)
  n = 22
  ref = C_element
FEATURE [App::DocumentObjectGroupPython] H_element048  label="H_element : 025"  # scripted group (container) (typed FeaturePython)
  n = 10
  ref = H_element
FEATURE [App::DocumentObjectGroupPython] N_element021  label="N_element : 010"  # scripted group (container) (typed FeaturePython)
  n = 2
  ref = N_element
FEATURE [App::DocumentObjectGroupPython] O_element050  label="O_element : 025"  # scripted group (container) (typed FeaturePython)
  n = 5
  ref = O_element
FEATURE [App::DocumentObjectGroupPython] G4_KAPTON  # scripted group (container) (typed FeaturePython)
  Dunit = g/cm3
  Dvalue = 1.42
  Group = -> [C_element054,H_element048,N_element021,O_element050]
  conduct = 2
  density = 1
  expand = 3
  formula = G4_KAPTON
  name = G4_KAPTON
  specific = 4
FEATURE [App::DocumentObjectGroupPython] La_element001  label="La_element : 1"  # scripted group (container) (typed FeaturePython)
  n = 1
  ref = La_element
FEATURE [App::DocumentObjectGroupPython] Br_element003  label="Br_element : 002"  # scripted group (container) (typed FeaturePython)
  n = 1
  ref = Br_element
FEATURE [App::DocumentObjectGroupPython] O_element051  label="O_element : 026"  # scripted group (container) (typed FeaturePython)
  n = 1
  ref = O_element
FEATURE [App::DocumentObjectGroupPython] G4_LANTHANUM_OXYBROMIDE  # scripted group (container) (typed FeaturePython)
  Dunit = g/cm3
  Dvalue = 6.28
  Group = -> [La_element001,Br_element003,O_element051]
  conduct = 2
  density = 1
  expand = 3
  formula = G4_LANTHANUM_OXYBROMIDE
  name = G4_LANTHANUM_OXYBROMIDE
  specific = 4
FEATURE [App::DocumentObjectGroupPython] La_element002  label="La_element : 2"  # scripted group (container) (typed FeaturePython)
  n = 2
  ref = La_element
FEATURE [App::DocumentObjectGroupPython] O_element052  label="O_element : 027"  # scripted group (container) (typed FeaturePython)
  n = 2
  ref = O_element
FEATURE [App::DocumentObjectGroupPython] S_element015  label="S_element : 006"  # scripted group (container) (typed FeaturePython)
  n = 1
  ref = S_element
FEATURE [App::DocumentObjectGroupPython] G4_LANTHANUM_OXYSULFIDE  # scripted group (container) (typed FeaturePython)
  Dunit = g/cm3
  Dvalue = 5.86
  Group = -> [La_element002,O_element052,S_element015]
  conduct = 2
  density = 1
  expand = 3
  formula = G4_LANTHANUM_OXYSULFIDE
  name = G4_LANTHANUM_OXYSULFIDE
  specific = 4
FEATURE [App::DocumentObjectGroupPython] O_element053  label="O_element : 0.072"  # scripted group (container) (typed FeaturePython)
  n = 0.071682
FEATURE [App::DocumentObjectGroupPython] Pb_element002  label="Pb_element : 0.928"  # scripted group (container) (typed FeaturePython)
  n = 0.928318
FEATURE [App::DocumentObjectGroupPython] G4_LEAD_OXIDE  # scripted group (container) (typed FeaturePython)
  Dunit = g/cm3
  Dvalue = 9.53
  Group = -> [O_element053,Pb_element002]
  conduct = 2
  density = 1
  expand = 3
  formula = G4_LEAD_OXIDE
  name = G4_LEAD_OXIDE
  specific = 4
FEATURE [App::DocumentObjectGroupPython] Li_element001  label="Li_element : 1"  # scripted group (container) (typed FeaturePython)
  n = 1
  ref = Li_element
FEATURE [App::DocumentObjectGroupPython] N_element022  label="N_element : 011"  # scripted group (container) (typed FeaturePython)
  n = 1
  ref = N_element
FEATURE [App::DocumentObjectGroupPython] H_element049  label="H_element : 026"  # scripted group (container) (typed FeaturePython)
  n = 2
  ref = H_element
FEATURE [App::DocumentObjectGroupPython] G4_LITHIUM_AMIDE  # scripted group (container) (typed FeaturePython)
  Dunit = g/cm3
  Dvalue = 1.178
  Group = -> [Li_element001,N_element022,H_element049]
  conduct = 2
  density = 1
  expand = 3
  formula = G4_LITHIUM_AMIDE
  name = G4_LITHIUM_AMIDE
  specific = 4
FEATURE [App::DocumentObjectGroupPython] Li_element002  label="Li_element : 2"  # scripted group (container) (typed FeaturePython)
  n = 2
  ref = Li_element
FEATURE [App::DocumentObjectGroupPython] C_element055  label="C_element : 030"  # scripted group (container) (typed FeaturePython)
  n = 1
  ref = C_element
FEATURE [App::DocumentObjectGroupPython] O_element054  label="O_element : 028"  # scripted group (container) (typed FeaturePython)
  n = 3
  ref = O_element
FEATURE [App::DocumentObjectGroupPython] G4_LITHIUM_CARBONATE  # scripted group (container) (typed FeaturePython)
  Dunit = g/cm3
  Dvalue = 2.11
  Group = -> [Li_element002,C_element055,O_element054]
  conduct = 2
  density = 1
  expand = 3
  formula = G4_LITHIUM_CARBONATE
  name = G4_LITHIUM_CARBONATE
  specific = 4
FEATURE [App::DocumentObjectGroupPython] Li_element003  label="Li_element : 003"  # scripted group (container) (typed FeaturePython)
  n = 1
  ref = Li_element
FEATURE [App::DocumentObjectGroupPython] F_element012  label="F_element : 004"  # scripted group (container) (typed FeaturePython)
  n = 1
  ref = F_element
FEATURE [App::DocumentObjectGroupPython] G4_LITHIUM_FLUORIDE  # scripted group (container) (typed FeaturePython)
  Dunit = g/cm3
  Dvalue = 2.635
  Group = -> [Li_element003,F_element012]
  conduct = 2
  density = 1
  expand = 3
  formula = G4_LITHIUM_FLUORIDE
  name = G4_LITHIUM_FLUORIDE
  specific = 4
FEATURE [App::DocumentObjectGroupPython] Li_element004  label="Li_element : 004"  # scripted group (container) (typed FeaturePython)
  n = 1
  ref = Li_element
FEATURE [App::DocumentObjectGroupPython] H_element050  label="H_element : 027"  # scripted group (container) (typed FeaturePython)
  n = 1
  ref = H_element
FEATURE [App::DocumentObjectGroupPython] G4_LITHIUM_HYDRIDE  # scripted group (container) (typed FeaturePython)
  Dunit = g/cm3
  Dvalue = 0.82
  Group = -> [Li_element004,H_element050]
  conduct = 2
  density = 1
  expand = 3
  formula = G4_LITHIUM_HYDRIDE
  name = G4_LITHIUM_HYDRIDE
  specific = 4
FEATURE [App::DocumentObjectGroupPython] Li_element005  label="Li_element : 005"  # scripted group (container) (typed FeaturePython)
  n = 1
  ref = Li_element
FEATURE [App::DocumentObjectGroupPython] I_element003  label="I_element : 002"  # scripted group (container) (typed FeaturePython)
  n = 1
  ref = I_element
FEATURE [App::DocumentObjectGroupPython] G4_LITHIUM_IODIDE  # scripted group (container) (typed FeaturePython)
  Dunit = g/cm3
  Dvalue = 3.494
  Group = -> [Li_element005,I_element003]
  conduct = 2
  density = 1
  expand = 3
  formula = G4_LITHIUM_IODIDE
  name = G4_LITHIUM_IODIDE
  specific = 4
FEATURE [App::DocumentObjectGroupPython] Li_element006  label="Li_element : 006"  # scripted group (container) (typed FeaturePython)
  n = 2
  ref = Li_element
FEATURE [App::DocumentObjectGroupPython] O_element055  label="O_element : 029"  # scripted group (container) (typed FeaturePython)
  n = 1
  ref = O_element
FEATURE [App::DocumentObjectGroupPython] G4_LITHIUM_OXIDE  # scripted group (container) (typed FeaturePython)
  Dunit = g/cm3
  Dvalue = 2.013
  Group = -> [Li_element006,O_element055]
  conduct = 2
  density = 1
  expand = 3
  formula = G4_LITHIUM_OXIDE
  name = G4_LITHIUM_OXIDE
  specific = 4
FEATURE [App::DocumentObjectGroupPython] Li_element007  label="Li_element : 007"  # scripted group (container) (typed FeaturePython)
  n = 2
  ref = Li_element
FEATURE [App::DocumentObjectGroupPython] B_element005  label="B_element : 005"  # scripted group (container) (typed FeaturePython)
  n = 4
  ref = B_element
FEATURE [App::DocumentObjectGroupPython] O_element056  label="O_element : 7"  # scripted group (container) (typed FeaturePython)
  n = 7
  ref = O_element
FEATURE [App::DocumentObjectGroupPython] G4_LITHIUM_TETRABORATE  # scripted group (container) (typed FeaturePython)
  Dunit = g/cm3
  Dvalue = 2.44
  Group = -> [Li_element007,B_element005,O_element056]
  conduct = 2
  density = 1
  expand = 3
  formula = G4_LITHIUM_TETRABORATE
  name = G4_LITHIUM_TETRABORATE
  specific = 4
FEATURE [App::DocumentObjectGroupPython] H_element051  label="H_element : 0.105"  # scripted group (container) (typed FeaturePython)
  n = 0.105
FEATURE [App::DocumentObjectGroupPython] C_element056  label="C_element : 0.083"  # scripted group (container) (typed FeaturePython)
  n = 0.083
FEATURE [App::DocumentObjectGroupPython] N_element023  label="N_element : 0.023"  # scripted group (container) (typed FeaturePython)
  n = 0.023
FEATURE [App::DocumentObjectGroupPython] O_element057  label="O_element : 0.779"  # scripted group (container) (typed FeaturePython)
  n = 0.779
FEATURE [App::DocumentObjectGroupPython] Na_element010  label="Na_element : 0.097"  # scripted group (container) (typed FeaturePython)
  n = 0.002
FEATURE [App::DocumentObjectGroupPython] P_element006  label="P_element : 0.105"  # scripted group (container) (typed FeaturePython)
  n = 0.001
FEATURE [App::DocumentObjectGroupPython] S_element016  label="S_element : 0.017"  # scripted group (container) (typed FeaturePython)
  n = 0.002
FEATURE [App::DocumentObjectGroupPython] Cl_element014  label="Cl_element : 0.587"  # scripted group (container) (typed FeaturePython)
  n = 0.003
FEATURE [App::DocumentObjectGroupPython] K_element005  label="K_element : 0.015"  # scripted group (container) (typed FeaturePython)
  n = 0.002
FEATURE [App::DocumentObjectGroupPython] G4_LUNG_ICRP  # scripted group (container) (typed FeaturePython)
  Dunit = g/cm3
  Dvalue = 1.04
  Group = -> [H_element051,C_element056,N_element023,O_element057,Na_element010,P_element006,S_element016,Cl_element014,K_element005]
  conduct = 2
  density = 1
  expand = 3
  formula = G4_LUNG_ICRP
  name = G4_LUNG_ICRP
  specific = 4
FEATURE [App::DocumentObjectGroupPython] H_element052  label="H_element : 0.116"  # scripted group (container) (typed FeaturePython)
  n = 0.114318
FEATURE [App::DocumentObjectGroupPython] C_element057  label="C_element : 0.656"  # scripted group (container) (typed FeaturePython)
  n = 0.655824
FEATURE [App::DocumentObjectGroupPython] O_element058  label="O_element : 0.092"  # scripted group (container) (typed FeaturePython)
  n = 0.0921831
FEATURE [App::DocumentObjectGroupPython] Mg_element004  label="Mg_element : 0.135"  # scripted group (container) (typed FeaturePython)
  n = 0.134792
FEATURE [App::DocumentObjectGroupPython] Ca_element013  label="Ca_element : 0.003"  # scripted group (container) (typed FeaturePython)
  n = 0.002883
FEATURE [App::DocumentObjectGroupPython] G4_M3_WAX  # scripted group (container) (typed FeaturePython)
  Dunit = g/cm3
  Dvalue = 1.05
  Group = -> [H_element052,C_element057,O_element058,Mg_element004,Ca_element013]
  conduct = 2
  density = 1
  expand = 3
  formula = G4_M3_WAX
  name = G4_M3_WAX
  specific = 4
FEATURE [App::DocumentObjectGroupPython] Mg_element005  label="Mg_element : 1"  # scripted group (container) (typed FeaturePython)
  n = 1
  ref = Mg_element
FEATURE [App::DocumentObjectGroupPython] C_element058  label="C_element : 031"  # scripted group (container) (typed FeaturePython)
  n = 1
  ref = C_element
FEATURE [App::DocumentObjectGroupPython] O_element059  label="O_element : 030"  # scripted group (container) (typed FeaturePython)
  n = 3
  ref = O_element
FEATURE [App::DocumentObjectGroupPython] G4_MAGNESIUM_CARBONATE  # scripted group (container) (typed FeaturePython)
  Dunit = g/cm3
  Dvalue = 2.958
  Group = -> [Mg_element005,C_element058,O_element059]
  conduct = 2
  density = 1
  expand = 3
  formula = G4_MAGNESIUM_CARBONATE
  name = G4_MAGNESIUM_CARBONATE
  specific = 4
FEATURE [App::DocumentObjectGroupPython] Mg_element006  label="Mg_element : 002"  # scripted group (container) (typed FeaturePython)
  n = 1
  ref = Mg_element
FEATURE [App::DocumentObjectGroupPython] F_element013  label="F_element : 005"  # scripted group (container) (typed FeaturePython)
  n = 2
  ref = F_element
FEATURE [App::DocumentObjectGroupPython] G4_MAGNESIUM_FLUORIDE  # scripted group (container) (typed FeaturePython)
  Dunit = g/cm3
  Dvalue = 3
  Group = -> [Mg_element006,F_element013]
  conduct = 2
  density = 1
  expand = 3
  formula = G4_MAGNESIUM_FLUORIDE
  name = G4_MAGNESIUM_FLUORIDE
  specific = 4
FEATURE [App::DocumentObjectGroupPython] Mg_element007  label="Mg_element : 003"  # scripted group (container) (typed FeaturePython)
  n = 1
  ref = Mg_element
FEATURE [App::DocumentObjectGroupPython] O_element060  label="O_element : 031"  # scripted group (container) (typed FeaturePython)
  n = 1
  ref = O_element
FEATURE [App::DocumentObjectGroupPython] G4_MAGNESIUM_OXIDE  # scripted group (container) (typed FeaturePython)
  Dunit = g/cm3
  Dvalue = 3.58
  Group = -> [Mg_element007,O_element060]
  conduct = 2
  density = 1
  expand = 3
  formula = G4_MAGNESIUM_OXIDE
  name = G4_MAGNESIUM_OXIDE
  specific = 4
FEATURE [App::DocumentObjectGroupPython] Mg_element008  label="Mg_element : 004"  # scripted group (container) (typed FeaturePython)
  n = 1
  ref = Mg_element
FEATURE [App::DocumentObjectGroupPython] B_element006  label="B_element : 006"  # scripted group (container) (typed FeaturePython)
  n = 4
  ref = B_element
FEATURE [App::DocumentObjectGroupPython] O_element061  label="O_element : 032"  # scripted group (container) (typed FeaturePython)
  n = 7
  ref = O_element
FEATURE [App::DocumentObjectGroupPython] G4_MAGNESIUM_TETRABORATE  # scripted group (container) (typed FeaturePython)
  Dunit = g/cm3
  Dvalue = 2.53
  Group = -> [Mg_element008,B_element006,O_element061]
  conduct = 2
  density = 1
  expand = 3
  formula = G4_MAGNESIUM_TETRABORATE
  name = G4_MAGNESIUM_TETRABORATE
  specific = 4
FEATURE [App::DocumentObjectGroupPython] Hg_element001  label="Hg_element : 1"  # scripted group (container) (typed FeaturePython)
  n = 1
  ref = Hg_element
FEATURE [App::DocumentObjectGroupPython] I_element004  label="I_element : 2"  # scripted group (container) (typed FeaturePython)
  n = 2
  ref = I_element
FEATURE [App::DocumentObjectGroupPython] G4_MERCURIC_IODIDE  # scripted group (container) (typed FeaturePython)
  Dunit = g/cm3
  Dvalue = 6.36
  Group = -> [Hg_element001,I_element004]
  conduct = 2
  density = 1
  expand = 3
  formula = G4_MERCURIC_IODIDE
  name = G4_MERCURIC_IODIDE
  specific = 4
FEATURE [App::DocumentObjectGroupPython] C_element059  label="C_element : 032"  # scripted group (container) (typed FeaturePython)
  n = 1
  ref = C_element
FEATURE [App::DocumentObjectGroupPython] H_element053  label="H_element : 028"  # scripted group (container) (typed FeaturePython)
  n = 4
  ref = H_element
FEATURE [App::DocumentObjectGroupPython] G4_METHANE  # scripted group (container) (typed FeaturePython)
  Dunit = g/cm3
  Dvalue = 0.000667151
  Group = -> [C_element059,H_element053]
  conduct = 2
  density = 1
  expand = 3
  formula = G4_METHANE
  name = G4_METHANE
  specific = 4
FEATURE [App::DocumentObjectGroupPython] C_element060  label="C_element : 033"  # scripted group (container) (typed FeaturePython)
  n = 1
  ref = C_element
FEATURE [App::DocumentObjectGroupPython] H_element054  label="H_element : 029"  # scripted group (container) (typed FeaturePython)
  n = 4
  ref = H_element
FEATURE [App::DocumentObjectGroupPython] O_element062  label="O_element : 033"  # scripted group (container) (typed FeaturePython)
  n = 1
  ref = O_element
FEATURE [App::DocumentObjectGroupPython] G4_METHANOL  # scripted group (container) (typed FeaturePython)
  Dunit = g/cm3
  Dvalue = 0.7914
  Group = -> [C_element060,H_element054,O_element062]
  conduct = 2
  density = 1
  expand = 3
  formula = G4_METHANOL
  name = G4_METHANOL
  specific = 4
FEATURE [App::DocumentObjectGroupPython] H_element055  label="H_element : 0.134"  # scripted group (container) (typed FeaturePython)
  n = 0.13404
FEATURE [App::DocumentObjectGroupPython] C_element061  label="C_element : 0.778"  # scripted group (container) (typed FeaturePython)
  n = 0.77796
FEATURE [App::DocumentObjectGroupPython] O_element063  label="O_element : 0.035"  # scripted group (container) (typed FeaturePython)
  n = 0.03502
FEATURE [App::DocumentObjectGroupPython] Mg_element009  label="Mg_element : 0.039"  # scripted group (container) (typed FeaturePython)
  n = 0.038594
FEATURE [App::DocumentObjectGroupPython] Ti_element002  label="Ti_element : 0.014"  # scripted group (container) (typed FeaturePython)
  n = 0.014386
FEATURE [App::DocumentObjectGroupPython] G4_MIX_D_WAX  # scripted group (container) (typed FeaturePython)
  Dunit = g/cm3
  Dvalue = 0.99
  Group = -> [H_element055,C_element061,O_element063,Mg_element009,Ti_element002]
  conduct = 2
  density = 1
  expand = 3
  formula = G4_MIX_D_WAX
  name = G4_MIX_D_WAX
  specific = 4
FEATURE [App::DocumentObjectGroupPython] H_element056  label="H_element : 0.135"  # scripted group (container) (typed FeaturePython)
  n = 0.081192
FEATURE [App::DocumentObjectGroupPython] C_element062  label="C_element : 0.583"  # scripted group (container) (typed FeaturePython)
  n = 0.583442
FEATURE [App::DocumentObjectGroupPython] N_element024  label="N_element : 0.018"  # scripted group (container) (typed FeaturePython)
  n = 0.017798
FEATURE [App::DocumentObjectGroupPython] O_element064  label="O_element : 0.186"  # scripted group (container) (typed FeaturePython)
  n = 0.186381
FEATURE [App::DocumentObjectGroupPython] Mg_element010  label="Mg_element : 0.130"  # scripted group (container) (typed FeaturePython)
  n = 0.130287
FEATURE [App::DocumentObjectGroupPython] Cl_element015  label="Cl_element : 0.588"  # scripted group (container) (typed FeaturePython)
  n = 0.0009
FEATURE [App::DocumentObjectGroupPython] G4_MS20_TISSUE  # scripted group (container) (typed FeaturePython)
  Dunit = g/cm3
  Dvalue = 1
  Group = -> [H_element056,C_element062,N_element024,O_element064,Mg_element010,Cl_element015]
  conduct = 2
  density = 1
  expand = 3
  formula = G4_MS20_TISSUE
  name = G4_MS20_TISSUE
  specific = 4
FEATURE [App::DocumentObjectGroupPython] H_element057  label="H_element : 0.136"  # scripted group (container) (typed FeaturePython)
  n = 0.102
FEATURE [App::DocumentObjectGroupPython] C_element063  label="C_element : 0.143"  # scripted group (container) (typed FeaturePython)
  n = 0.143
FEATURE [App::DocumentObjectGroupPython] N_element025  label="N_element : 0.034"  # scripted group (container) (typed FeaturePython)
  n = 0.034
FEATURE [App::DocumentObjectGroupPython] O_element065  label="O_element : 0.710"  # scripted group (container) (typed FeaturePython)
  n = 0.71
FEATURE [App::DocumentObjectGroupPython] Na_element011  label="Na_element : 0.098"  # scripted group (container) (typed FeaturePython)
  n = 0.001
FEATURE [App::DocumentObjectGroupPython] P_element007  label="P_element : 0.002"  # scripted group (container) (typed FeaturePython)
  n = 0.002
FEATURE [App::DocumentObjectGroupPython] S_element017  label="S_element : 0.018"  # scripted group (container) (typed FeaturePython)
  n = 0.003
FEATURE [App::DocumentObjectGroupPython] Cl_element016  label="Cl_element : 0.589"  # scripted group (container) (typed FeaturePython)
  n = 0.001
FEATURE [App::DocumentObjectGroupPython] K_element006  label="K_element : 0.004"  # scripted group (container) (typed FeaturePython)
  n = 0.004
FEATURE [App::DocumentObjectGroupPython] G4_MUSCLE_SKELETAL_ICRP  # scripted group (container) (typed FeaturePython)
  Dunit = g/cm3
  Dvalue = 1.05
  Group = -> [H_element057,C_element063,N_element025,O_element065,Na_element011,P_element007,S_element017,Cl_element016,K_element006]
  conduct = 2
  density = 1
  expand = 3
  formula = G4_MUSCLE_SKELETAL_ICRP
  name = G4_MUSCLE_SKELETAL_ICRP
  specific = 4
FEATURE [App::DocumentObjectGroupPython] H_element058  label="H_element : 0.137"  # scripted group (container) (typed FeaturePython)
  n = 0.102102
FEATURE [App::DocumentObjectGroupPython] C_element064  label="C_element : 0.123"  # scripted group (container) (typed FeaturePython)
  n = 0.123123
FEATURE [App::DocumentObjectGroupPython] N_element026  label="N_element : 0.756"  # scripted group (container) (typed FeaturePython)
  n = 0.035035
FEATURE [App::DocumentObjectGroupPython] O_element066  label="O_element : 0.730"  # scripted group (container) (typed FeaturePython)
  n = 0.72973
FEATURE [App::DocumentObjectGroupPython] Na_element012  label="Na_element : 0.099"  # scripted group (container) (typed FeaturePython)
  n = 0.001001
FEATURE [App::DocumentObjectGroupPython] P_element008  label="P_element : 0.106"  # scripted group (container) (typed FeaturePython)
  n = 0.002002
FEATURE [App::DocumentObjectGroupPython] S_element018  label="S_element : 0.019"  # scripted group (container) (typed FeaturePython)
  n = 0.004004
FEATURE [App::DocumentObjectGroupPython] K_element007  label="K_element : 0.016"  # scripted group (container) (typed FeaturePython)
  n = 0.003003
FEATURE [App::DocumentObjectGroupPython] G4_MUSCLE_STRIATED_ICRU  # scripted group (container) (typed FeaturePython)
  Dunit = g/cm3
  Dvalue = 1.04
  Group = -> [H_element058,C_element064,N_element026,O_element066,Na_element012,P_element008,S_element018,K_element007]
  conduct = 2
  density = 1
  expand = 3
  formula = G4_MUSCLE_STRIATED_ICRU
  name = G4_MUSCLE_STRIATED_ICRU
  specific = 4
FEATURE [App::DocumentObjectGroupPython] H_element059  label="H_element : 0.098"  # scripted group (container) (typed FeaturePython)
  n = 0.0982341
FEATURE [App::DocumentObjectGroupPython] C_element065  label="C_element : 0.156"  # scripted group (container) (typed FeaturePython)
  n = 0.156214
FEATURE [App::DocumentObjectGroupPython] N_element027  label="N_element : 0.757"  # scripted group (container) (typed FeaturePython)
  n = 0.035451
FEATURE [App::DocumentObjectGroupPython] O_element067  label="O_element : 0.880"  # scripted group (container) (typed FeaturePython)
  n = 0.710101
FEATURE [App::DocumentObjectGroupPython] G4_MUSCLE_WITH_SUCROSE  # scripted group (container) (typed FeaturePython)
  Dunit = g/cm3
  Dvalue = 1.11
  Group = -> [H_element059,C_element065,N_element027,O_element067]
  conduct = 2
  density = 1
  expand = 3
  formula = G4_MUSCLE_WITH_SUCROSE
  name = G4_MUSCLE_WITH_SUCROSE
  specific = 4
FEATURE [App::DocumentObjectGroupPython] H_element060  label="H_element : 0.138"  # scripted group (container) (typed FeaturePython)
  n = 0.101969
FEATURE [App::DocumentObjectGroupPython] C_element066  label="C_element : 0.120"  # scripted group (container) (typed FeaturePython)
  n = 0.120058
FEATURE [App::DocumentObjectGroupPython] N_element028  label="N_element : 0.758"  # scripted group (container) (typed FeaturePython)
  n = 0.035451
FEATURE [App::DocumentObjectGroupPython] O_element068  label="O_element : 0.743"  # scripted group (container) (typed FeaturePython)
  n = 0.742522
FEATURE [App::DocumentObjectGroupPython] G4_MUSCLE_WITHOUT_SUCROSE  # scripted group (container) (typed FeaturePython)
  Dunit = g/cm3
  Dvalue = 1.07
  Group = -> [H_element060,C_element066,N_element028,O_element068]
  conduct = 2
  density = 1
  expand = 3
  formula = G4_MUSCLE_WITHOUT_SUCROSE
  name = G4_MUSCLE_WITHOUT_SUCROSE
  specific = 4
FEATURE [App::DocumentObjectGroupPython] C_element067  label="C_element : 10"  # scripted group (container) (typed FeaturePython)
  n = 10
  ref = C_element
FEATURE [App::DocumentObjectGroupPython] H_element061  label="H_element : 030"  # scripted group (container) (typed FeaturePython)
  n = 8
  ref = H_element
FEATURE [App::DocumentObjectGroupPython] G4_NAPHTHALENE  # scripted group (container) (typed FeaturePython)
  Dunit = g/cm3
  Dvalue = 1.145
  Group = -> [C_element067,H_element061]
  conduct = 2
  density = 1
  expand = 3
  formula = G4_NAPHTHALENE
  name = G4_NAPHTHALENE
  specific = 4
FEATURE [App::DocumentObjectGroupPython] C_element068  label="C_element : 034"  # scripted group (container) (typed FeaturePython)
  n = 6
  ref = C_element
FEATURE [App::DocumentObjectGroupPython] H_element062  label="H_element : 031"  # scripted group (container) (typed FeaturePython)
  n = 5
  ref = H_element
FEATURE [App::DocumentObjectGroupPython] N_element029  label="N_element : 012"  # scripted group (container) (typed FeaturePython)
  n = 1
  ref = N_element
FEATURE [App::DocumentObjectGroupPython] O_element069  label="O_element : 034"  # scripted group (container) (typed FeaturePython)
  n = 2
  ref = O_element
FEATURE [App::DocumentObjectGroupPython] G4_NITROBENZENE  # scripted group (container) (typed FeaturePython)
  Dunit = g/cm3
  Dvalue = 1.19867
  Group = -> [C_element068,H_element062,N_element029,O_element069]
  conduct = 2
  density = 1
  expand = 3
  formula = G4_NITROBENZENE
  name = G4_NITROBENZENE
  specific = 4
FEATURE [App::DocumentObjectGroupPython] N_element030  label="N_element : 013"  # scripted group (container) (typed FeaturePython)
  n = 2
  ref = N_element
FEATURE [App::DocumentObjectGroupPython] O_element070  label="O_element : 035"  # scripted group (container) (typed FeaturePython)
  n = 1
  ref = O_element
FEATURE [App::DocumentObjectGroupPython] G4_NITROUS_OXIDE  # scripted group (container) (typed FeaturePython)
  Dunit = g/cm3
  Dvalue = 0.00183094
  Group = -> [N_element030,O_element070]
  conduct = 2
  density = 1
  expand = 3
  formula = G4_NITROUS_OXIDE
  name = G4_NITROUS_OXIDE
  specific = 4
FEATURE [App::DocumentObjectGroupPython] H_element063  label="H_element : 0.104"  # scripted group (container) (typed FeaturePython)
  n = 0.103509
FEATURE [App::DocumentObjectGroupPython] C_element069  label="C_element : 0.648"  # scripted group (container) (typed FeaturePython)
  n = 0.648416
FEATURE [App::DocumentObjectGroupPython] N_element031  label="N_element : 0.100"  # scripted group (container) (typed FeaturePython)
  n = 0.0995361
FEATURE [App::DocumentObjectGroupPython] O_element071  label="O_element : 0.149"  # scripted group (container) (typed FeaturePython)
  n = 0.148539
FEATURE [App::DocumentObjectGroupPython] G4_NYLON_8062  label="G4_NYLON-8062"  # scripted group (container) (typed FeaturePython)
  Dunit = g/cm3
  Dvalue = 1.08
  Group = -> [H_element063,C_element069,N_element031,O_element071]
  conduct = 2
  density = 1
  expand = 3
  formula = G4_NYLON-8062
  name = G4_NYLON-8062
  specific = 4
FEATURE [App::DocumentObjectGroupPython] C_element070  label="C_element : 035"  # scripted group (container) (typed FeaturePython)
  n = 6
  ref = C_element
FEATURE [App::DocumentObjectGroupPython] H_element064  label="H_element : 11"  # scripted group (container) (typed FeaturePython)
  n = 11
  ref = H_element
FEATURE [App::DocumentObjectGroupPython] N_element032  label="N_element : 014"  # scripted group (container) (typed FeaturePython)
  n = 1
  ref = N_element
FEATURE [App::DocumentObjectGroupPython] O_element072  label="O_element : 036"  # scripted group (container) (typed FeaturePython)
  n = 1
  ref = O_element
FEATURE [App::DocumentObjectGroupPython] G4_NYLON_6_6  label="G4_NYLON-6-6"  # scripted group (container) (typed FeaturePython)
  Dunit = g/cm3
  Dvalue = 1.14
  Group = -> [C_element070,H_element064,N_element032,O_element072]
  conduct = 2
  density = 1
  expand = 3
  formula = G4_NYLON-6-6
  name = G4_NYLON-6-6
  specific = 4
FEATURE [App::DocumentObjectGroupPython] H_element065  label="H_element : 0.139"  # scripted group (container) (typed FeaturePython)
  n = 0.107062
FEATURE [App::DocumentObjectGroupPython] C_element071  label="C_element : 0.680"  # scripted group (container) (typed FeaturePython)
  n = 0.680449
FEATURE [App::DocumentObjectGroupPython] N_element033  label="N_element : 0.099"  # scripted group (container) (typed FeaturePython)
  n = 0.099189
FEATURE [App::DocumentObjectGroupPython] O_element073  label="O_element : 0.113"  # scripted group (container) (typed FeaturePython)
  n = 0.1133
FEATURE [App::DocumentObjectGroupPython] G4_NYLON_6_10  label="G4_NYLON-6-10"  # scripted group (container) (typed FeaturePython)
  Dunit = g/cm3
  Dvalue = 1.14
  Group = -> [H_element065,C_element071,N_element033,O_element073]
  conduct = 2
  density = 1
  expand = 3
  formula = G4_NYLON-6-10
  name = G4_NYLON-6-10
  specific = 4
FEATURE [App::DocumentObjectGroupPython] H_element066  label="H_element : 0.140"  # scripted group (container) (typed FeaturePython)
  n = 0.115476
FEATURE [App::DocumentObjectGroupPython] C_element072  label="C_element : 0.721"  # scripted group (container) (typed FeaturePython)
  n = 0.720818
FEATURE [App::DocumentObjectGroupPython] N_element034  label="N_element : 0.076"  # scripted group (container) (typed FeaturePython)
  n = 0.0764169
FEATURE [App::DocumentObjectGroupPython] O_element074  label="O_element : 0.087"  # scripted group (container) (typed FeaturePython)
  n = 0.0872889
FEATURE [App::DocumentObjectGroupPython] G4_NYLON_11_RILSAN  label="G4_NYLON-11_RILSAN"  # scripted group (container) (typed FeaturePython)
  Dunit = g/cm3
  Dvalue = 1.425
  Group = -> [H_element066,C_element072,N_element034,O_element074]
  conduct = 2
  density = 1
  expand = 3
  formula = G4_NYLON-11_RILSAN
  name = G4_NYLON-11_RILSAN
  specific = 4
FEATURE [App::DocumentObjectGroupPython] C_element073  label="C_element : 8"  # scripted group (container) (typed FeaturePython)
  n = 8
  ref = C_element
FEATURE [App::DocumentObjectGroupPython] H_element067  label="H_element : 18"  # scripted group (container) (typed FeaturePython)
  n = 18
  ref = H_element
FEATURE [App::DocumentObjectGroupPython] G4_OCTANE  # scripted group (container) (typed FeaturePython)
  Dunit = g/cm3
  Dvalue = 0.7026
  Group = -> [C_element073,H_element067]
  conduct = 2
  density = 1
  expand = 3
  formula = G4_OCTANE
  name = G4_OCTANE
  specific = 4
FEATURE [App::DocumentObjectGroupPython] C_element074  label="C_element : 25"  # scripted group (container) (typed FeaturePython)
  n = 25
  ref = C_element
FEATURE [App::DocumentObjectGroupPython] H_element068  label="H_element : 52"  # scripted group (container) (typed FeaturePython)
  n = 52
  ref = H_element
FEATURE [App::DocumentObjectGroupPython] G4_PARAFFIN  # scripted group (container) (typed FeaturePython)
  Dunit = g/cm3
  Dvalue = 0.93
  Group = -> [C_element074,H_element068]
  conduct = 2
  density = 1
  expand = 3
  formula = G4_PARAFFIN
  name = G4_PARAFFIN
  specific = 4
FEATURE [App::DocumentObjectGroupPython] C_element075  label="C_element : 036"  # scripted group (container) (typed FeaturePython)
  n = 5
  ref = C_element
FEATURE [App::DocumentObjectGroupPython] H_element069  label="H_element : 032"  # scripted group (container) (typed FeaturePython)
  n = 12
  ref = H_element
FEATURE [App::DocumentObjectGroupPython] G4_N_PENTANE  label="G4_N-PENTANE"  # scripted group (container) (typed FeaturePython)
  Dunit = g/cm3
  Dvalue = 0.6262
  Group = -> [C_element075,H_element069]
  conduct = 2
  density = 1
  expand = 3
  formula = G4_N-PENTANE
  name = G4_N-PENTANE
  specific = 4
FEATURE [App::DocumentObjectGroupPython] H_element070  label="H_element : 0.014"  # scripted group (container) (typed FeaturePython)
  n = 0.0141
FEATURE [App::DocumentObjectGroupPython] C_element076  label="C_element : 0.072"  # scripted group (container) (typed FeaturePython)
  n = 0.072261
FEATURE [App::DocumentObjectGroupPython] N_element035  label="N_element : 0.019"  # scripted group (container) (typed FeaturePython)
  n = 0.01932
FEATURE [App::DocumentObjectGroupPython] O_element075  label="O_element : 0.066"  # scripted group (container) (typed FeaturePython)
  n = 0.066101
FEATURE [App::DocumentObjectGroupPython] S_element019  label="S_element : 0.020"  # scripted group (container) (typed FeaturePython)
  n = 0.00189
FEATURE [App::DocumentObjectGroupPython] Br_element004  label="Br_element : 0.349"  # scripted group (container) (typed FeaturePython)
  n = 0.349103
FEATURE [App::DocumentObjectGroupPython] Ag_element001  label="Ag_element : 0.474"  # scripted group (container) (typed FeaturePython)
  n = 0.474105
FEATURE [App::DocumentObjectGroupPython] I_element005  label="I_element : 0.003"  # scripted group (container) (typed FeaturePython)
  n = 0.00312
FEATURE [App::DocumentObjectGroupPython] G4_PHOTO_EMULSION  # scripted group (container) (typed FeaturePython)
  Dunit = g/cm3
  Dvalue = 3.815
  Group = -> [H_element070,C_element076,N_element035,O_element075,S_element019,Br_element004,Ag_element001,I_element005]
  conduct = 2
  density = 1
  expand = 3
  formula = G4_PHOTO_EMULSION
  name = G4_PHOTO_EMULSION
  specific = 4
FEATURE [App::DocumentObjectGroupPython] C_element077  label="C_element : 9"  # scripted group (container) (typed FeaturePython)
  n = 9
  ref = C_element
FEATURE [App::DocumentObjectGroupPython] H_element071  label="H_element : 033"  # scripted group (container) (typed FeaturePython)
  n = 10
  ref = H_element
FEATURE [App::DocumentObjectGroupPython] G4_PLASTIC_SC_VINYLTOLUENE  # scripted group (container) (typed FeaturePython)
  Dunit = g/cm3
  Dvalue = 1.032
  Group = -> [C_element077,H_element071]
  conduct = 2
  density = 1
  expand = 3
  formula = G4_PLASTIC_SC_VINYLTOLUENE
  name = G4_PLASTIC_SC_VINYLTOLUENE
  specific = 4
FEATURE [App::DocumentObjectGroupPython] Pu_element001  label="Pu_element : 1"  # scripted group (container) (typed FeaturePython)
  n = 1
  ref = Pu_element
FEATURE [App::DocumentObjectGroupPython] O_element076  label="O_element : 037"  # scripted group (container) (typed FeaturePython)
  n = 2
  ref = O_element
FEATURE [App::DocumentObjectGroupPython] G4_PLUTONIUM_DIOXIDE  # scripted group (container) (typed FeaturePython)
  Dunit = g/cm3
  Dvalue = 11.46
  Group = -> [Pu_element001,O_element076]
  conduct = 2
  density = 1
  expand = 3
  formula = G4_PLUTONIUM_DIOXIDE
  name = G4_PLUTONIUM_DIOXIDE
  specific = 4
FEATURE [App::DocumentObjectGroupPython] C_element078  label="C_element : 037"  # scripted group (container) (typed FeaturePython)
  n = 3
  ref = C_element
FEATURE [App::DocumentObjectGroupPython] H_element072  label="H_element : 034"  # scripted group (container) (typed FeaturePython)
  n = 3
  ref = H_element
FEATURE [App::DocumentObjectGroupPython] N_element036  label="N_element : 015"  # scripted group (container) (typed FeaturePython)
  n = 1
  ref = N_element
FEATURE [App::DocumentObjectGroupPython] G4_POLYACRYLONITRILE  # scripted group (container) (typed FeaturePython)
  Dunit = g/cm3
  Dvalue = 1.17
  Group = -> [C_element078,H_element072,N_element036]
  conduct = 2
  density = 1
  expand = 3
  formula = G4_POLYACRYLONITRILE
  name = G4_POLYACRYLONITRILE
  specific = 4
FEATURE [App::DocumentObjectGroupPython] C_element079  label="C_element : 16"  # scripted group (container) (typed FeaturePython)
  n = 16
  ref = C_element
FEATURE [App::DocumentObjectGroupPython] H_element073  label="H_element : 035"  # scripted group (container) (typed FeaturePython)
  n = 14
  ref = H_element
FEATURE [App::DocumentObjectGroupPython] O_element077  label="O_element : 038"  # scripted group (container) (typed FeaturePython)
  n = 3
  ref = O_element
FEATURE [App::DocumentObjectGroupPython] G4_POLYCARBONATE  # scripted group (container) (typed FeaturePython)
  Dunit = g/cm3
  Dvalue = 1.2
  Group = -> [C_element079,H_element073,O_element077]
  conduct = 2
  density = 1
  expand = 3
  formula = G4_POLYCARBONATE
  name = G4_POLYCARBONATE
  specific = 4
FEATURE [App::DocumentObjectGroupPython] C_element080  label="C_element : 038"  # scripted group (container) (typed FeaturePython)
  n = 8
  ref = C_element
FEATURE [App::DocumentObjectGroupPython] H_element074  label="H_element : 036"  # scripted group (container) (typed FeaturePython)
  n = 7
  ref = H_element
FEATURE [App::DocumentObjectGroupPython] Cl_element017  label="Cl_element : 007"  # scripted group (container) (typed FeaturePython)
  n = 1
  ref = Cl_element
FEATURE [App::DocumentObjectGroupPython] G4_POLYCHLOROSTYRENE  # scripted group (container) (typed FeaturePython)
  Dunit = g/cm3
  Dvalue = 1.3
  Group = -> [C_element080,H_element074,Cl_element017]
  conduct = 2
  density = 1
  expand = 3
  formula = G4_POLYCHLOROSTYRENE
  name = G4_POLYCHLOROSTYRENE
  specific = 4
FEATURE [App::DocumentObjectGroupPython] C_element081  label="C_element : 039"  # scripted group (container) (typed FeaturePython)
  n = 1
  ref = C_element
FEATURE [App::DocumentObjectGroupPython] H_element075  label="H_element : 037"  # scripted group (container) (typed FeaturePython)
  n = 2
  ref = H_element
FEATURE [App::DocumentObjectGroupPython] G4_POLYETHYLENE  # scripted group (container) (typed FeaturePython)
  Dunit = g/cm3
  Dvalue = 0.94
  Group = -> [C_element081,H_element075]
  conduct = 2
  density = 1
  expand = 3
  formula = G4_POLYETHYLENE
  name = G4_POLYETHYLENE
  specific = 4
FEATURE [App::DocumentObjectGroupPython] C_element082  label="C_element : 040"  # scripted group (container) (typed FeaturePython)
  n = 10
  ref = C_element
FEATURE [App::DocumentObjectGroupPython] H_element076  label="H_element : 038"  # scripted group (container) (typed FeaturePython)
  n = 8
  ref = H_element
FEATURE [App::DocumentObjectGroupPython] O_element078  label="O_element : 039"  # scripted group (container) (typed FeaturePython)
  n = 4
  ref = O_element
FEATURE [App::DocumentObjectGroupPython] G4_MYLAR  # scripted group (container) (typed FeaturePython)
  Dunit = g/cm3
  Dvalue = 1.4
  Group = -> [C_element082,H_element076,O_element078]
  conduct = 2
  density = 1
  expand = 3
  formula = G4_MYLAR
  name = G4_MYLAR
  specific = 4
FEATURE [App::DocumentObjectGroupPython] C_element083  label="C_element : 041"  # scripted group (container) (typed FeaturePython)
  n = 5
  ref = C_element
FEATURE [App::DocumentObjectGroupPython] H_element077  label="H_element : 039"  # scripted group (container) (typed FeaturePython)
  n = 8
  ref = H_element
FEATURE [App::DocumentObjectGroupPython] O_element079  label="O_element : 040"  # scripted group (container) (typed FeaturePython)
  n = 2
  ref = O_element
FEATURE [App::DocumentObjectGroupPython] G4_PLEXIGLASS  # scripted group (container) (typed FeaturePython)
  Dunit = g/cm3
  Dvalue = 1.19
  Group = -> [C_element083,H_element077,O_element079]
  conduct = 2
  density = 1
  expand = 3
  formula = G4_PLEXIGLASS
  name = G4_PLEXIGLASS
  specific = 4
FEATURE [App::DocumentObjectGroupPython] C_element084  label="C_element : 042"  # scripted group (container) (typed FeaturePython)
  n = 1
  ref = C_element
FEATURE [App::DocumentObjectGroupPython] H_element078  label="H_element : 040"  # scripted group (container) (typed FeaturePython)
  n = 2
  ref = H_element
FEATURE [App::DocumentObjectGroupPython] O_element080  label="O_element : 041"  # scripted group (container) (typed FeaturePython)
  n = 1
  ref = O_element
FEATURE [App::DocumentObjectGroupPython] G4_POLYOXYMETHYLENE  # scripted group (container) (typed FeaturePython)
  Dunit = g/cm3
  Dvalue = 1.425
  Group = -> [C_element084,H_element078,O_element080]
  conduct = 2
  density = 1
  expand = 3
  formula = G4_POLYOXYMETHYLENE
  name = G4_POLYOXYMETHYLENE
  specific = 4
FEATURE [App::DocumentObjectGroupPython] C_element085  label="C_element : 043"  # scripted group (container) (typed FeaturePython)
  n = 2
  ref = C_element
FEATURE [App::DocumentObjectGroupPython] H_element079  label="H_element : 041"  # scripted group (container) (typed FeaturePython)
  n = 4
  ref = H_element
FEATURE [App::DocumentObjectGroupPython] G4_POLYPROPYLENE  # scripted group (container) (typed FeaturePython)
  Dunit = g/cm3
  Dvalue = 0.9
  Group = -> [C_element085,H_element079]
  conduct = 2
  density = 1
  expand = 3
  formula = G4_POLYPROPYLENE
  name = G4_POLYPROPYLENE
  specific = 4
FEATURE [App::DocumentObjectGroupPython] C_element086  label="C_element : 044"  # scripted group (container) (typed FeaturePython)
  n = 8
  ref = C_element
FEATURE [App::DocumentObjectGroupPython] H_element080  label="H_element : 042"  # scripted group (container) (typed FeaturePython)
  n = 8
  ref = H_element
FEATURE [App::DocumentObjectGroupPython] G4_POLYSTYRENE  # scripted group (container) (typed FeaturePython)
  Dunit = g/cm3
  Dvalue = 1.06
  Group = -> [C_element086,H_element080]
  conduct = 2
  density = 1
  expand = 3
  formula = G4_POLYSTYRENE
  name = G4_POLYSTYRENE
  specific = 4
FEATURE [App::DocumentObjectGroupPython] C_element087  label="C_element : 045"  # scripted group (container) (typed FeaturePython)
  n = 2
  ref = C_element
FEATURE [App::DocumentObjectGroupPython] F_element014  label="F_element : 4"  # scripted group (container) (typed FeaturePython)
  n = 4
  ref = F_element
FEATURE [App::DocumentObjectGroupPython] G4_TEFLON  # scripted group (container) (typed FeaturePython)
  Dunit = g/cm3
  Dvalue = 2.2
  Group = -> [C_element087,F_element014]
  conduct = 2
  density = 1
  expand = 3
  formula = G4_TEFLON
  name = G4_TEFLON
  specific = 4
FEATURE [App::DocumentObjectGroupPython] C_element088  label="C_element : 046"  # scripted group (container) (typed FeaturePython)
  n = 2
  ref = C_element
FEATURE [App::DocumentObjectGroupPython] F_element015  label="F_element : 006"  # scripted group (container) (typed FeaturePython)
  n = 3
  ref = F_element
FEATURE [App::DocumentObjectGroupPython] Cl_element018  label="Cl_element : 008"  # scripted group (container) (typed FeaturePython)
  n = 1
  ref = Cl_element
FEATURE [App::DocumentObjectGroupPython] G4_POLYTRIFLUOROCHLOROETHYLENE  # scripted group (container) (typed FeaturePython)
  Dunit = g/cm3
  Dvalue = 2.1
  Group = -> [C_element088,F_element015,Cl_element018]
  conduct = 2
  density = 1
  expand = 3
  formula = G4_POLYTRIFLUOROCHLOROETHYLENE
  name = G4_POLYTRIFLUOROCHLOROETHYLENE
  specific = 4
FEATURE [App::DocumentObjectGroupPython] C_element089  label="C_element : 047"  # scripted group (container) (typed FeaturePython)
  n = 4
  ref = C_element
FEATURE [App::DocumentObjectGroupPython] H_element081  label="H_element : 043"  # scripted group (container) (typed FeaturePython)
  n = 6
  ref = H_element
FEATURE [App::DocumentObjectGroupPython] O_element081  label="O_element : 042"  # scripted group (container) (typed FeaturePython)
  n = 2
  ref = O_element
FEATURE [App::DocumentObjectGroupPython] G4_POLYVINYL_ACETATE  # scripted group (container) (typed FeaturePython)
  Dunit = g/cm3
  Dvalue = 1.19
  Group = -> [C_element089,H_element081,O_element081]
  conduct = 2
  density = 1
  expand = 3
  formula = G4_POLYVINYL_ACETATE
  name = G4_POLYVINYL_ACETATE
  specific = 4
FEATURE [App::DocumentObjectGroupPython] C_element090  label="C_element : 048"  # scripted group (container) (typed FeaturePython)
  n = 2
  ref = C_element
FEATURE [App::DocumentObjectGroupPython] H_element082  label="H_element : 044"  # scripted group (container) (typed FeaturePython)
  n = 4
  ref = H_element
FEATURE [App::DocumentObjectGroupPython] O_element082  label="O_element : 043"  # scripted group (container) (typed FeaturePython)
  n = 1
  ref = O_element
FEATURE [App::DocumentObjectGroupPython] G4_POLYVINYL_ALCOHOL  # scripted group (container) (typed FeaturePython)
  Dunit = g/cm3
  Dvalue = 1.3
  Group = -> [C_element090,H_element082,O_element082]
  conduct = 2
  density = 1
  expand = 3
  formula = G4_POLYVINYL_ALCOHOL
  name = G4_POLYVINYL_ALCOHOL
  specific = 4
FEATURE [App::DocumentObjectGroupPython] C_element091  label="C_element : 049"  # scripted group (container) (typed FeaturePython)
  n = 8
  ref = C_element
FEATURE [App::DocumentObjectGroupPython] H_element083  label="H_element : 045"  # scripted group (container) (typed FeaturePython)
  n = 14
  ref = H_element
FEATURE [App::DocumentObjectGroupPython] O_element083  label="O_element : 044"  # scripted group (container) (typed FeaturePython)
  n = 2
  ref = O_element
FEATURE [App::DocumentObjectGroupPython] G4_POLYVINYL_BUTYRAL  # scripted group (container) (typed FeaturePython)
  Dunit = g/cm3
  Dvalue = 1.12
  Group = -> [C_element091,H_element083,O_element083]
  conduct = 2
  density = 1
  expand = 3
  formula = G4_POLYVINYL_BUTYRAL
  name = G4_POLYVINYL_BUTYRAL
  specific = 4
FEATURE [App::DocumentObjectGroupPython] C_element092  label="C_element : 050"  # scripted group (container) (typed FeaturePython)
  n = 2
  ref = C_element
FEATURE [App::DocumentObjectGroupPython] H_element084  label="H_element : 046"  # scripted group (container) (typed FeaturePython)
  n = 3
  ref = H_element
FEATURE [App::DocumentObjectGroupPython] Cl_element019  label="Cl_element : 009"  # scripted group (container) (typed FeaturePython)
  n = 1
  ref = Cl_element
FEATURE [App::DocumentObjectGroupPython] G4_POLYVINYL_CHLORIDE  # scripted group (container) (typed FeaturePython)
  Dunit = g/cm3
  Dvalue = 1.3
  Group = -> [C_element092,H_element084,Cl_element019]
  conduct = 2
  density = 1
  expand = 3
  formula = G4_POLYVINYL_CHLORIDE
  name = G4_POLYVINYL_CHLORIDE
  specific = 4
FEATURE [App::DocumentObjectGroupPython] C_element093  label="C_element : 051"  # scripted group (container) (typed FeaturePython)
  n = 2
  ref = C_element
FEATURE [App::DocumentObjectGroupPython] H_element085  label="H_element : 047"  # scripted group (container) (typed FeaturePython)
  n = 2
  ref = H_element
FEATURE [App::DocumentObjectGroupPython] Cl_element020  label="Cl_element : 010"  # scripted group (container) (typed FeaturePython)
  n = 2
  ref = Cl_element
FEATURE [App::DocumentObjectGroupPython] G4_POLYVINYLIDENE_CHLORIDE  # scripted group (container) (typed FeaturePython)
  Dunit = g/cm3
  Dvalue = 1.7
  Group = -> [C_element093,H_element085,Cl_element020]
  conduct = 2
  density = 1
  expand = 3
  formula = G4_POLYVINYLIDENE_CHLORIDE
  name = G4_POLYVINYLIDENE_CHLORIDE
  specific = 4
FEATURE [App::DocumentObjectGroupPython] C_element094  label="C_element : 052"  # scripted group (container) (typed FeaturePython)
  n = 2
  ref = C_element
FEATURE [App::DocumentObjectGroupPython] H_element086  label="H_element : 048"  # scripted group (container) (typed FeaturePython)
  n = 2
  ref = H_element
FEATURE [App::DocumentObjectGroupPython] F_element016  label="F_element : 007"  # scripted group (container) (typed FeaturePython)
  n = 2
  ref = F_element
FEATURE [App::DocumentObjectGroupPython] G4_POLYVINYLIDENE_FLUORIDE  # scripted group (container) (typed FeaturePython)
  Dunit = g/cm3
  Dvalue = 1.76
  Group = -> [C_element094,H_element086,F_element016]
  conduct = 2
  density = 1
  expand = 3
  formula = G4_POLYVINYLIDENE_FLUORIDE
  name = G4_POLYVINYLIDENE_FLUORIDE
  specific = 4
FEATURE [App::DocumentObjectGroupPython] C_element095  label="C_element : 053"  # scripted group (container) (typed FeaturePython)
  n = 6
  ref = C_element
FEATURE [App::DocumentObjectGroupPython] H_element087  label="H_element : 9"  # scripted group (container) (typed FeaturePython)
  n = 9
  ref = H_element
FEATURE [App::DocumentObjectGroupPython] N_element037  label="N_element : 016"  # scripted group (container) (typed FeaturePython)
  n = 1
  ref = N_element
FEATURE [App::DocumentObjectGroupPython] O_element084  label="O_element : 045"  # scripted group (container) (typed FeaturePython)
  n = 1
  ref = O_element
FEATURE [App::DocumentObjectGroupPython] G4_POLYVINYL_PYRROLIDONE  # scripted group (container) (typed FeaturePython)
  Dunit = g/cm3
  Dvalue = 1.25
  Group = -> [C_element095,H_element087,N_element037,O_element084]
  conduct = 2
  density = 1
  expand = 3
  formula = G4_POLYVINYL_PYRROLIDONE
  name = G4_POLYVINYL_PYRROLIDONE
  specific = 4
FEATURE [App::DocumentObjectGroupPython] K_element008  label="K_element : 1"  # scripted group (container) (typed FeaturePython)
  n = 1
  ref = K_element
FEATURE [App::DocumentObjectGroupPython] I_element006  label="I_element : 003"  # scripted group (container) (typed FeaturePython)
  n = 1
  ref = I_element
FEATURE [App::DocumentObjectGroupPython] G4_POTASSIUM_IODIDE  # scripted group (container) (typed FeaturePython)
  Dunit = g/cm3
  Dvalue = 3.13
  Group = -> [K_element008,I_element006]
  conduct = 2
  density = 1
  expand = 3
  formula = G4_POTASSIUM_IODIDE
  name = G4_POTASSIUM_IODIDE
  specific = 4
FEATURE [App::DocumentObjectGroupPython] K_element009  label="K_element : 2"  # scripted group (container) (typed FeaturePython)
  n = 2
  ref = K_element
FEATURE [App::DocumentObjectGroupPython] O_element085  label="O_element : 046"  # scripted group (container) (typed FeaturePython)
  n = 1
  ref = O_element
FEATURE [App::DocumentObjectGroupPython] G4_POTASSIUM_OXIDE  # scripted group (container) (typed FeaturePython)
  Dunit = g/cm3
  Dvalue = 2.32
  Group = -> [K_element009,O_element085]
  conduct = 2
  density = 1
  expand = 3
  formula = G4_POTASSIUM_OXIDE
  name = G4_POTASSIUM_OXIDE
  specific = 4
FEATURE [App::DocumentObjectGroupPython] C_element096  label="C_element : 054"  # scripted group (container) (typed FeaturePython)
  n = 3
  ref = C_element
FEATURE [App::DocumentObjectGroupPython] H_element088  label="H_element : 049"  # scripted group (container) (typed FeaturePython)
  n = 8
  ref = H_element
FEATURE [App::DocumentObjectGroupPython] G4_PROPANE  # scripted group (container) (typed FeaturePython)
  Dunit = g/cm3
  Dvalue = 0.00187939
  Group = -> [C_element096,H_element088]
  conduct = 2
  density = 1
  expand = 3
  formula = G4_PROPANE
  name = G4_PROPANE
  specific = 4
FEATURE [App::DocumentObjectGroupPython] C_element097  label="C_element : 055"  # scripted group (container) (typed FeaturePython)
  n = 3
  ref = C_element
FEATURE [App::DocumentObjectGroupPython] H_element089  label="H_element : 050"  # scripted group (container) (typed FeaturePython)
  n = 8
  ref = H_element
FEATURE [App::DocumentObjectGroupPython] G4_lPROPANE  # scripted group (container) (typed FeaturePython)
  Dunit = g/cm3
  Dvalue = 0.43
  Group = -> [C_element097,H_element089]
  conduct = 2
  density = 1
  expand = 3
  formula = G4_lPROPANE
  name = G4_lPROPANE
  specific = 4
FEATURE [App::DocumentObjectGroupPython] C_element098  label="C_element : 056"  # scripted group (container) (typed FeaturePython)
  n = 3
  ref = C_element
FEATURE [App::DocumentObjectGroupPython] H_element090  label="H_element : 051"  # scripted group (container) (typed FeaturePython)
  n = 8
  ref = H_element
FEATURE [App::DocumentObjectGroupPython] O_element086  label="O_element : 047"  # scripted group (container) (typed FeaturePython)
  n = 1
  ref = O_element
FEATURE [App::DocumentObjectGroupPython] G4_N_PROPYL_ALCOHOL  label="G4_N-PROPYL_ALCOHOL"  # scripted group (container) (typed FeaturePython)
  Dunit = g/cm3
  Dvalue = 0.8035
  Group = -> [C_element098,H_element090,O_element086]
  conduct = 2
  density = 1
  expand = 3
  formula = G4_N-PROPYL_ALCOHOL
  name = G4_N-PROPYL_ALCOHOL
  specific = 4
FEATURE [App::DocumentObjectGroupPython] C_element099  label="C_element : 057"  # scripted group (container) (typed FeaturePython)
  n = 5
  ref = C_element
FEATURE [App::DocumentObjectGroupPython] H_element091  label="H_element : 052"  # scripted group (container) (typed FeaturePython)
  n = 5
  ref = H_element
FEATURE [App::DocumentObjectGroupPython] N_element038  label="N_element : 017"  # scripted group (container) (typed FeaturePython)
  n = 1
  ref = N_element
FEATURE [App::DocumentObjectGroupPython] G4_PYRIDINE  # scripted group (container) (typed FeaturePython)
  Dunit = g/cm3
  Dvalue = 0.9819
  Group = -> [C_element099,H_element091,N_element038]
  conduct = 2
  density = 1
  expand = 3
  formula = G4_PYRIDINE
  name = G4_PYRIDINE
  specific = 4
FEATURE [App::DocumentObjectGroupPython] H_element092  label="H_element : 0.144"  # scripted group (container) (typed FeaturePython)
  n = 0.143711
FEATURE [App::DocumentObjectGroupPython] C_element100  label="C_element : 0.856"  # scripted group (container) (typed FeaturePython)
  n = 0.856289
FEATURE [App::DocumentObjectGroupPython] G4_RUBBER_BUTYL  # scripted group (container) (typed FeaturePython)
  Dunit = g/cm3
  Dvalue = 0.92
  Group = -> [H_element092,C_element100]
  conduct = 2
  density = 1
  expand = 3
  formula = G4_RUBBER_BUTYL
  name = G4_RUBBER_BUTYL
  specific = 4
FEATURE [App::DocumentObjectGroupPython] H_element093  label="H_element : 0.118"  # scripted group (container) (typed FeaturePython)
  n = 0.118371
FEATURE [App::DocumentObjectGroupPython] C_element101  label="C_element : 0.882"  # scripted group (container) (typed FeaturePython)
  n = 0.881629
FEATURE [App::DocumentObjectGroupPython] G4_RUBBER_NATURAL  # scripted group (container) (typed FeaturePython)
  Dunit = g/cm3
  Dvalue = 0.92
  Group = -> [H_element093,C_element101]
  conduct = 2
  density = 1
  expand = 3
  formula = G4_RUBBER_NATURAL
  name = G4_RUBBER_NATURAL
  specific = 4
FEATURE [App::DocumentObjectGroupPython] H_element094  label="H_element : 0.145"  # scripted group (container) (typed FeaturePython)
  n = 0.05692
FEATURE [App::DocumentObjectGroupPython] C_element102  label="C_element : 0.543"  # scripted group (container) (typed FeaturePython)
  n = 0.542646
FEATURE [App::DocumentObjectGroupPython] Cl_element021  label="Cl_element : 0.400"  # scripted group (container) (typed FeaturePython)
  n = 0.400434
FEATURE [App::DocumentObjectGroupPython] G4_RUBBER_NEOPRENE  # scripted group (container) (typed FeaturePython)
  Dunit = g/cm3
  Dvalue = 1.23
  Group = -> [H_element094,C_element102,Cl_element021]
  conduct = 2
  density = 1
  expand = 3
  formula = G4_RUBBER_NEOPRENE
  name = G4_RUBBER_NEOPRENE
  specific = 4
FEATURE [App::DocumentObjectGroupPython] Si_element006  label="Si_element : 1"  # scripted group (container) (typed FeaturePython)
  n = 1
  ref = Si_element
FEATURE [App::DocumentObjectGroupPython] O_element087  label="O_element : 048"  # scripted group (container) (typed FeaturePython)
  n = 2
  ref = O_element
FEATURE [App::DocumentObjectGroupPython] G4_SILICON_DIOXIDE  # scripted group (container) (typed FeaturePython)
  Dunit = g/cm3
  Dvalue = 2.32
  Group = -> [Si_element006,O_element087]
  conduct = 2
  density = 1
  expand = 3
  formula = G4_SILICON_DIOXIDE
  name = G4_SILICON_DIOXIDE
  specific = 4
FEATURE [App::DocumentObjectGroupPython] Ag_element002  label="Ag_element : 1"  # scripted group (container) (typed FeaturePython)
  n = 1
  ref = Ag_element
FEATURE [App::DocumentObjectGroupPython] Br_element005  label="Br_element : 003"  # scripted group (container) (typed FeaturePython)
  n = 1
  ref = Br_element
FEATURE [App::DocumentObjectGroupPython] G4_SILVER_BROMIDE  # scripted group (container) (typed FeaturePython)
  Dunit = g/cm3
  Dvalue = 6.473
  Group = -> [Ag_element002,Br_element005]
  conduct = 2
  density = 1
  expand = 3
  formula = G4_SILVER_BROMIDE
  name = G4_SILVER_BROMIDE
  specific = 4
FEATURE [App::DocumentObjectGroupPython] Ag_element003  label="Ag_element : 002"  # scripted group (container) (typed FeaturePython)
  n = 1
  ref = Ag_element
FEATURE [App::DocumentObjectGroupPython] Cl_element022  label="Cl_element : 011"  # scripted group (container) (typed FeaturePython)
  n = 1
  ref = Cl_element
FEATURE [App::DocumentObjectGroupPython] G4_SILVER_CHLORIDE  # scripted group (container) (typed FeaturePython)
  Dunit = g/cm3
  Dvalue = 5.56
  Group = -> [Ag_element003,Cl_element022]
  conduct = 2
  density = 1
  expand = 3
  formula = G4_SILVER_CHLORIDE
  name = G4_SILVER_CHLORIDE
  specific = 4
FEATURE [App::DocumentObjectGroupPython] Br_element006  label="Br_element : 0.423"  # scripted group (container) (typed FeaturePython)
  n = 0.422895
FEATURE [App::DocumentObjectGroupPython] Ag_element004  label="Ag_element : 0.574"  # scripted group (container) (typed FeaturePython)
  n = 0.573748
FEATURE [App::DocumentObjectGroupPython] I_element007  label="I_element : 0.649"  # scripted group (container) (typed FeaturePython)
  n = 0.003357
FEATURE [App::DocumentObjectGroupPython] G4_SILVER_HALIDES  # scripted group (container) (typed FeaturePython)
  Dunit = g/cm3
  Dvalue = 6.47
  Group = -> [Br_element006,Ag_element004,I_element007]
  conduct = 2
  density = 1
  expand = 3
  formula = G4_SILVER_HALIDES
  name = G4_SILVER_HALIDES
  specific = 4
FEATURE [App::DocumentObjectGroupPython] Ag_element005  label="Ag_element : 003"  # scripted group (container) (typed FeaturePython)
  n = 1
  ref = Ag_element
FEATURE [App::DocumentObjectGroupPython] I_element008  label="I_element : 004"  # scripted group (container) (typed FeaturePython)
  n = 1
  ref = I_element
FEATURE [App::DocumentObjectGroupPython] G4_SILVER_IODIDE  # scripted group (container) (typed FeaturePython)
  Dunit = g/cm3
  Dvalue = 6.01
  Group = -> [Ag_element005,I_element008]
  conduct = 2
  density = 1
  expand = 3
  formula = G4_SILVER_IODIDE
  name = G4_SILVER_IODIDE
  specific = 4
FEATURE [App::DocumentObjectGroupPython] H_element095  label="H_element : 0.100"  # scripted group (container) (typed FeaturePython)
  n = 0.1
FEATURE [App::DocumentObjectGroupPython] C_element103  label="C_element : 0.204"  # scripted group (container) (typed FeaturePython)
  n = 0.204
FEATURE [App::DocumentObjectGroupPython] N_element039  label="N_element : 0.759"  # scripted group (container) (typed FeaturePython)
  n = 0.042
FEATURE [App::DocumentObjectGroupPython] O_element088  label="O_element : 0.645"  # scripted group (container) (typed FeaturePython)
  n = 0.645
FEATURE [App::DocumentObjectGroupPython] Na_element013  label="Na_element : 0.100"  # scripted group (container) (typed FeaturePython)
  n = 0.002
FEATURE [App::DocumentObjectGroupPython] P_element009  label="P_element : 0.107"  # scripted group (container) (typed FeaturePython)
  n = 0.001
FEATURE [App::DocumentObjectGroupPython] S_element020  label="S_element : 0.021"  # scripted group (container) (typed FeaturePython)
  n = 0.002
FEATURE [App::DocumentObjectGroupPython] Cl_element023  label="Cl_element : 0.590"  # scripted group (container) (typed FeaturePython)
  n = 0.003
FEATURE [App::DocumentObjectGroupPython] K_element010  label="K_element : 0.001"  # scripted group (container) (typed FeaturePython)
  n = 0.001
FEATURE [App::DocumentObjectGroupPython] G4_SKIN_ICRP  # scripted group (container) (typed FeaturePython)
  Dunit = g/cm3
  Dvalue = 1.09
  Group = -> [H_element095,C_element103,N_element039,O_element088,Na_element013,P_element009,S_element020,Cl_element023,K_element010]
  conduct = 2
  density = 1
  expand = 3
  formula = G4_SKIN_ICRP
  name = G4_SKIN_ICRP
  specific = 4
FEATURE [App::DocumentObjectGroupPython] Na_element014  label="Na_element : 2"  # scripted group (container) (typed FeaturePython)
  n = 2
  ref = Na_element
FEATURE [App::DocumentObjectGroupPython] C_element104  label="C_element : 058"  # scripted group (container) (typed FeaturePython)
  n = 1
  ref = C_element
FEATURE [App::DocumentObjectGroupPython] O_element089  label="O_element : 049"  # scripted group (container) (typed FeaturePython)
  n = 3
  ref = O_element
FEATURE [App::DocumentObjectGroupPython] G4_SODIUM_CARBONATE  # scripted group (container) (typed FeaturePython)
  Dunit = g/cm3
  Dvalue = 2.532
  Group = -> [Na_element014,C_element104,O_element089]
  conduct = 2
  density = 1
  expand = 3
  formula = G4_SODIUM_CARBONATE
  name = G4_SODIUM_CARBONATE
  specific = 4
FEATURE [App::DocumentObjectGroupPython] Na_element015  label="Na_element : 1"  # scripted group (container) (typed FeaturePython)
  n = 1
  ref = Na_element
FEATURE [App::DocumentObjectGroupPython] I_element009  label="I_element : 005"  # scripted group (container) (typed FeaturePython)
  n = 1
  ref = I_element
FEATURE [App::DocumentObjectGroupPython] G4_SODIUM_IODIDE  # scripted group (container) (typed FeaturePython)
  Dunit = g/cm3
  Dvalue = 3.667
  Group = -> [Na_element015,I_element009]
  conduct = 2
  density = 1
  expand = 3
  formula = G4_SODIUM_IODIDE
  name = G4_SODIUM_IODIDE
  specific = 4
FEATURE [App::DocumentObjectGroupPython] Na_element016  label="Na_element : 003"  # scripted group (container) (typed FeaturePython)
  n = 2
  ref = Na_element
FEATURE [App::DocumentObjectGroupPython] O_element090  label="O_element : 050"  # scripted group (container) (typed FeaturePython)
  n = 1
  ref = O_element
FEATURE [App::DocumentObjectGroupPython] G4_SODIUM_MONOXIDE  # scripted group (container) (typed FeaturePython)
  Dunit = g/cm3
  Dvalue = 2.27
  Group = -> [Na_element016,O_element090]
  conduct = 2
  density = 1
  expand = 3
  formula = G4_SODIUM_MONOXIDE
  name = G4_SODIUM_MONOXIDE
  specific = 4
FEATURE [App::DocumentObjectGroupPython] Na_element017  label="Na_element : 004"  # scripted group (container) (typed FeaturePython)
  n = 1
  ref = Na_element
FEATURE [App::DocumentObjectGroupPython] N_element040  label="N_element : 018"  # scripted group (container) (typed FeaturePython)
  n = 1
  ref = N_element
FEATURE [App::DocumentObjectGroupPython] O_element091  label="O_element : 051"  # scripted group (container) (typed FeaturePython)
  n = 3
  ref = O_element
FEATURE [App::DocumentObjectGroupPython] G4_SODIUM_NITRATE  # scripted group (container) (typed FeaturePython)
  Dunit = g/cm3
  Dvalue = 2.261
  Group = -> [Na_element017,N_element040,O_element091]
  conduct = 2
  density = 1
  expand = 3
  formula = G4_SODIUM_NITRATE
  name = G4_SODIUM_NITRATE
  specific = 4
FEATURE [App::DocumentObjectGroupPython] C_element105  label="C_element : 059"  # scripted group (container) (typed FeaturePython)
  n = 14
  ref = C_element
FEATURE [App::DocumentObjectGroupPython] H_element096  label="H_element : 053"  # scripted group (container) (typed FeaturePython)
  n = 12
  ref = H_element
FEATURE [App::DocumentObjectGroupPython] G4_STILBENE  # scripted group (container) (typed FeaturePython)
  Dunit = g/cm3
  Dvalue = 0.9707
  Group = -> [C_element105,H_element096]
  conduct = 2
  density = 1
  expand = 3
  formula = G4_STILBENE
  name = G4_STILBENE
  specific = 4
FEATURE [App::DocumentObjectGroupPython] C_element106  label="C_element : 12"  # scripted group (container) (typed FeaturePython)
  n = 12
  ref = C_element
FEATURE [App::DocumentObjectGroupPython] H_element097  label="H_element : 22"  # scripted group (container) (typed FeaturePython)
  n = 22
  ref = H_element
FEATURE [App::DocumentObjectGroupPython] O_element092  label="O_element : 11"  # scripted group (container) (typed FeaturePython)
  n = 11
  ref = O_element
FEATURE [App::DocumentObjectGroupPython] G4_SUCROSE  # scripted group (container) (typed FeaturePython)
  Dunit = g/cm3
  Dvalue = 1.5805
  Group = -> [C_element106,H_element097,O_element092]
  conduct = 2
  density = 1
  expand = 3
  formula = G4_SUCROSE
  name = G4_SUCROSE
  specific = 4
FEATURE [App::DocumentObjectGroupPython] C_element107  label="C_element : 18"  # scripted group (container) (typed FeaturePython)
  n = 18
  ref = C_element
FEATURE [App::DocumentObjectGroupPython] H_element098  label="H_element : 054"  # scripted group (container) (typed FeaturePython)
  n = 14
  ref = H_element
FEATURE [App::DocumentObjectGroupPython] G4_TERPHENYL  # scripted group (container) (typed FeaturePython)
  Dunit = g/cm3
  Dvalue = 1.24
  Group = -> [C_element107,H_element098]
  conduct = 2
  density = 1
  expand = 3
  formula = G4_TERPHENYL
  name = G4_TERPHENYL
  specific = 4
FEATURE [App::DocumentObjectGroupPython] H_element099  label="H_element : 0.146"  # scripted group (container) (typed FeaturePython)
  n = 0.106
FEATURE [App::DocumentObjectGroupPython] C_element108  label="C_element : 0.883"  # scripted group (container) (typed FeaturePython)
  n = 0.099
FEATURE [App::DocumentObjectGroupPython] N_element041  label="N_element : 0.020"  # scripted group (container) (typed FeaturePython)
  n = 0.02
FEATURE [App::DocumentObjectGroupPython] O_element093  label="O_element : 0.766"  # scripted group (container) (typed FeaturePython)
  n = 0.766
FEATURE [App::DocumentObjectGroupPython] Na_element018  label="Na_element : 0.101"  # scripted group (container) (typed FeaturePython)
  n = 0.002
FEATURE [App::DocumentObjectGroupPython] P_element010  label="P_element : 0.108"  # scripted group (container) (typed FeaturePython)
  n = 0.001
FEATURE [App::DocumentObjectGroupPython] S_element021  label="S_element : 0.022"  # scripted group (container) (typed FeaturePython)
  n = 0.002
FEATURE [App::DocumentObjectGroupPython] Cl_element024  label="Cl_element : 0.002"  # scripted group (container) (typed FeaturePython)
  n = 0.002
FEATURE [App::DocumentObjectGroupPython] K_element011  label="K_element : 0.017"  # scripted group (container) (typed FeaturePython)
  n = 0.002
FEATURE [App::DocumentObjectGroupPython] G4_TESTIS_ICRP  # scripted group (container) (typed FeaturePython)
  Dunit = g/cm3
  Dvalue = 1.04
  Group = -> [H_element099,C_element108,N_element041,O_element093,Na_element018,P_element010,S_element021,Cl_element024,K_element011]
  conduct = 2
  density = 1
  expand = 3
  formula = G4_TESTIS_ICRP
  name = G4_TESTIS_ICRP
  specific = 4
FEATURE [App::DocumentObjectGroupPython] C_element109  label="C_element : 060"  # scripted group (container) (typed FeaturePython)
  n = 2
  ref = C_element
FEATURE [App::DocumentObjectGroupPython] Cl_element025  label="Cl_element : 012"  # scripted group (container) (typed FeaturePython)
  n = 4
  ref = Cl_element
FEATURE [App::DocumentObjectGroupPython] G4_TETRACHLOROETHYLENE  # scripted group (container) (typed FeaturePython)
  Dunit = g/cm3
  Dvalue = 1.625
  Group = -> [C_element109,Cl_element025]
  conduct = 2
  density = 1
  expand = 3
  formula = G4_TETRACHLOROETHYLENE
  name = G4_TETRACHLOROETHYLENE
  specific = 4
FEATURE [App::DocumentObjectGroupPython] Tl_element001  label="Tl_element : 1"  # scripted group (container) (typed FeaturePython)
  n = 1
  ref = Tl_element
FEATURE [App::DocumentObjectGroupPython] Cl_element026  label="Cl_element : 013"  # scripted group (container) (typed FeaturePython)
  n = 1
  ref = Cl_element
FEATURE [App::DocumentObjectGroupPython] G4_THALLIUM_CHLORIDE  # scripted group (container) (typed FeaturePython)
  Dunit = g/cm3
  Dvalue = 7.004
  Group = -> [Tl_element001,Cl_element026]
  conduct = 2
  density = 1
  expand = 3
  formula = G4_THALLIUM_CHLORIDE
  name = G4_THALLIUM_CHLORIDE
  specific = 4
FEATURE [App::DocumentObjectGroupPython] H_element100  label="H_element : 0.147"  # scripted group (container) (typed FeaturePython)
  n = 0.105
FEATURE [App::DocumentObjectGroupPython] C_element110  label="C_element : 0.256"  # scripted group (container) (typed FeaturePython)
  n = 0.256
FEATURE [App::DocumentObjectGroupPython] N_element042  label="N_element : 0.760"  # scripted group (container) (typed FeaturePython)
  n = 0.027
FEATURE [App::DocumentObjectGroupPython] O_element094  label="O_element : 0.602"  # scripted group (container) (typed FeaturePython)
  n = 0.602
FEATURE [App::DocumentObjectGroupPython] Na_element019  label="Na_element : 0.102"  # scripted group (container) (typed FeaturePython)
  n = 0.001
FEATURE [App::DocumentObjectGroupPython] P_element011  label="P_element : 0.109"  # scripted group (container) (typed FeaturePython)
  n = 0.002
FEATURE [App::DocumentObjectGroupPython] S_element022  label="S_element : 0.023"  # scripted group (container) (typed FeaturePython)
  n = 0.003
FEATURE [App::DocumentObjectGroupPython] Cl_element027  label="Cl_element : 0.591"  # scripted group (container) (typed FeaturePython)
  n = 0.002
FEATURE [App::DocumentObjectGroupPython] K_element012  label="K_element : 0.018"  # scripted group (container) (typed FeaturePython)
  n = 0.002
FEATURE [App::DocumentObjectGroupPython] G4_TISSUE_SOFT_ICRP  # scripted group (container) (typed FeaturePython)
  Dunit = g/cm3
  Dvalue = 1.03
  Group = -> [H_element100,C_element110,N_element042,O_element094,Na_element019,P_element011,S_element022,Cl_element027,K_element012]
  conduct = 2
  density = 1
  expand = 3
  formula = G4_TISSUE_SOFT_ICRP
  name = G4_TISSUE_SOFT_ICRP
  specific = 4
FEATURE [App::DocumentObjectGroupPython] H_element101  label="H_element : 0.148"  # scripted group (container) (typed FeaturePython)
  n = 0.101
FEATURE [App::DocumentObjectGroupPython] C_element111  label="C_element : 0.111"  # scripted group (container) (typed FeaturePython)
  n = 0.111
FEATURE [App::DocumentObjectGroupPython] N_element043  label="N_element : 0.026"  # scripted group (container) (typed FeaturePython)
  n = 0.026
FEATURE [App::DocumentObjectGroupPython] O_element095  label="O_element : 0.762"  # scripted group (container) (typed FeaturePython)
  n = 0.762
FEATURE [App::DocumentObjectGroupPython] G4_TISSUE_SOFT_ICRU_4  label="G4_TISSUE_SOFT_ICRU-4"  # scripted group (container) (typed FeaturePython)
  Dunit = g/cm3
  Dvalue = 1
  Group = -> [H_element101,C_element111,N_element043,O_element095]
  conduct = 2
  density = 1
  expand = 3
  formula = G4_TISSUE_SOFT_ICRU-4
  name = G4_TISSUE_SOFT_ICRU-4
  specific = 4
FEATURE [App::DocumentObjectGroupPython] H_element102  label="H_element : 0.149"  # scripted group (container) (typed FeaturePython)
  n = 0.101869
FEATURE [App::DocumentObjectGroupPython] C_element112  label="C_element : 0.456"  # scripted group (container) (typed FeaturePython)
  n = 0.456179
FEATURE [App::DocumentObjectGroupPython] N_element044  label="N_element : 0.761"  # scripted group (container) (typed FeaturePython)
  n = 0.035172
FEATURE [App::DocumentObjectGroupPython] O_element096  label="O_element : 0.407"  # scripted group (container) (typed FeaturePython)
  n = 0.40678
FEATURE [App::DocumentObjectGroupPython] G4_TISSUE_METHANE  label="G4_TISSUE-METHANE"  # scripted group (container) (typed FeaturePython)
  Dunit = g/cm3
  Dvalue = 0.00106409
  Group = -> [H_element102,C_element112,N_element044,O_element096]
  conduct = 2
  density = 1
  expand = 3
  formula = G4_TISSUE-METHANE
  name = G4_TISSUE-METHANE
  specific = 4
FEATURE [App::DocumentObjectGroupPython] H_element103  label="H_element : 0.103"  # scripted group (container) (typed FeaturePython)
  n = 0.102672
FEATURE [App::DocumentObjectGroupPython] C_element113  label="C_element : 0.569"  # scripted group (container) (typed FeaturePython)
  n = 0.56894
FEATURE [App::DocumentObjectGroupPython] N_element045  label="N_element : 0.762"  # scripted group (container) (typed FeaturePython)
  n = 0.035022
FEATURE [App::DocumentObjectGroupPython] O_element097  label="O_element : 0.293"  # scripted group (container) (typed FeaturePython)
  n = 0.293366
FEATURE [App::DocumentObjectGroupPython] G4_TISSUE_PROPANE  label="G4_TISSUE-PROPANE"  # scripted group (container) (typed FeaturePython)
  Dunit = g/cm3
  Dvalue = 0.00182628
  Group = -> [H_element103,C_element113,N_element045,O_element097]
  conduct = 2
  density = 1
  expand = 3
  formula = G4_TISSUE-PROPANE
  name = G4_TISSUE-PROPANE
  specific = 4
FEATURE [App::DocumentObjectGroupPython] Ti_element003  label="Ti_element : 1"  # scripted group (container) (typed FeaturePython)
  n = 1
  ref = Ti_element
FEATURE [App::DocumentObjectGroupPython] O_element098  label="O_element : 052"  # scripted group (container) (typed FeaturePython)
  n = 2
  ref = O_element
FEATURE [App::DocumentObjectGroupPython] G4_TITANIUM_DIOXIDE  # scripted group (container) (typed FeaturePython)
  Dunit = g/cm3
  Dvalue = 4.26
  Group = -> [Ti_element003,O_element098]
  conduct = 2
  density = 1
  expand = 3
  formula = G4_TITANIUM_DIOXIDE
  name = G4_TITANIUM_DIOXIDE
  specific = 4
FEATURE [App::DocumentObjectGroupPython] C_element114  label="C_element : 061"  # scripted group (container) (typed FeaturePython)
  n = 7
  ref = C_element
FEATURE [App::DocumentObjectGroupPython] H_element104  label="H_element : 055"  # scripted group (container) (typed FeaturePython)
  n = 8
  ref = H_element
FEATURE [App::DocumentObjectGroupPython] G4_TOLUENE  # scripted group (container) (typed FeaturePython)
  Dunit = g/cm3
  Dvalue = 0.8669
  Group = -> [C_element114,H_element104]
  conduct = 2
  density = 1
  expand = 3
  formula = G4_TOLUENE
  name = G4_TOLUENE
  specific = 4
FEATURE [App::DocumentObjectGroupPython] C_element115  label="C_element : 062"  # scripted group (container) (typed FeaturePython)
  n = 2
  ref = C_element
FEATURE [App::DocumentObjectGroupPython] H_element105  label="H_element : 056"  # scripted group (container) (typed FeaturePython)
  n = 1
  ref = H_element
FEATURE [App::DocumentObjectGroupPython] Cl_element028  label="Cl_element : 014"  # scripted group (container) (typed FeaturePython)
  n = 3
  ref = Cl_element
FEATURE [App::DocumentObjectGroupPython] G4_TRICHLOROETHYLENE  # scripted group (container) (typed FeaturePython)
  Dunit = g/cm3
  Dvalue = 1.46
  Group = -> [C_element115,H_element105,Cl_element028]
  conduct = 2
  density = 1
  expand = 3
  formula = G4_TRICHLOROETHYLENE
  name = G4_TRICHLOROETHYLENE
  specific = 4
FEATURE [App::DocumentObjectGroupPython] C_element116  label="C_element : 063"  # scripted group (container) (typed FeaturePython)
  n = 6
  ref = C_element
FEATURE [App::DocumentObjectGroupPython] H_element106  label="H_element : 15"  # scripted group (container) (typed FeaturePython)
  n = 15
  ref = H_element
FEATURE [App::DocumentObjectGroupPython] O_element099  label="O_element : 053"  # scripted group (container) (typed FeaturePython)
  n = 4
  ref = O_element
FEATURE [App::DocumentObjectGroupPython] P_element012  label="P_element : 1"  # scripted group (container) (typed FeaturePython)
  n = 1
  ref = P_element
FEATURE [App::DocumentObjectGroupPython] G4_TRIETHYL_PHOSPHATE  # scripted group (container) (typed FeaturePython)
  Dunit = g/cm3
  Dvalue = 1.07
  Group = -> [C_element116,H_element106,O_element099,P_element012]
  conduct = 2
  density = 1
  expand = 3
  formula = G4_TRIETHYL_PHOSPHATE
  name = G4_TRIETHYL_PHOSPHATE
  specific = 4
FEATURE [App::DocumentObjectGroupPython] W_element003  label="W_element : 003"  # scripted group (container) (typed FeaturePython)
  n = 1
  ref = W_element
FEATURE [App::DocumentObjectGroupPython] F_element017  label="F_element : 6"  # scripted group (container) (typed FeaturePython)
  n = 6
  ref = F_element
FEATURE [App::DocumentObjectGroupPython] G4_TUNGSTEN_HEXAFLUORIDE  # scripted group (container) (typed FeaturePython)
  Dunit = g/cm3
  Dvalue = 2.4
  Group = -> [W_element003,F_element017]
  conduct = 2
  density = 1
  expand = 3
  formula = G4_TUNGSTEN_HEXAFLUORIDE
  name = G4_TUNGSTEN_HEXAFLUORIDE
  specific = 4
FEATURE [App::DocumentObjectGroupPython] U_element001  label="U_element : 1"  # scripted group (container) (typed FeaturePython)
  n = 1
  ref = U_element
FEATURE [App::DocumentObjectGroupPython] C_element117  label="C_element : 064"  # scripted group (container) (typed FeaturePython)
  n = 2
  ref = C_element
FEATURE [App::DocumentObjectGroupPython] G4_URANIUM_DICARBIDE  # scripted group (container) (typed FeaturePython)
  Dunit = g/cm3
  Dvalue = 11.28
  Group = -> [U_element001,C_element117]
  conduct = 2
  density = 1
  expand = 3
  formula = G4_URANIUM_DICARBIDE
  name = G4_URANIUM_DICARBIDE
  specific = 4
FEATURE [App::DocumentObjectGroupPython] U_element002  label="U_element : 002"  # scripted group (container) (typed FeaturePython)
  n = 1
  ref = U_element
FEATURE [App::DocumentObjectGroupPython] C_element118  label="C_element : 065"  # scripted group (container) (typed FeaturePython)
  n = 1
  ref = C_element
FEATURE [App::DocumentObjectGroupPython] G4_URANIUM_MONOCARBIDE  # scripted group (container) (typed FeaturePython)
  Dunit = g/cm3
  Dvalue = 13.63
  Group = -> [U_element002,C_element118]
  conduct = 2
  density = 1
  expand = 3
  formula = G4_URANIUM_MONOCARBIDE
  name = G4_URANIUM_MONOCARBIDE
  specific = 4
FEATURE [App::DocumentObjectGroupPython] U_element003  label="U_element : 003"  # scripted group (container) (typed FeaturePython)
  n = 1
  ref = U_element
FEATURE [App::DocumentObjectGroupPython] O_element100  label="O_element : 054"  # scripted group (container) (typed FeaturePython)
  n = 2
  ref = O_element
FEATURE [App::DocumentObjectGroupPython] G4_URANIUM_OXIDE  # scripted group (container) (typed FeaturePython)
  Dunit = g/cm3
  Dvalue = 10.96
  Group = -> [U_element003,O_element100]
  conduct = 2
  density = 1
  expand = 3
  formula = G4_URANIUM_OXIDE
  name = G4_URANIUM_OXIDE
  specific = 4
FEATURE [App::DocumentObjectGroupPython] C_element119  label="C_element : 066"  # scripted group (container) (typed FeaturePython)
  n = 1
  ref = C_element
FEATURE [App::DocumentObjectGroupPython] H_element107  label="H_element : 057"  # scripted group (container) (typed FeaturePython)
  n = 4
  ref = H_element
FEATURE [App::DocumentObjectGroupPython] N_element046  label="N_element : 019"  # scripted group (container) (typed FeaturePython)
  n = 2
  ref = N_element
FEATURE [App::DocumentObjectGroupPython] O_element101  label="O_element : 055"  # scripted group (container) (typed FeaturePython)
  n = 1
  ref = O_element
FEATURE [App::DocumentObjectGroupPython] G4_UREA  # scripted group (container) (typed FeaturePython)
  Dunit = g/cm3
  Dvalue = 1.323
  Group = -> [C_element119,H_element107,N_element046,O_element101]
  conduct = 2
  density = 1
  expand = 3
  formula = G4_UREA
  name = G4_UREA
  specific = 4
FEATURE [App::DocumentObjectGroupPython] C_element120  label="C_element : 067"  # scripted group (container) (typed FeaturePython)
  n = 5
  ref = C_element
FEATURE [App::DocumentObjectGroupPython] H_element108  label="H_element : 058"  # scripted group (container) (typed FeaturePython)
  n = 11
  ref = H_element
FEATURE [App::DocumentObjectGroupPython] N_element047  label="N_element : 020"  # scripted group (container) (typed FeaturePython)
  n = 1
  ref = N_element
FEATURE [App::DocumentObjectGroupPython] O_element102  label="O_element : 056"  # scripted group (container) (typed FeaturePython)
  n = 2
  ref = O_element
FEATURE [App::DocumentObjectGroupPython] G4_VALINE  # scripted group (container) (typed FeaturePython)
  Dunit = g/cm3
  Dvalue = 1.23
  Group = -> [C_element120,H_element108,N_element047,O_element102]
  conduct = 2
  density = 1
  expand = 3
  formula = G4_VALINE
  name = G4_VALINE
  specific = 4
FEATURE [App::DocumentObjectGroupPython] H_element109  label="H_element : 0.009"  # scripted group (container) (typed FeaturePython)
  n = 0.009417
FEATURE [App::DocumentObjectGroupPython] C_element121  label="C_element : 0.281"  # scripted group (container) (typed FeaturePython)
  n = 0.280555
FEATURE [App::DocumentObjectGroupPython] F_element018  label="F_element : 0.710"  # scripted group (container) (typed FeaturePython)
  n = 0.710028
FEATURE [App::DocumentObjectGroupPython] G4_VITON  # scripted group (container) (typed FeaturePython)
  Dunit = g/cm3
  Dvalue = 1.8
  Group = -> [H_element109,C_element121,F_element018]
  conduct = 2
  density = 1
  expand = 3
  formula = G4_VITON
  name = G4_VITON
  specific = 4
FEATURE [App::DocumentObjectGroupPython] H_element110  label="H_element : 059"  # scripted group (container) (typed FeaturePython)
  n = 2
  ref = H_element
FEATURE [App::DocumentObjectGroupPython] O_element103  label="O_element : 057"  # scripted group (container) (typed FeaturePython)
  n = 1
  ref = O_element
FEATURE [App::DocumentObjectGroupPython] G4_WATER  # scripted group (container) (typed FeaturePython)
  Dunit = g/cm3
  Dvalue = 1
  Group = -> [H_element110,O_element103]
  conduct = 2
  density = 1
  expand = 3
  formula = G4_WATER
  name = G4_WATER
  specific = 4
FEATURE [App::DocumentObjectGroupPython] H_element111  label="H_element : 060"  # scripted group (container) (typed FeaturePython)
  n = 2
  ref = H_element
FEATURE [App::DocumentObjectGroupPython] O_element104  label="O_element : 058"  # scripted group (container) (typed FeaturePython)
  n = 1
  ref = O_element
FEATURE [App::DocumentObjectGroupPython] G4_WATER_VAPOR  # scripted group (container) (typed FeaturePython)
  Dunit = g/cm3
  Dvalue = 0.000756182
  Group = -> [H_element111,O_element104]
  conduct = 2
  density = 1
  expand = 3
  formula = G4_WATER_VAPOR
  name = G4_WATER_VAPOR
  specific = 4
FEATURE [App::DocumentObjectGroupPython] C_element122  label="C_element : 068"  # scripted group (container) (typed FeaturePython)
  n = 8
  ref = C_element
FEATURE [App::DocumentObjectGroupPython] H_element112  label="H_element : 061"  # scripted group (container) (typed FeaturePython)
  n = 10
  ref = H_element
FEATURE [App::DocumentObjectGroupPython] G4_XYLENE  # scripted group (container) (typed FeaturePython)
  Dunit = g/cm3
  Dvalue = 0.87
  Group = -> [C_element122,H_element112]
  conduct = 2
  density = 1
  expand = 3
  formula = G4_XYLENE
  name = G4_XYLENE
  specific = 4
FEATURE [App::DocumentObjectGroupPython] C_element123  label="C_element : 069"  # scripted group (container) (typed FeaturePython)
  n = 1
  ref = C_element
FEATURE [App::DocumentObjectGroupPython] G4_GRAPHITE  # scripted group (container) (typed FeaturePython)
  Dunit = g/cm3
  Dvalue = 2.21
  Group = -> [C_element123]
  conduct = 2
  density = 1
  expand = 3
  formula = G4_GRAPHITE
  name = G4_GRAPHITE
  specific = 4
FEATURE [App::DocumentObjectGroupPython] NIST  # scripted group (container) (typed FeaturePython)
  Group = -> [G4_A_150_TISSUE,G4_ACETONE,G4_ACETYLENE,G4_ADENINE,G4_ADIPOSE_TISSUE_ICRP,G4_AIR,G4_ALANINE,G4_ALUMINUM_OXIDE,G4_AMBER,G4_AMMONIA,G4_ANILINE,G4_ANTHRACENE,G4_B_100_BONE,G4_BAKELITE,G4_BARIUM_FLUORIDE,G4_BARIUM_SULFATE,G4_BENZENE,G4_BERYLLIUM_OXIDE,G4_BGO,G4_BLOOD_ICRP,G4_BONE_COMPACT_ICRU,G4_BONE_CORTICAL_ICRP,G4_BORON_CARBIDE,G4_BORON_OXIDE,G4_BRAIN_ICRP,G4_BUTANE,G4_N_BUTYL_ALCOHOL,G4_C_552,+152 more]
FEATURE [App::DocumentObjectGroupPython] H_element113  label="H_element : 062"  # scripted group (container) (typed FeaturePython)
  n = 1
  ref = H_element
FEATURE [App::DocumentObjectGroupPython] G4_H  # scripted group (container) (typed FeaturePython)
  Dunit = g/cm3
  Dvalue = 8.3748e-05
  Group = -> [H_element113]
  conduct = 2
  density = 1
  expand = 3
  formula = H
  name = G4_H
  specific = 4
FEATURE [App::DocumentObjectGroupPython] He_element001  label="He_element : 1"  # scripted group (container) (typed FeaturePython)
  n = 1
  ref = He_element
FEATURE [App::DocumentObjectGroupPython] G4_He  # scripted group (container) (typed FeaturePython)
  Dunit = g/cm3
  Dvalue = 0.000166322
  Group = -> [He_element001]
  conduct = 2
  density = 1
  expand = 3
  formula = He
  name = G4_He
  specific = 4
FEATURE [App::DocumentObjectGroupPython] Li_element008  label="Li_element : 008"  # scripted group (container) (typed FeaturePython)
  n = 1
  ref = Li_element
FEATURE [App::DocumentObjectGroupPython] G4_Li  # scripted group (container) (typed FeaturePython)
  Dunit = g/cm3
  Dvalue = 0.534
  Group = -> [Li_element008]
  conduct = 2
  density = 1
  expand = 3
  formula = Li
  name = G4_Li
  specific = 4
FEATURE [App::DocumentObjectGroupPython] Be_element002  label="Be_element : 002"  # scripted group (container) (typed FeaturePython)
  n = 1
  ref = Be_element
FEATURE [App::DocumentObjectGroupPython] G4_Be  # scripted group (container) (typed FeaturePython)
  Dunit = g/cm3
  Dvalue = 1.848
  Group = -> [Be_element002]
  conduct = 2
  density = 1
  expand = 3
  formula = Be
  name = G4_Be
  specific = 4
FEATURE [App::DocumentObjectGroupPython] B_element007  label="B_element : 007"  # scripted group (container) (typed FeaturePython)
  n = 1
  ref = B_element
FEATURE [App::DocumentObjectGroupPython] G4_B  # scripted group (container) (typed FeaturePython)
  Dunit = g/cm3
  Dvalue = 2.37
  Group = -> [B_element007]
  conduct = 2
  density = 1
  expand = 3
  formula = B
  name = G4_B
  specific = 4
FEATURE [App::DocumentObjectGroupPython] C_element124  label="C_element : 070"  # scripted group (container) (typed FeaturePython)
  n = 1
  ref = C_element
FEATURE [App::DocumentObjectGroupPython] G4_C  # scripted group (container) (typed FeaturePython)
  Dunit = g/cm3
  Dvalue = 2
  Group = -> [C_element124]
  conduct = 2
  density = 1
  expand = 3
  formula = C
  name = G4_C
  specific = 4
FEATURE [App::DocumentObjectGroupPython] N_element048  label="N_element : 021"  # scripted group (container) (typed FeaturePython)
  n = 1
  ref = N_element
FEATURE [App::DocumentObjectGroupPython] G4_N  # scripted group (container) (typed FeaturePython)
  Dunit = g/cm3
  Dvalue = 0.0011652
  Group = -> [N_element048]
  conduct = 2
  density = 1
  expand = 3
  formula = N
  name = G4_N
  specific = 4
FEATURE [App::DocumentObjectGroupPython] O_element105  label="O_element : 059"  # scripted group (container) (typed FeaturePython)
  n = 1
  ref = O_element
FEATURE [App::DocumentObjectGroupPython] G4_O  # scripted group (container) (typed FeaturePython)
  Dunit = g/cm3
  Dvalue = 0.00133151
  Group = -> [O_element105]
  conduct = 2
  density = 1
  expand = 3
  formula = O
  name = G4_O
  specific = 4
FEATURE [App::DocumentObjectGroupPython] F_element019  label="F_element : 008"  # scripted group (container) (typed FeaturePython)
  n = 1
  ref = F_element
FEATURE [App::DocumentObjectGroupPython] G4_F  # scripted group (container) (typed FeaturePython)
  Dunit = g/cm3
  Dvalue = 0.00158029
  Group = -> [F_element019]
  conduct = 2
  density = 1
  expand = 3
  formula = F
  name = G4_F
  specific = 4
FEATURE [App::DocumentObjectGroupPython] Ne_element001  label="Ne_element : 1"  # scripted group (container) (typed FeaturePython)
  n = 1
  ref = Ne_element
FEATURE [App::DocumentObjectGroupPython] G4_Ne  # scripted group (container) (typed FeaturePython)
  Dunit = g/cm3
  Dvalue = 0.000838505
  Group = -> [Ne_element001]
  conduct = 2
  density = 1
  expand = 3
  formula = Ne
  name = G4_Ne
  specific = 4
FEATURE [App::DocumentObjectGroupPython] Na_element020  label="Na_element : 005"  # scripted group (container) (typed FeaturePython)
  n = 1
  ref = Na_element
FEATURE [App::DocumentObjectGroupPython] G4_Na  # scripted group (container) (typed FeaturePython)
  Dunit = g/cm3
  Dvalue = 0.971
  Group = -> [Na_element020]
  conduct = 2
  density = 1
  expand = 3
  formula = Na
  name = G4_Na
  specific = 4
FEATURE [App::DocumentObjectGroupPython] Mg_element011  label="Mg_element : 005"  # scripted group (container) (typed FeaturePython)
  n = 1
  ref = Mg_element
FEATURE [App::DocumentObjectGroupPython] G4_Mg  # scripted group (container) (typed FeaturePython)
  Dunit = g/cm3
  Dvalue = 1.74
  Group = -> [Mg_element011]
  conduct = 2
  density = 1
  expand = 3
  formula = Mg
  name = G4_Mg
  specific = 4
FEATURE [App::DocumentObjectGroupPython] Al_element004  label="Al_element : 1"  # scripted group (container) (typed FeaturePython)
  n = 1
  ref = Al_element
FEATURE [App::DocumentObjectGroupPython] G4_Al  # scripted group (container) (typed FeaturePython)
  Dunit = g/cm3
  Dvalue = 2.699
  Group = -> [Al_element004]
  conduct = 2
  density = 1
  expand = 3
  formula = Al
  name = G4_Al
  specific = 4
FEATURE [App::DocumentObjectGroupPython] Si_element007  label="Si_element : 002"  # scripted group (container) (typed FeaturePython)
  n = 1
  ref = Si_element
FEATURE [App::DocumentObjectGroupPython] G4_Si  # scripted group (container) (typed FeaturePython)
  Dunit = g/cm3
  Dvalue = 2.33
  Group = -> [Si_element007]
  conduct = 2
  density = 1
  expand = 3
  formula = Si
  name = G4_Si
  specific = 4
FEATURE [App::DocumentObjectGroupPython] P_element013  label="P_element : 002"  # scripted group (container) (typed FeaturePython)
  n = 1
  ref = P_element
FEATURE [App::DocumentObjectGroupPython] G4_P  # scripted group (container) (typed FeaturePython)
  Dunit = g/cm3
  Dvalue = 2.2
  Group = -> [P_element013]
  conduct = 2
  density = 1
  expand = 3
  formula = P
  name = G4_P
  specific = 4
FEATURE [App::DocumentObjectGroupPython] S_element023  label="S_element : 007"  # scripted group (container) (typed FeaturePython)
  n = 1
  ref = S_element
FEATURE [App::DocumentObjectGroupPython] G4_S  # scripted group (container) (typed FeaturePython)
  Dunit = g/cm3
  Dvalue = 2
  Group = -> [S_element023]
  conduct = 2
  density = 1
  expand = 3
  formula = S
  name = G4_S
  specific = 4
FEATURE [App::DocumentObjectGroupPython] Cl_element029  label="Cl_element : 015"  # scripted group (container) (typed FeaturePython)
  n = 1
  ref = Cl_element
FEATURE [App::DocumentObjectGroupPython] G4_Cl  # scripted group (container) (typed FeaturePython)
  Dunit = g/cm3
  Dvalue = 0.00299473
  Group = -> [Cl_element029]
  conduct = 2
  density = 1
  expand = 3
  formula = Cl
  name = G4_Cl
  specific = 4
FEATURE [App::DocumentObjectGroupPython] Ar_element002  label="Ar_element : 1"  # scripted group (container) (typed FeaturePython)
  n = 1
  ref = Ar_element
FEATURE [App::DocumentObjectGroupPython] G4_Ar  # scripted group (container) (typed FeaturePython)
  Dunit = g/cm3
  Dvalue = 0.00166201
  Group = -> [Ar_element002]
  conduct = 2
  density = 1
  expand = 3
  formula = Ar
  name = G4_Ar
  specific = 4
FEATURE [App::DocumentObjectGroupPython] K_element013  label="K_element : 003"  # scripted group (container) (typed FeaturePython)
  n = 1
  ref = K_element
FEATURE [App::DocumentObjectGroupPython] G4_K  # scripted group (container) (typed FeaturePython)
  Dunit = g/cm3
  Dvalue = 0.862
  Group = -> [K_element013]
  conduct = 2
  density = 1
  expand = 3
  formula = K
  name = G4_K
  specific = 4
FEATURE [App::DocumentObjectGroupPython] Ca_element014  label="Ca_element : 007"  # scripted group (container) (typed FeaturePython)
  n = 1
  ref = Ca_element
FEATURE [App::DocumentObjectGroupPython] G4_Ca  # scripted group (container) (typed FeaturePython)
  Dunit = g/cm3
  Dvalue = 1.55
  Group = -> [Ca_element014]
  conduct = 2
  density = 1
  expand = 3
  formula = Ca
  name = G4_Ca
  specific = 4
FEATURE [App::DocumentObjectGroupPython] Sc_element001  label="Sc_element : 1"  # scripted group (container) (typed FeaturePython)
  n = 1
  ref = Sc_element
FEATURE [App::DocumentObjectGroupPython] G4_Sc  # scripted group (container) (typed FeaturePython)
  Dunit = g/cm3
  Dvalue = 2.989
  Group = -> [Sc_element001]
  conduct = 2
  density = 1
  expand = 3
  formula = Sc
  name = G4_Sc
  specific = 4
FEATURE [App::DocumentObjectGroupPython] Ti_element004  label="Ti_element : 002"  # scripted group (container) (typed FeaturePython)
  n = 1
  ref = Ti_element
FEATURE [App::DocumentObjectGroupPython] G4_Ti  # scripted group (container) (typed FeaturePython)
  Dunit = g/cm3
  Dvalue = 4.54
  Group = -> [Ti_element004]
  conduct = 2
  density = 1
  expand = 3
  formula = Ti
  name = G4_Ti
  specific = 4
FEATURE [App::DocumentObjectGroupPython] V_element001  label="V_element : 1"  # scripted group (container) (typed FeaturePython)
  n = 1
  ref = V_element
FEATURE [App::DocumentObjectGroupPython] G4_V  # scripted group (container) (typed FeaturePython)
  Dunit = g/cm3
  Dvalue = 6.11
  Group = -> [V_element001]
  conduct = 2
  density = 1
  expand = 3
  formula = V
  name = G4_V
  specific = 4
FEATURE [App::DocumentObjectGroupPython] Cr_element001  label="Cr_element : 1"  # scripted group (container) (typed FeaturePython)
  n = 1
  ref = Cr_element
FEATURE [App::DocumentObjectGroupPython] G4_Cr  # scripted group (container) (typed FeaturePython)
  Dunit = g/cm3
  Dvalue = 7.18
  Group = -> [Cr_element001]
  conduct = 2
  density = 1
  expand = 3
  formula = Cr
  name = G4_Cr
  specific = 4
FEATURE [App::DocumentObjectGroupPython] Mn_element001  label="Mn_element : 1"  # scripted group (container) (typed FeaturePython)
  n = 1
  ref = Mn_element
FEATURE [App::DocumentObjectGroupPython] G4_Mn  # scripted group (container) (typed FeaturePython)
  Dunit = g/cm3
  Dvalue = 7.44
  Group = -> [Mn_element001]
  conduct = 2
  density = 1
  expand = 3
  formula = Mn
  name = G4_Mn
  specific = 4
FEATURE [App::DocumentObjectGroupPython] Fe_element007  label="Fe_element : 004"  # scripted group (container) (typed FeaturePython)
  n = 1
  ref = Fe_element
FEATURE [App::DocumentObjectGroupPython] G4_Fe  # scripted group (container) (typed FeaturePython)
  Dunit = g/cm3
  Dvalue = 7.874
  Group = -> [Fe_element007]
  conduct = 2
  density = 1
  expand = 3
  formula = Fe
  name = G4_Fe
  specific = 4
FEATURE [App::DocumentObjectGroupPython] Co_element001  label="Co_element : 1"  # scripted group (container) (typed FeaturePython)
  n = 1
  ref = Co_element
FEATURE [App::DocumentObjectGroupPython] G4_Co  # scripted group (container) (typed FeaturePython)
  Dunit = g/cm3
  Dvalue = 8.9
  Group = -> [Co_element001]
  conduct = 2
  density = 1
  expand = 3
  formula = Co
  name = G4_Co
  specific = 4
FEATURE [App::DocumentObjectGroupPython] Ni_element001  label="Ni_element : 1"  # scripted group (container) (typed FeaturePython)
  n = 1
  ref = Ni_element
FEATURE [App::DocumentObjectGroupPython] G4_Ni  # scripted group (container) (typed FeaturePython)
  Dunit = g/cm3
  Dvalue = 8.902
  Group = -> [Ni_element001]
  conduct = 2
  density = 1
  expand = 3
  formula = Ni
  name = G4_Ni
  specific = 4
FEATURE [App::DocumentObjectGroupPython] Cu_element001  label="Cu_element : 1"  # scripted group (container) (typed FeaturePython)
  n = 1
  ref = Cu_element
FEATURE [App::DocumentObjectGroupPython] G4_Cu  # scripted group (container) (typed FeaturePython)
  Dunit = g/cm3
  Dvalue = 8.96
  Group = -> [Cu_element001]
  conduct = 2
  density = 1
  expand = 3
  formula = Cu
  name = G4_Cu
  specific = 4
FEATURE [App::DocumentObjectGroupPython] Zn_element001  label="Zn_element : 1"  # scripted group (container) (typed FeaturePython)
  n = 1
  ref = Zn_element
FEATURE [App::DocumentObjectGroupPython] G4_Zn  # scripted group (container) (typed FeaturePython)
  Dunit = g/cm3
  Dvalue = 7.133
  Group = -> [Zn_element001]
  conduct = 2
  density = 1
  expand = 3
  formula = Zn
  name = G4_Zn
  specific = 4
FEATURE [App::DocumentObjectGroupPython] Ga_element002  label="Ga_element : 002"  # scripted group (container) (typed FeaturePython)
  n = 1
  ref = Ga_element
FEATURE [App::DocumentObjectGroupPython] G4_Ga  # scripted group (container) (typed FeaturePython)
  Dunit = g/cm3
  Dvalue = 5.904
  Group = -> [Ga_element002]
  conduct = 2
  density = 1
  expand = 3
  formula = Ga
  name = G4_Ga
  specific = 4
FEATURE [App::DocumentObjectGroupPython] Ge_element002  label="Ge_element : 1"  # scripted group (container) (typed FeaturePython)
  n = 1
  ref = Ge_element
FEATURE [App::DocumentObjectGroupPython] G4_Ge  # scripted group (container) (typed FeaturePython)
  Dunit = g/cm3
  Dvalue = 5.323
  Group = -> [Ge_element002]
  conduct = 2
  density = 1
  expand = 3
  formula = Ge
  name = G4_Ge
  specific = 4
FEATURE [App::DocumentObjectGroupPython] As_element003  label="As_element : 002"  # scripted group (container) (typed FeaturePython)
  n = 1
  ref = As_element
FEATURE [App::DocumentObjectGroupPython] G4_As  # scripted group (container) (typed FeaturePython)
  Dunit = g/cm3
  Dvalue = 5.73
  Group = -> [As_element003]
  conduct = 2
  density = 1
  expand = 3
  formula = As
  name = G4_As
  specific = 4
FEATURE [App::DocumentObjectGroupPython] Se_element001  label="Se_element : 1"  # scripted group (container) (typed FeaturePython)
  n = 1
  ref = Se_element
FEATURE [App::DocumentObjectGroupPython] G4_Se  # scripted group (container) (typed FeaturePython)
  Dunit = g/cm3
  Dvalue = 4.5
  Group = -> [Se_element001]
  conduct = 2
  density = 1
  expand = 3
  formula = Se
  name = G4_Se
  specific = 4
FEATURE [App::DocumentObjectGroupPython] Br_element007  label="Br_element : 004"  # scripted group (container) (typed FeaturePython)
  n = 1
  ref = Br_element
FEATURE [App::DocumentObjectGroupPython] G4_Br  # scripted group (container) (typed FeaturePython)
  Dunit = g/cm3
  Dvalue = 0.0070721
  Group = -> [Br_element007]
  conduct = 2
  density = 1
  expand = 3
  formula = Br
  name = G4_Br
  specific = 4
FEATURE [App::DocumentObjectGroupPython] Kr_element001  label="Kr_element : 1"  # scripted group (container) (typed FeaturePython)
  n = 1
  ref = Kr_element
FEATURE [App::DocumentObjectGroupPython] G4_Kr  # scripted group (container) (typed FeaturePython)
  Dunit = g/cm3
  Dvalue = 0.00347832
  Group = -> [Kr_element001]
  conduct = 2
  density = 1
  expand = 3
  formula = Kr
  name = G4_Kr
  specific = 4
FEATURE [App::DocumentObjectGroupPython] Rb_element001  label="Rb_element : 1"  # scripted group (container) (typed FeaturePython)
  n = 1
  ref = Rb_element
FEATURE [App::DocumentObjectGroupPython] G4_Rb  # scripted group (container) (typed FeaturePython)
  Dunit = g/cm3
  Dvalue = 1.532
  Group = -> [Rb_element001]
  conduct = 2
  density = 1
  expand = 3
  formula = Rb
  name = G4_Rb
  specific = 4
FEATURE [App::DocumentObjectGroupPython] Sr_element001  label="Sr_element : 1"  # scripted group (container) (typed FeaturePython)
  n = 1
  ref = Sr_element
FEATURE [App::DocumentObjectGroupPython] G4_Sr  # scripted group (container) (typed FeaturePython)
  Dunit = g/cm3
  Dvalue = 2.54
  Group = -> [Sr_element001]
  conduct = 2
  density = 1
  expand = 3
  formula = Sr
  name = G4_Sr
  specific = 4
FEATURE [App::DocumentObjectGroupPython] Y_element001  label="Y_element : 1"  # scripted group (container) (typed FeaturePython)
  n = 1
  ref = Y_element
FEATURE [App::DocumentObjectGroupPython] G4_Y  # scripted group (container) (typed FeaturePython)
  Dunit = g/cm3
  Dvalue = 4.469
  Group = -> [Y_element001]
  conduct = 2
  density = 1
  expand = 3
  formula = Y
  name = G4_Y
  specific = 4
FEATURE [App::DocumentObjectGroupPython] Zr_element001  label="Zr_element : 1"  # scripted group (container) (typed FeaturePython)
  n = 1
  ref = Zr_element
FEATURE [App::DocumentObjectGroupPython] G4_Zr  # scripted group (container) (typed FeaturePython)
  Dunit = g/cm3
  Dvalue = 6.506
  Group = -> [Zr_element001]
  conduct = 2
  density = 1
  expand = 3
  formula = Zr
  name = G4_Zr
  specific = 4
FEATURE [App::DocumentObjectGroupPython] Nb_element001  label="Nb_element : 1"  # scripted group (container) (typed FeaturePython)
  n = 1
  ref = Nb_element
FEATURE [App::DocumentObjectGroupPython] G4_Nb  # scripted group (container) (typed FeaturePython)
  Dunit = g/cm3
  Dvalue = 8.57
  Group = -> [Nb_element001]
  conduct = 2
  density = 1
  expand = 3
  formula = Nb
  name = G4_Nb
  specific = 4
FEATURE [App::DocumentObjectGroupPython] Mo_element001  label="Mo_element : 1"  # scripted group (container) (typed FeaturePython)
  n = 1
  ref = Mo_element
FEATURE [App::DocumentObjectGroupPython] G4_Mo  # scripted group (container) (typed FeaturePython)
  Dunit = g/cm3
  Dvalue = 10.22
  Group = -> [Mo_element001]
  conduct = 2
  density = 1
  expand = 3
  formula = Mo
  name = G4_Mo
  specific = 4
FEATURE [App::DocumentObjectGroupPython] Tc_element001  label="Tc_element : 1"  # scripted group (container) (typed FeaturePython)
  n = 1
  ref = Tc_element
FEATURE [App::DocumentObjectGroupPython] G4_Tc  # scripted group (container) (typed FeaturePython)
  Dunit = g/cm3
  Dvalue = 11.5
  Group = -> [Tc_element001]
  conduct = 2
  density = 1
  expand = 3
  formula = Tc
  name = G4_Tc
  specific = 4
FEATURE [App::DocumentObjectGroupPython] Ru_element001  label="Ru_element : 1"  # scripted group (container) (typed FeaturePython)
  n = 1
  ref = Ru_element
FEATURE [App::DocumentObjectGroupPython] G4_Ru  # scripted group (container) (typed FeaturePython)
  Dunit = g/cm3
  Dvalue = 12.41
  Group = -> [Ru_element001]
  conduct = 2
  density = 1
  expand = 3
  formula = Ru
  name = G4_Ru
  specific = 4
FEATURE [App::DocumentObjectGroupPython] Rh_element001  label="Rh_element : 1"  # scripted group (container) (typed FeaturePython)
  n = 1
  ref = Rh_element
FEATURE [App::DocumentObjectGroupPython] G4_Rh  # scripted group (container) (typed FeaturePython)
  Dunit = g/cm3
  Dvalue = 12.41
  Group = -> [Rh_element001]
  conduct = 2
  density = 1
  expand = 3
  formula = Rh
  name = G4_Rh
  specific = 4
FEATURE [App::DocumentObjectGroupPython] Pd_element001  label="Pd_element : 1"  # scripted group (container) (typed FeaturePython)
  n = 1
  ref = Pd_element
FEATURE [App::DocumentObjectGroupPython] G4_Pd  # scripted group (container) (typed FeaturePython)
  Dunit = g/cm3
  Dvalue = 12.02
  Group = -> [Pd_element001]
  conduct = 2
  density = 1
  expand = 3
  formula = Pd
  name = G4_Pd
  specific = 4
FEATURE [App::DocumentObjectGroupPython] Ag_element006  label="Ag_element : 004"  # scripted group (container) (typed FeaturePython)
  n = 1
  ref = Ag_element
FEATURE [App::DocumentObjectGroupPython] G4_Ag  # scripted group (container) (typed FeaturePython)
  Dunit = g/cm3
  Dvalue = 10.5
  Group = -> [Ag_element006]
  conduct = 2
  density = 1
  expand = 3
  formula = Ag
  name = G4_Ag
  specific = 4
FEATURE [App::DocumentObjectGroupPython] Cd_element003  label="Cd_element : 003"  # scripted group (container) (typed FeaturePython)
  n = 1
  ref = Cd_element
FEATURE [App::DocumentObjectGroupPython] G4_Cd  # scripted group (container) (typed FeaturePython)
  Dunit = g/cm3
  Dvalue = 8.65
  Group = -> [Cd_element003]
  conduct = 2
  density = 1
  expand = 3
  formula = Cd
  name = G4_Cd
  specific = 4
FEATURE [App::DocumentObjectGroupPython] In_element001  label="In_element : 1"  # scripted group (container) (typed FeaturePython)
  n = 1
  ref = In_element
FEATURE [App::DocumentObjectGroupPython] G4_In  # scripted group (container) (typed FeaturePython)
  Dunit = g/cm3
  Dvalue = 7.31
  Group = -> [In_element001]
  conduct = 2
  density = 1
  expand = 3
  formula = In
  name = G4_In
  specific = 4
FEATURE [App::DocumentObjectGroupPython] Sn_element001  label="Sn_element : 1"  # scripted group (container) (typed FeaturePython)
  n = 1
  ref = Sn_element
FEATURE [App::DocumentObjectGroupPython] G4_Sn  # scripted group (container) (typed FeaturePython)
  Dunit = g/cm3
  Dvalue = 7.31
  Group = -> [Sn_element001]
  conduct = 2
  density = 1
  expand = 3
  formula = Sn
  name = G4_Sn
  specific = 4
FEATURE [App::DocumentObjectGroupPython] Sb_element001  label="Sb_element : 1"  # scripted group (container) (typed FeaturePython)
  n = 1
  ref = Sb_element
FEATURE [App::DocumentObjectGroupPython] G4_Sb  # scripted group (container) (typed FeaturePython)
  Dunit = g/cm3
  Dvalue = 6.691
  Group = -> [Sb_element001]
  conduct = 2
  density = 1
  expand = 3
  formula = Sb
  name = G4_Sb
  specific = 4
FEATURE [App::DocumentObjectGroupPython] Te_element002  label="Te_element : 002"  # scripted group (container) (typed FeaturePython)
  n = 1
  ref = Te_element
FEATURE [App::DocumentObjectGroupPython] G4_Te  # scripted group (container) (typed FeaturePython)
  Dunit = g/cm3
  Dvalue = 6.24
  Group = -> [Te_element002]
  conduct = 2
  density = 1
  expand = 3
  formula = Te
  name = G4_Te
  specific = 4
FEATURE [App::DocumentObjectGroupPython] I_element010  label="I_element : 006"  # scripted group (container) (typed FeaturePython)
  n = 1
  ref = I_element
FEATURE [App::DocumentObjectGroupPython] G4_I  # scripted group (container) (typed FeaturePython)
  Dunit = g/cm3
  Dvalue = 4.93
  Group = -> [I_element010]
  conduct = 2
  density = 1
  expand = 3
  formula = I
  name = G4_I
  specific = 4
FEATURE [App::DocumentObjectGroupPython] Xe_element001  label="Xe_element : 1"  # scripted group (container) (typed FeaturePython)
  n = 1
  ref = Xe_element
FEATURE [App::DocumentObjectGroupPython] G4_Xe  # scripted group (container) (typed FeaturePython)
  Dunit = g/cm3
  Dvalue = 0.00548536
  Group = -> [Xe_element001]
  conduct = 2
  density = 1
  expand = 3
  formula = Xe
  name = G4_Xe
  specific = 4
FEATURE [App::DocumentObjectGroupPython] Cs_element003  label="Cs_element : 003"  # scripted group (container) (typed FeaturePython)
  n = 1
  ref = Cs_element
FEATURE [App::DocumentObjectGroupPython] G4_Cs  # scripted group (container) (typed FeaturePython)
  Dunit = g/cm3
  Dvalue = 1.873
  Group = -> [Cs_element003]
  conduct = 2
  density = 1
  expand = 3
  formula = Cs
  name = G4_Cs
  specific = 4
FEATURE [App::DocumentObjectGroupPython] Ba_element003  label="Ba_element : 003"  # scripted group (container) (typed FeaturePython)
  n = 1
  ref = Ba_element
FEATURE [App::DocumentObjectGroupPython] G4_Ba  # scripted group (container) (typed FeaturePython)
  Dunit = g/cm3
  Dvalue = 3.5
  Group = -> [Ba_element003]
  conduct = 2
  density = 1
  expand = 3
  formula = Ba
  name = G4_Ba
  specific = 4
FEATURE [App::DocumentObjectGroupPython] La_element003  label="La_element : 003"  # scripted group (container) (typed FeaturePython)
  n = 1
  ref = La_element
FEATURE [App::DocumentObjectGroupPython] G4_La  # scripted group (container) (typed FeaturePython)
  Dunit = g/cm3
  Dvalue = 6.154
  Group = -> [La_element003]
  conduct = 2
  density = 1
  expand = 3
  formula = La
  name = G4_La
  specific = 4
FEATURE [App::DocumentObjectGroupPython] Ce_element002  label="Ce_element : 1"  # scripted group (container) (typed FeaturePython)
  n = 1
  ref = Ce_element
FEATURE [App::DocumentObjectGroupPython] G4_Ce  # scripted group (container) (typed FeaturePython)
  Dunit = g/cm3
  Dvalue = 6.657
  Group = -> [Ce_element002]
  conduct = 2
  density = 1
  expand = 3
  formula = Ce
  name = G4_Ce
  specific = 4
FEATURE [App::DocumentObjectGroupPython] Pr_element001  label="Pr_element : 1"  # scripted group (container) (typed FeaturePython)
  n = 1
  ref = Pr_element
FEATURE [App::DocumentObjectGroupPython] G4_Pr  # scripted group (container) (typed FeaturePython)
  Dunit = g/cm3
  Dvalue = 6.71
  Group = -> [Pr_element001]
  conduct = 2
  density = 1
  expand = 3
  formula = Pr
  name = G4_Pr
  specific = 4
FEATURE [App::DocumentObjectGroupPython] Nd_element001  label="Nd_element : 1"  # scripted group (container) (typed FeaturePython)
  n = 1
  ref = Nd_element
FEATURE [App::DocumentObjectGroupPython] G4_Nd  # scripted group (container) (typed FeaturePython)
  Dunit = g/cm3
  Dvalue = 6.9
  Group = -> [Nd_element001]
  conduct = 2
  density = 1
  expand = 3
  formula = Nd
  name = G4_Nd
  specific = 4
FEATURE [App::DocumentObjectGroupPython] Pm_element001  label="Pm_element : 1"  # scripted group (container) (typed FeaturePython)
  n = 1
  ref = Pm_element
FEATURE [App::DocumentObjectGroupPython] G4_Pm  # scripted group (container) (typed FeaturePython)
  Dunit = g/cm3
  Dvalue = 7.22
  Group = -> [Pm_element001]
  conduct = 2
  density = 1
  expand = 3
  formula = Pm
  name = G4_Pm
  specific = 4
FEATURE [App::DocumentObjectGroupPython] Sm_element001  label="Sm_element : 1"  # scripted group (container) (typed FeaturePython)
  n = 1
  ref = Sm_element
FEATURE [App::DocumentObjectGroupPython] G4_Sm  # scripted group (container) (typed FeaturePython)
  Dunit = g/cm3
  Dvalue = 7.46
  Group = -> [Sm_element001]
  conduct = 2
  density = 1
  expand = 3
  formula = Sm
  name = G4_Sm
  specific = 4
FEATURE [App::DocumentObjectGroupPython] Eu_element001  label="Eu_element : 1"  # scripted group (container) (typed FeaturePython)
  n = 1
  ref = Eu_element
FEATURE [App::DocumentObjectGroupPython] G4_Eu  # scripted group (container) (typed FeaturePython)
  Dunit = g/cm3
  Dvalue = 5.243
  Group = -> [Eu_element001]
  conduct = 2
  density = 1
  expand = 3
  formula = Eu
  name = G4_Eu
  specific = 4
FEATURE [App::DocumentObjectGroupPython] Gd_element002  label="Gd_element : 1"  # scripted group (container) (typed FeaturePython)
  n = 1
  ref = Gd_element
FEATURE [App::DocumentObjectGroupPython] G4_Gd  # scripted group (container) (typed FeaturePython)
  Dunit = g/cm3
  Dvalue = 7.9004
  Group = -> [Gd_element002]
  conduct = 2
  density = 1
  expand = 3
  formula = Gd
  name = G4_Gd
  specific = 4
FEATURE [App::DocumentObjectGroupPython] Tb_element001  label="Tb_element : 1"  # scripted group (container) (typed FeaturePython)
  n = 1
  ref = Tb_element
FEATURE [App::DocumentObjectGroupPython] G4_Tb  # scripted group (container) (typed FeaturePython)
  Dunit = g/cm3
  Dvalue = 8.229
  Group = -> [Tb_element001]
  conduct = 2
  density = 1
  expand = 3
  formula = Tb
  name = G4_Tb
  specific = 4
FEATURE [App::DocumentObjectGroupPython] Dy_element001  label="Dy_element : 1"  # scripted group (container) (typed FeaturePython)
  n = 1
  ref = Dy_element
FEATURE [App::DocumentObjectGroupPython] G4_Dy  # scripted group (container) (typed FeaturePython)
  Dunit = g/cm3
  Dvalue = 8.55
  Group = -> [Dy_element001]
  conduct = 2
  density = 1
  expand = 3
  formula = Dy
  name = G4_Dy
  specific = 4
FEATURE [App::DocumentObjectGroupPython] Ho_element001  label="Ho_element : 1"  # scripted group (container) (typed FeaturePython)
  n = 1
  ref = Ho_element
FEATURE [App::DocumentObjectGroupPython] G4_Ho  # scripted group (container) (typed FeaturePython)
  Dunit = g/cm3
  Dvalue = 8.795
  Group = -> [Ho_element001]
  conduct = 2
  density = 1
  expand = 3
  formula = Ho
  name = G4_Ho
  specific = 4
FEATURE [App::DocumentObjectGroupPython] Er_element001  label="Er_element : 1"  # scripted group (container) (typed FeaturePython)
  n = 1
  ref = Er_element
FEATURE [App::DocumentObjectGroupPython] G4_Er  # scripted group (container) (typed FeaturePython)
  Dunit = g/cm3
  Dvalue = 9.066
  Group = -> [Er_element001]
  conduct = 2
  density = 1
  expand = 3
  formula = Er
  name = G4_Er
  specific = 4
FEATURE [App::DocumentObjectGroupPython] Tm_element001  label="Tm_element : 1"  # scripted group (container) (typed FeaturePython)
  n = 1
  ref = Tm_element
FEATURE [App::DocumentObjectGroupPython] G4_Tm  # scripted group (container) (typed FeaturePython)
  Dunit = g/cm3
  Dvalue = 9.321
  Group = -> [Tm_element001]
  conduct = 2
  density = 1
  expand = 3
  formula = Tm
  name = G4_Tm
  specific = 4
FEATURE [App::DocumentObjectGroupPython] Yb_element001  label="Yb_element : 1"  # scripted group (container) (typed FeaturePython)
  n = 1
  ref = Yb_element
FEATURE [App::DocumentObjectGroupPython] G4_Yb  # scripted group (container) (typed FeaturePython)
  Dunit = g/cm3
  Dvalue = 6.73
  Group = -> [Yb_element001]
  conduct = 2
  density = 1
  expand = 3
  formula = Yb
  name = G4_Yb
  specific = 4
FEATURE [App::DocumentObjectGroupPython] Lu_element001  label="Lu_element : 1"  # scripted group (container) (typed FeaturePython)
  n = 1
  ref = Lu_element
FEATURE [App::DocumentObjectGroupPython] G4_Lu  # scripted group (container) (typed FeaturePython)
  Dunit = g/cm3
  Dvalue = 9.84
  Group = -> [Lu_element001]
  conduct = 2
  density = 1
  expand = 3
  formula = Lu
  name = G4_Lu
  specific = 4
FEATURE [App::DocumentObjectGroupPython] Hf_element001  label="Hf_element : 1"  # scripted group (container) (typed FeaturePython)
  n = 1
  ref = Hf_element
FEATURE [App::DocumentObjectGroupPython] G4_Hf  # scripted group (container) (typed FeaturePython)
  Dunit = g/cm3
  Dvalue = 13.31
  Group = -> [Hf_element001]
  conduct = 2
  density = 1
  expand = 3
  formula = Hf
  name = G4_Hf
  specific = 4
FEATURE [App::DocumentObjectGroupPython] Ta_element001  label="Ta_element : 1"  # scripted group (container) (typed FeaturePython)
  n = 1
  ref = Ta_element
FEATURE [App::DocumentObjectGroupPython] G4_Ta  # scripted group (container) (typed FeaturePython)
  Dunit = g/cm3
  Dvalue = 16.654
  Group = -> [Ta_element001]
  conduct = 2
  density = 1
  expand = 3
  formula = Ta
  name = G4_Ta
  specific = 4
FEATURE [App::DocumentObjectGroupPython] W_element004  label="W_element : 004"  # scripted group (container) (typed FeaturePython)
  n = 1
  ref = W_element
FEATURE [App::DocumentObjectGroupPython] G4_W  # scripted group (container) (typed FeaturePython)
  Dunit = g/cm3
  Dvalue = 19.3
  Group = -> [W_element004]
  conduct = 2
  density = 1
  expand = 3
  formula = W
  name = G4_W
  specific = 4
FEATURE [App::DocumentObjectGroupPython] Re_element001  label="Re_element : 1"  # scripted group (container) (typed FeaturePython)
  n = 1
  ref = Re_element
FEATURE [App::DocumentObjectGroupPython] G4_Re  # scripted group (container) (typed FeaturePython)
  Dunit = g/cm3
  Dvalue = 21.02
  Group = -> [Re_element001]
  conduct = 2
  density = 1
  expand = 3
  formula = Re
  name = G4_Re
  specific = 4
FEATURE [App::DocumentObjectGroupPython] Os_element001  label="Os_element : 1"  # scripted group (container) (typed FeaturePython)
  n = 1
  ref = Os_element
FEATURE [App::DocumentObjectGroupPython] G4_Os  # scripted group (container) (typed FeaturePython)
  Dunit = g/cm3
  Dvalue = 22.57
  Group = -> [Os_element001]
  conduct = 2
  density = 1
  expand = 3
  formula = Os
  name = G4_Os
  specific = 4
FEATURE [App::DocumentObjectGroupPython] Ir_element001  label="Ir_element : 1"  # scripted group (container) (typed FeaturePython)
  n = 1
  ref = Ir_element
FEATURE [App::DocumentObjectGroupPython] G4_Ir  # scripted group (container) (typed FeaturePython)
  Dunit = g/cm3
  Dvalue = 22.42
  Group = -> [Ir_element001]
  conduct = 2
  density = 1
  expand = 3
  formula = Ir
  name = G4_Ir
  specific = 4
FEATURE [App::DocumentObjectGroupPython] Pt_element001  label="Pt_element : 1"  # scripted group (container) (typed FeaturePython)
  n = 1
  ref = Pt_element
FEATURE [App::DocumentObjectGroupPython] G4_Pt  # scripted group (container) (typed FeaturePython)
  Dunit = g/cm3
  Dvalue = 21.45
  Group = -> [Pt_element001]
  conduct = 2
  density = 1
  expand = 3
  formula = Pt
  name = G4_Pt
  specific = 4
FEATURE [App::DocumentObjectGroupPython] Au_element001  label="Au_element : 1"  # scripted group (container) (typed FeaturePython)
  n = 1
  ref = Au_element
FEATURE [App::DocumentObjectGroupPython] G4_Au  # scripted group (container) (typed FeaturePython)
  Dunit = g/cm3
  Dvalue = 19.32
  Group = -> [Au_element001]
  conduct = 2
  density = 1
  expand = 3
  formula = Au
  name = G4_Au
  specific = 4
FEATURE [App::DocumentObjectGroupPython] Hg_element002  label="Hg_element : 002"  # scripted group (container) (typed FeaturePython)
  n = 1
  ref = Hg_element
FEATURE [App::DocumentObjectGroupPython] G4_Hg  # scripted group (container) (typed FeaturePython)
  Dunit = g/cm3
  Dvalue = 13.546
  Group = -> [Hg_element002]
  conduct = 2
  density = 1
  expand = 3
  formula = Hg
  name = G4_Hg
  specific = 4
FEATURE [App::DocumentObjectGroupPython] Tl_element002  label="Tl_element : 002"  # scripted group (container) (typed FeaturePython)
  n = 1
  ref = Tl_element
FEATURE [App::DocumentObjectGroupPython] G4_Tl  # scripted group (container) (typed FeaturePython)
  Dunit = g/cm3
  Dvalue = 11.72
  Group = -> [Tl_element002]
  conduct = 2
  density = 1
  expand = 3
  formula = Tl
  name = G4_Tl
  specific = 4
FEATURE [App::DocumentObjectGroupPython] Pb_element003  label="Pb_element : 1"  # scripted group (container) (typed FeaturePython)
  n = 1
  ref = Pb_element
FEATURE [App::DocumentObjectGroupPython] G4_Pb  # scripted group (container) (typed FeaturePython)
  Dunit = g/cm3
  Dvalue = 11.35
  Group = -> [Pb_element003]
  conduct = 2
  density = 1
  expand = 3
  formula = Pb
  name = G4_Pb
  specific = 4
FEATURE [App::DocumentObjectGroupPython] Bi_element002  label="Bi_element : 1"  # scripted group (container) (typed FeaturePython)
  n = 1
  ref = Bi_element
FEATURE [App::DocumentObjectGroupPython] G4_Bi  # scripted group (container) (typed FeaturePython)
  Dunit = g/cm3
  Dvalue = 9.747
  Group = -> [Bi_element002]
  conduct = 2
  density = 1
  expand = 3
  formula = Bi
  name = G4_Bi
  specific = 4
FEATURE [App::DocumentObjectGroupPython] Po_element001  label="Po_element : 1"  # scripted group (container) (typed FeaturePython)
  n = 1
  ref = Po_element
FEATURE [App::DocumentObjectGroupPython] G4_Po  # scripted group (container) (typed FeaturePython)
  Dunit = g/cm3
  Dvalue = 9.32
  Group = -> [Po_element001]
  conduct = 2
  density = 1
  expand = 3
  formula = Po
  name = G4_Po
  specific = 4
FEATURE [App::DocumentObjectGroupPython] At_element001  label="At_element : 1"  # scripted group (container) (typed FeaturePython)
  n = 1
  ref = At_element
FEATURE [App::DocumentObjectGroupPython] G4_At  # scripted group (container) (typed FeaturePython)
  Dunit = g/cm3
  Dvalue = 9.32
  Group = -> [At_element001]
  conduct = 2
  density = 1
  expand = 3
  formula = At
  name = G4_At
  specific = 4
FEATURE [App::DocumentObjectGroupPython] Rn_element001  label="Rn_element : 1"  # scripted group (container) (typed FeaturePython)
  n = 1
  ref = Rn_element
FEATURE [App::DocumentObjectGroupPython] G4_Rn  # scripted group (container) (typed FeaturePython)
  Dunit = g/cm3
  Dvalue = 0.00900662
  Group = -> [Rn_element001]
  conduct = 2
  density = 1
  expand = 3
  formula = Rn
  name = G4_Rn
  specific = 4
FEATURE [App::DocumentObjectGroupPython] Fr_element001  label="Fr_element : 1"  # scripted group (container) (typed FeaturePython)
  n = 1
  ref = Fr_element
FEATURE [App::DocumentObjectGroupPython] G4_Fr  # scripted group (container) (typed FeaturePython)
  Dunit = g/cm3
  Dvalue = 1
  Group = -> [Fr_element001]
  conduct = 2
  density = 1
  expand = 3
  formula = Fr
  name = G4_Fr
  specific = 4
FEATURE [App::DocumentObjectGroupPython] Ra_element001  label="Ra_element : 1"  # scripted group (container) (typed FeaturePython)
  n = 1
  ref = Ra_element
FEATURE [App::DocumentObjectGroupPython] G4_Ra  # scripted group (container) (typed FeaturePython)
  Dunit = g/cm3
  Dvalue = 5
  Group = -> [Ra_element001]
  conduct = 2
  density = 1
  expand = 3
  formula = Ra
  name = G4_Ra
  specific = 4
FEATURE [App::DocumentObjectGroupPython] Ac_element001  label="Ac_element : 1"  # scripted group (container) (typed FeaturePython)
  n = 1
  ref = Ac_element
FEATURE [App::DocumentObjectGroupPython] G4_Ac  # scripted group (container) (typed FeaturePython)
  Dunit = g/cm3
  Dvalue = 10.07
  Group = -> [Ac_element001]
  conduct = 2
  density = 1
  expand = 3
  formula = Ac
  name = G4_Ac
  specific = 4
FEATURE [App::DocumentObjectGroupPython] Th_element001  label="Th_element : 1"  # scripted group (container) (typed FeaturePython)
  n = 1
  ref = Th_element
FEATURE [App::DocumentObjectGroupPython] G4_Th  # scripted group (container) (typed FeaturePython)
  Dunit = g/cm3
  Dvalue = 11.72
  Group = -> [Th_element001]
  conduct = 2
  density = 1
  expand = 3
  formula = Th
  name = G4_Th
  specific = 4
FEATURE [App::DocumentObjectGroupPython] Pa_element001  label="Pa_element : 1"  # scripted group (container) (typed FeaturePython)
  n = 1
  ref = Pa_element
FEATURE [App::DocumentObjectGroupPython] G4_Pa  # scripted group (container) (typed FeaturePython)
  Dunit = g/cm3
  Dvalue = 15.37
  Group = -> [Pa_element001]
  conduct = 2
  density = 1
  expand = 3
  formula = Pa
  name = G4_Pa
  specific = 4
FEATURE [App::DocumentObjectGroupPython] U_element004  label="U_element : 004"  # scripted group (container) (typed FeaturePython)
  n = 1
  ref = U_element
FEATURE [App::DocumentObjectGroupPython] G4_U  # scripted group (container) (typed FeaturePython)
  Dunit = g/cm3
  Dvalue = 18.95
  Group = -> [U_element004]
  conduct = 2
  density = 1
  expand = 3
  formula = U
  name = G4_U
  specific = 4
FEATURE [App::DocumentObjectGroupPython] Np_element001  label="Np_element : 1"  # scripted group (container) (typed FeaturePython)
  n = 1
  ref = Np_element
FEATURE [App::DocumentObjectGroupPython] G4_Np  # scripted group (container) (typed FeaturePython)
  Dunit = g/cm3
  Dvalue = 20.25
  Group = -> [Np_element001]
  conduct = 2
  density = 1
  expand = 3
  formula = Np
  name = G4_Np
  specific = 4
FEATURE [App::DocumentObjectGroupPython] Pu_element002  label="Pu_element : 002"  # scripted group (container) (typed FeaturePython)
  n = 1
  ref = Pu_element
FEATURE [App::DocumentObjectGroupPython] G4_Pu  # scripted group (container) (typed FeaturePython)
  Dunit = g/cm3
  Dvalue = 19.84
  Group = -> [Pu_element002]
  conduct = 2
  density = 1
  expand = 3
  formula = Pu
  name = G4_Pu
  specific = 4
FEATURE [App::DocumentObjectGroupPython] Am_element001  label="Am_element : 1"  # scripted group (container) (typed FeaturePython)
  n = 1
  ref = Am_element
FEATURE [App::DocumentObjectGroupPython] G4_Am  # scripted group (container) (typed FeaturePython)
  Dunit = g/cm3
  Dvalue = 13.67
  Group = -> [Am_element001]
  conduct = 2
  density = 1
  expand = 3
  formula = Am
  name = G4_Am
  specific = 4
FEATURE [App::DocumentObjectGroupPython] Cm_element001  label="Cm_element : 1"  # scripted group (container) (typed FeaturePython)
  n = 1
  ref = Cm_element
FEATURE [App::DocumentObjectGroupPython] G4_Cm  # scripted group (container) (typed FeaturePython)
  Dunit = g/cm3
  Dvalue = 13.51
  Group = -> [Cm_element001]
  conduct = 2
  density = 1
  expand = 3
  formula = Cm
  name = G4_Cm
  specific = 4
FEATURE [App::DocumentObjectGroupPython] Bk_element001  label="Bk_element : 1"  # scripted group (container) (typed FeaturePython)
  n = 1
  ref = Bk_element
FEATURE [App::DocumentObjectGroupPython] G4_Bk  # scripted group (container) (typed FeaturePython)
  Dunit = g/cm3
  Dvalue = 14
  Group = -> [Bk_element001]
  conduct = 2
  density = 1
  expand = 3
  formula = Bk
  name = G4_Bk
  specific = 4
FEATURE [App::DocumentObjectGroupPython] Cf_element001  label="Cf_element : 1"  # scripted group (container) (typed FeaturePython)
  n = 1
  ref = Cf_element
FEATURE [App::DocumentObjectGroupPython] G4_Cf  # scripted group (container) (typed FeaturePython)
  Dunit = g/cm3
  Dvalue = 10
  Group = -> [Cf_element001]
  conduct = 2
  density = 1
  expand = 3
  formula = Cf
  name = G4_Cf
  specific = 4
FEATURE [App::DocumentObjectGroupPython] Element  # scripted group (container) (typed FeaturePython)
  Group = -> [G4_H,G4_He,G4_Li,G4_Be,G4_B,G4_C,G4_N,G4_O,G4_F,G4_Ne,G4_Na,G4_Mg,G4_Al,G4_Si,G4_P,G4_S,G4_Cl,G4_Ar,G4_K,G4_Ca,G4_Sc,G4_Ti,G4_V,G4_Cr,G4_Mn,G4_Fe,G4_Co,G4_Ni,G4_Cu,G4_Zn,G4_Ga,G4_Ge,G4_As,G4_Se,G4_Br,G4_Kr,G4_Rb,G4_Sr,G4_Y,G4_Zr,G4_Nb,G4_Mo,G4_Tc,G4_Ru,G4_Rh,G4_Pd,G4_Ag,G4_Cd,G4_In,G4_Sn,G4_Sb,G4_Te,G4_I,G4_Xe,G4_Cs,G4_Ba,G4_La,G4_Ce,G4_Pr,G4_Nd,G4_Pm,G4_Sm,G4_Eu,G4_Gd,G4_Tb,G4_Dy,G4_Ho,G4_Er,+30 more]
FEATURE [App::DocumentObjectGroupPython] H_element114  label="H_element : 063"  # scripted group (container) (typed FeaturePython)
  n = 2
  ref = H_element
FEATURE [App::DocumentObjectGroupPython] G4_lH2  # scripted group (container) (typed FeaturePython)
  Dunit = g/cm3
  Dvalue = 0.0708
  Group = -> [H_element114]
  conduct = 2
  density = 1
  expand = 3
  formula = G4_lH2
  name = G4_lH2
  specific = 4
FEATURE [App::DocumentObjectGroupPython] N_element049  label="N_element : 022"  # scripted group (container) (typed FeaturePython)
  n = 2
  ref = N_element
FEATURE [App::DocumentObjectGroupPython] G4_lN2  # scripted group (container) (typed FeaturePython)
  Dunit = g/cm3
  Dvalue = 0.807
  Group = -> [N_element049]
  conduct = 2
  density = 1
  expand = 3
  formula = G4_lN2
  name = G4_lN2
  specific = 4
FEATURE [App::DocumentObjectGroupPython] O_element106  label="O_element : 060"  # scripted group (container) (typed FeaturePython)
  n = 2
  ref = O_element
FEATURE [App::DocumentObjectGroupPython] G4_lO2  # scripted group (container) (typed FeaturePython)
  Dunit = g/cm3
  Dvalue = 1.141
  Group = -> [O_element106]
  conduct = 2
  density = 1
  expand = 3
  formula = G4_lO2
  name = G4_lO2
  specific = 4
FEATURE [App::DocumentObjectGroupPython] Ar  label="Ar : 1"  # scripted group (container) (typed FeaturePython)
  n = 1
  ref = Ar
FEATURE [App::DocumentObjectGroupPython] G4_lAr  # scripted group (container) (typed FeaturePython)
  Dunit = g/cm3
  Dvalue = 1.396
  Group = -> [Ar]
  conduct = 2
  density = 1
  expand = 3
  formula = G4_lAr
  name = G4_lAr
  specific = 4
FEATURE [App::DocumentObjectGroupPython] Br  label="Br : 1"  # scripted group (container) (typed FeaturePython)
  n = 1
  ref = Br
FEATURE [App::DocumentObjectGroupPython] G4_lBr  # scripted group (container) (typed FeaturePython)
  Dunit = g/cm3
  Dvalue = 3.1028
  Group = -> [Br]
  conduct = 2
  density = 1
  expand = 3
  formula = G4_lBr
  name = G4_lBr
  specific = 4
FEATURE [App::DocumentObjectGroupPython] Kr  label="Kr : 1"  # scripted group (container) (typed FeaturePython)
  n = 1
  ref = Kr
FEATURE [App::DocumentObjectGroupPython] G4_lKr  # scripted group (container) (typed FeaturePython)
  Dunit = g/cm3
  Dvalue = 2.418
  Group = -> [Kr]
  conduct = 2
  density = 1
  expand = 3
  formula = G4_lKr
  name = G4_lKr
  specific = 4
FEATURE [App::DocumentObjectGroupPython] Xe  label="Xe : 1"  # scripted group (container) (typed FeaturePython)
  n = 1
  ref = Xe
FEATURE [App::DocumentObjectGroupPython] G4_lXe  # scripted group (container) (typed FeaturePython)
  Dunit = g/cm3
  Dvalue = 2.953
  Group = -> [Xe]
  conduct = 2
  density = 1
  expand = 3
  formula = G4_lXe
  name = G4_lXe
  specific = 4
FEATURE [App::DocumentObjectGroupPython] O_element107  label="O_element : 061"  # scripted group (container) (typed FeaturePython)
  n = 4
  ref = O_element
FEATURE [App::DocumentObjectGroupPython] Pb_element004  label="Pb_element : 002"  # scripted group (container) (typed FeaturePython)
  n = 1
  ref = Pb_element
FEATURE [App::DocumentObjectGroupPython] W_element005  label="W_element : 005"  # scripted group (container) (typed FeaturePython)
  n = 1
  ref = W_element
FEATURE [App::DocumentObjectGroupPython] G4_PbWO4  # scripted group (container) (typed FeaturePython)
  Dunit = g/cm3
  Dvalue = 8.28
  Group = -> [O_element107,Pb_element004,W_element005]
  conduct = 2
  density = 1
  expand = 3
  formula = G4_PbWO4
  name = G4_PbWO4
  specific = 4
FEATURE [App::DocumentObjectGroupPython] alactic  label="alactic : 1"  # scripted group (container) (typed FeaturePython)
  n = 1
  ref = alactic
FEATURE [App::DocumentObjectGroupPython] G4_Galactic  # scripted group (container) (typed FeaturePython)
  Dunit = g/cm3
  Dvalue = 0
  Group = -> [alactic]
  conduct = 2
  density = 1
  expand = 3
  formula = G4_Galactic
  name = G4_Galactic
  specific = 4
FEATURE [App::DocumentObjectGroupPython] RAPHITE_POROUS  label="RAPHITE_POROUS : 1"  # scripted group (container) (typed FeaturePython)
  n = 1
  ref = RAPHITE_POROUS
FEATURE [App::DocumentObjectGroupPython] G4_GRAPHITE_POROUS  # scripted group (container) (typed FeaturePython)
  Dunit = g/cm3
  Dvalue = 1.7
  Group = -> [RAPHITE_POROUS]
  conduct = 2
  density = 1
  expand = 3
  formula = G4_GRAPHITE_POROUS
  name = G4_GRAPHITE_POROUS
  specific = 4
FEATURE [App::DocumentObjectGroupPython] H_element115  label="H_element : 0.150"  # scripted group (container) (typed FeaturePython)
  n = 0.080538
FEATURE [App::DocumentObjectGroupPython] C_element125  label="C_element : 0.600"  # scripted group (container) (typed FeaturePython)
  n = 0.599848
FEATURE [App::DocumentObjectGroupPython] O_element108  label="O_element : 0.320"  # scripted group (container) (typed FeaturePython)
  n = 0.319614
FEATURE [App::DocumentObjectGroupPython] G4_LUCITE  # scripted group (container) (typed FeaturePython)
  Dunit = g/cm3
  Dvalue = 1.19
  Group = -> [H_element115,C_element125,O_element108]
  conduct = 2
  density = 1
  expand = 3
  formula = G4_LUCITE
  name = G4_LUCITE
  specific = 4
FEATURE [App::DocumentObjectGroupPython] Cu_element002  label="Cu_element : 62"  # scripted group (container) (typed FeaturePython)
  n = 62
  ref = Cu_element
FEATURE [App::DocumentObjectGroupPython] Zn_element002  label="Zn_element : 35"  # scripted group (container) (typed FeaturePython)
  n = 35
  ref = Zn_element
FEATURE [App::DocumentObjectGroupPython] Pb_element005  label="Pb_element : 3"  # scripted group (container) (typed FeaturePython)
  n = 3
  ref = Pb_element
FEATURE [App::DocumentObjectGroupPython] G4_BRASS  # scripted group (container) (typed FeaturePython)
  Dunit = g/cm3
  Dvalue = 8.52
  Group = -> [Cu_element002,Zn_element002,Pb_element005]
  conduct = 2
  density = 1
  expand = 3
  formula = G4_BRASS
  name = G4_BRASS
  specific = 4
FEATURE [App::DocumentObjectGroupPython] Cu_element003  label="Cu_element : 89"  # scripted group (container) (typed FeaturePython)
  n = 89
  ref = Cu_element
FEATURE [App::DocumentObjectGroupPython] Zn_element003  label="Zn_element : 9"  # scripted group (container) (typed FeaturePython)
  n = 9
  ref = Zn_element
FEATURE [App::DocumentObjectGroupPython] Pb_element006  label="Pb_element : 2"  # scripted group (container) (typed FeaturePython)
  n = 2
  ref = Pb_element
FEATURE [App::DocumentObjectGroupPython] G4_BRONZE  # scripted group (container) (typed FeaturePython)
  Dunit = g/cm3
  Dvalue = 8.82
  Group = -> [Cu_element003,Zn_element003,Pb_element006]
  conduct = 2
  density = 1
  expand = 3
  formula = G4_BRONZE
  name = G4_BRONZE
  specific = 4
FEATURE [App::DocumentObjectGroupPython] Fe_element008  label="Fe_element : 74"  # scripted group (container) (typed FeaturePython)
  n = 74
  ref = Fe_element
FEATURE [App::DocumentObjectGroupPython] Cr_element002  label="Cr_element : 18"  # scripted group (container) (typed FeaturePython)
  n = 18
  ref = Cr_element
FEATURE [App::DocumentObjectGroupPython] Ni_element002  label="Ni_element : 8"  # scripted group (container) (typed FeaturePython)
  n = 8
  ref = Ni_element
FEATURE [App::DocumentObjectGroupPython] G4_STAINLESS_STEEL  label="G4_STAINLESS-STEEL"  # scripted group (container) (typed FeaturePython)
  Dunit = g/cm3
  Dvalue = 8
  Group = -> [Fe_element008,Cr_element002,Ni_element002]
  conduct = 2
  density = 1
  expand = 3
  formula = G4_STAINLESS-STEEL
  name = G4_STAINLESS-STEEL
  specific = 4
FEATURE [App::DocumentObjectGroupPython] H_element116  label="H_element : 064"  # scripted group (container) (typed FeaturePython)
  n = 18
  ref = H_element
FEATURE [App::DocumentObjectGroupPython] C_element126  label="C_element : 071"  # scripted group (container) (typed FeaturePython)
  n = 12
  ref = C_element
FEATURE [App::DocumentObjectGroupPython] O_element109  label="O_element : 062"  # scripted group (container) (typed FeaturePython)
  n = 7
  ref = O_element
FEATURE [App::DocumentObjectGroupPython] G4_CR39  # scripted group (container) (typed FeaturePython)
  Dunit = g/cm3
  Dvalue = 1.32
  Group = -> [H_element116,C_element126,O_element109]
  conduct = 2
  density = 1
  expand = 3
  formula = G4_CR39
  name = G4_CR39
  specific = 4
FEATURE [App::DocumentObjectGroupPython] H_element117  label="H_element : 38"  # scripted group (container) (typed FeaturePython)
  n = 38
  ref = H_element
FEATURE [App::DocumentObjectGroupPython] C_element127  label="C_element : 072"  # scripted group (container) (typed FeaturePython)
  n = 18
  ref = C_element
FEATURE [App::DocumentObjectGroupPython] O_element110  label="O_element : 063"  # scripted group (container) (typed FeaturePython)
  n = 1
  ref = O_element
FEATURE [App::DocumentObjectGroupPython] G4_OCTADECANOL  # scripted group (container) (typed FeaturePython)
  Dunit = g/cm3
  Dvalue = 0.812
  Group = -> [H_element117,C_element127,O_element110]
  conduct = 2
  density = 1
  expand = 3
  formula = G4_OCTADECANOL
  name = G4_OCTADECANOL
  specific = 4
FEATURE [App::DocumentObjectGroupPython] HEP  # scripted group (container) (typed FeaturePython)
  Group = -> [G4_lH2,G4_lN2,G4_lO2,G4_lAr,G4_lBr,G4_lKr,G4_lXe,G4_PbWO4,G4_Galactic,G4_GRAPHITE_POROUS,G4_LUCITE,G4_BRASS,G4_BRONZE,G4_STAINLESS_STEEL,G4_CR39,G4_OCTADECANOL]
FEATURE [App::DocumentObjectGroupPython] C_element128  label="C_element : 073"  # scripted group (container) (typed FeaturePython)
  n = 14
  ref = C_element
FEATURE [App::DocumentObjectGroupPython] H_element118  label="H_element : 065"  # scripted group (container) (typed FeaturePython)
  n = 10
  ref = H_element
FEATURE [App::DocumentObjectGroupPython] O_element111  label="O_element : 064"  # scripted group (container) (typed FeaturePython)
  n = 2
  ref = O_element
FEATURE [App::DocumentObjectGroupPython] N_element050  label="N_element : 023"  # scripted group (container) (typed FeaturePython)
  n = 2
  ref = N_element
FEATURE [App::DocumentObjectGroupPython] G4_KEVLAR  # scripted group (container) (typed FeaturePython)
  Dunit = g/cm3
  Dvalue = 1.44
  Group = -> [C_element128,H_element118,O_element111,N_element050]
  conduct = 2
  density = 1
  expand = 3
  formula = G4_KEVLAR
  name = G4_KEVLAR
  specific = 4
FEATURE [App::DocumentObjectGroupPython] C_element129  label="C_element : 074"  # scripted group (container) (typed FeaturePython)
  n = 10
  ref = C_element
FEATURE [App::DocumentObjectGroupPython] H_element119  label="H_element : 066"  # scripted group (container) (typed FeaturePython)
  n = 8
  ref = H_element
FEATURE [App::DocumentObjectGroupPython] O_element112  label="O_element : 065"  # scripted group (container) (typed FeaturePython)
  n = 4
  ref = O_element
FEATURE [App::DocumentObjectGroupPython] G4_DACRON  # scripted group (container) (typed FeaturePython)
  Dunit = g/cm3
  Dvalue = 1.4
  Group = -> [C_element129,H_element119,O_element112]
  conduct = 2
  density = 1
  expand = 3
  formula = G4_DACRON
  name = G4_DACRON
  specific = 4
FEATURE [App::DocumentObjectGroupPython] C_element130  label="C_element : 075"  # scripted group (container) (typed FeaturePython)
  n = 4
  ref = C_element
FEATURE [App::DocumentObjectGroupPython] H_element120  label="H_element : 067"  # scripted group (container) (typed FeaturePython)
  n = 5
  ref = H_element
FEATURE [App::DocumentObjectGroupPython] Cl_element030  label="Cl_element : 016"  # scripted group (container) (typed FeaturePython)
  n = 1
  ref = Cl_element
FEATURE [App::DocumentObjectGroupPython] G4_NEOPRENE  # scripted group (container) (typed FeaturePython)
  Dunit = g/cm3
  Dvalue = 1.23
  Group = -> [C_element130,H_element120,Cl_element030]
  conduct = 2
  density = 1
  expand = 3
  formula = G4_NEOPRENE
  name = G4_NEOPRENE
  specific = 4
FEATURE [App::DocumentObjectGroupPython] Space  # scripted group (container) (typed FeaturePython)
  Group = -> [G4_KEVLAR,G4_DACRON,G4_NEOPRENE]
FEATURE [App::DocumentObjectGroupPython] H_element121  label="H_element : 068"  # scripted group (container) (typed FeaturePython)
  n = 5
  ref = H_element
FEATURE [App::DocumentObjectGroupPython] C_element131  label="C_element : 076"  # scripted group (container) (typed FeaturePython)
  n = 4
  ref = C_element
FEATURE [App::DocumentObjectGroupPython] N_element051  label="N_element : 3"  # scripted group (container) (typed FeaturePython)
  n = 3
  ref = N_element
FEATURE [App::DocumentObjectGroupPython] O_element113  label="O_element : 066"  # scripted group (container) (typed FeaturePython)
  n = 1
  ref = O_element
FEATURE [App::DocumentObjectGroupPython] G4_CYTOSINE  # scripted group (container) (typed FeaturePython)
  Dunit = g/cm3
  Dvalue = 1.55
  Group = -> [H_element121,C_element131,N_element051,O_element113]
  conduct = 2
  density = 1
  expand = 3
  formula = G4_CYTOSINE
  name = G4_CYTOSINE
  specific = 4
FEATURE [App::DocumentObjectGroupPython] H_element122  label="H_element : 069"  # scripted group (container) (typed FeaturePython)
  n = 6
  ref = H_element
FEATURE [App::DocumentObjectGroupPython] C_element132  label="C_element : 077"  # scripted group (container) (typed FeaturePython)
  n = 5
  ref = C_element
FEATURE [App::DocumentObjectGroupPython] N_element052  label="N_element : 024"  # scripted group (container) (typed FeaturePython)
  n = 2
  ref = N_element
FEATURE [App::DocumentObjectGroupPython] O_element114  label="O_element : 067"  # scripted group (container) (typed FeaturePython)
  n = 2
  ref = O_element
FEATURE [App::DocumentObjectGroupPython] G4_THYMINE  # scripted group (container) (typed FeaturePython)
  Dunit = g/cm3
  Dvalue = 1.23
  Group = -> [H_element122,C_element132,N_element052,O_element114]
  conduct = 2
  density = 1
  expand = 3
  formula = G4_THYMINE
  name = G4_THYMINE
  specific = 4
FEATURE [App::DocumentObjectGroupPython] H_element123  label="H_element : 070"  # scripted group (container) (typed FeaturePython)
  n = 4
  ref = H_element
FEATURE [App::DocumentObjectGroupPython] C_element133  label="C_element : 078"  # scripted group (container) (typed FeaturePython)
  n = 4
  ref = C_element
FEATURE [App::DocumentObjectGroupPython] N_element053  label="N_element : 025"  # scripted group (container) (typed FeaturePython)
  n = 2
  ref = N_element
FEATURE [App::DocumentObjectGroupPython] O_element115  label="O_element : 068"  # scripted group (container) (typed FeaturePython)
  n = 2
  ref = O_element
FEATURE [App::DocumentObjectGroupPython] G4_URACIL  # scripted group (container) (typed FeaturePython)
  Dunit = g/cm3
  Dvalue = 1.32
  Group = -> [H_element123,C_element133,N_element053,O_element115]
  conduct = 2
  density = 1
  expand = 3
  formula = G4_URACIL
  name = G4_URACIL
  specific = 4
FEATURE [App::DocumentObjectGroupPython] H_element124  label="H_element : 071"  # scripted group (container) (typed FeaturePython)
  n = 4
  ref = H_element
FEATURE [App::DocumentObjectGroupPython] C_element134  label="C_element : 079"  # scripted group (container) (typed FeaturePython)
  n = 5
  ref = C_element
FEATURE [App::DocumentObjectGroupPython] N_element054  label="N_element : 026"  # scripted group (container) (typed FeaturePython)
  n = 5
  ref = N_element
FEATURE [App::DocumentObjectGroupPython] G4_DNA_ADENINE  # scripted group (container) (typed FeaturePython)
  Dunit = g/cm3
  Dvalue = 1
  Group = -> [H_element124,C_element134,N_element054]
  conduct = 2
  density = 1
  expand = 3
  formula = G4_DNA_ADENINE
  name = G4_DNA_ADENINE
  specific = 4
FEATURE [App::DocumentObjectGroupPython] H_element125  label="H_element : 072"  # scripted group (container) (typed FeaturePython)
  n = 4
  ref = H_element
FEATURE [App::DocumentObjectGroupPython] C_element135  label="C_element : 080"  # scripted group (container) (typed FeaturePython)
  n = 5
  ref = C_element
FEATURE [App::DocumentObjectGroupPython] N_element055  label="N_element : 027"  # scripted group (container) (typed FeaturePython)
  n = 5
  ref = N_element
FEATURE [App::DocumentObjectGroupPython] O_element116  label="O_element : 069"  # scripted group (container) (typed FeaturePython)
  n = 1
  ref = O_element
FEATURE [App::DocumentObjectGroupPython] G4_DNA_GUANINE  # scripted group (container) (typed FeaturePython)
  Dunit = g/cm3
  Dvalue = 1
  Group = -> [H_element125,C_element135,N_element055,O_element116]
  conduct = 2
  density = 1
  expand = 3
  formula = G4_DNA_GUANINE
  name = G4_DNA_GUANINE
  specific = 4
FEATURE [App::DocumentObjectGroupPython] H_element126  label="H_element : 073"  # scripted group (container) (typed FeaturePython)
  n = 4
  ref = H_element
FEATURE [App::DocumentObjectGroupPython] C_element136  label="C_element : 081"  # scripted group (container) (typed FeaturePython)
  n = 4
  ref = C_element
FEATURE [App::DocumentObjectGroupPython] N_element056  label="N_element : 028"  # scripted group (container) (typed FeaturePython)
  n = 3
  ref = N_element
FEATURE [App::DocumentObjectGroupPython] O_element117  label="O_element : 070"  # scripted group (container) (typed FeaturePython)
  n = 1
  ref = O_element
FEATURE [App::DocumentObjectGroupPython] G4_DNA_CYTOSINE  # scripted group (container) (typed FeaturePython)
  Dunit = g/cm3
  Dvalue = 1
  Group = -> [H_element126,C_element136,N_element056,O_element117]
  conduct = 2
  density = 1
  expand = 3
  formula = G4_DNA_CYTOSINE
  name = G4_DNA_CYTOSINE
  specific = 4
FEATURE [App::DocumentObjectGroupPython] H_element127  label="H_element : 074"  # scripted group (container) (typed FeaturePython)
  n = 5
  ref = H_element
FEATURE [App::DocumentObjectGroupPython] C_element137  label="C_element : 082"  # scripted group (container) (typed FeaturePython)
  n = 5
  ref = C_element
FEATURE [App::DocumentObjectGroupPython] N_element057  label="N_element : 029"  # scripted group (container) (typed FeaturePython)
  n = 2
  ref = N_element
FEATURE [App::DocumentObjectGroupPython] O_element118  label="O_element : 071"  # scripted group (container) (typed FeaturePython)
  n = 2
  ref = O_element
FEATURE [App::DocumentObjectGroupPython] G4_DNA_THYMINE  # scripted group (container) (typed FeaturePython)
  Dunit = g/cm3
  Dvalue = 1
  Group = -> [H_element127,C_element137,N_element057,O_element118]
  conduct = 2
  density = 1
  expand = 3
  formula = G4_DNA_THYMINE
  name = G4_DNA_THYMINE
  specific = 4
FEATURE [App::DocumentObjectGroupPython] H_element128  label="H_element : 075"  # scripted group (container) (typed FeaturePython)
  n = 3
  ref = H_element
FEATURE [App::DocumentObjectGroupPython] C_element138  label="C_element : 083"  # scripted group (container) (typed FeaturePython)
  n = 4
  ref = C_element
FEATURE [App::DocumentObjectGroupPython] N_element058  label="N_element : 030"  # scripted group (container) (typed FeaturePython)
  n = 2
  ref = N_element
FEATURE [App::DocumentObjectGroupPython] O_element119  label="O_element : 072"  # scripted group (container) (typed FeaturePython)
  n = 2
  ref = O_element
FEATURE [App::DocumentObjectGroupPython] G4_DNA_URACIL  # scripted group (container) (typed FeaturePython)
  Dunit = g/cm3
  Dvalue = 1
  Group = -> [H_element128,C_element138,N_element058,O_element119]
  conduct = 2
  density = 1
  expand = 3
  formula = G4_DNA_URACIL
  name = G4_DNA_URACIL
  specific = 4
FEATURE [App::DocumentObjectGroupPython] H_element129  label="H_element : 076"  # scripted group (container) (typed FeaturePython)
  n = 10
  ref = H_element
FEATURE [App::DocumentObjectGroupPython] C_element139  label="C_element : 084"  # scripted group (container) (typed FeaturePython)
  n = 10
  ref = C_element
FEATURE [App::DocumentObjectGroupPython] N_element059  label="N_element : 031"  # scripted group (container) (typed FeaturePython)
  n = 5
  ref = N_element
FEATURE [App::DocumentObjectGroupPython] O_element120  label="O_element : 073"  # scripted group (container) (typed FeaturePython)
  n = 4
  ref = O_element
FEATURE [App::DocumentObjectGroupPython] G4_DNA_ADENOSINE  # scripted group (container) (typed FeaturePython)
  Dunit = g/cm3
  Dvalue = 1
  Group = -> [H_element129,C_element139,N_element059,O_element120]
  conduct = 2
  density = 1
  expand = 3
  formula = G4_DNA_ADENOSINE
  name = G4_DNA_ADENOSINE
  specific = 4
FEATURE [App::DocumentObjectGroupPython] H_element130  label="H_element : 077"  # scripted group (container) (typed FeaturePython)
  n = 10
  ref = H_element
FEATURE [App::DocumentObjectGroupPython] C_element140  label="C_element : 085"  # scripted group (container) (typed FeaturePython)
  n = 10
  ref = C_element
FEATURE [App::DocumentObjectGroupPython] N_element060  label="N_element : 032"  # scripted group (container) (typed FeaturePython)
  n = 5
  ref = N_element
FEATURE [App::DocumentObjectGroupPython] O_element121  label="O_element : 074"  # scripted group (container) (typed FeaturePython)
  n = 5
  ref = O_element
FEATURE [App::DocumentObjectGroupPython] G4_DNA_GUANOSINE  # scripted group (container) (typed FeaturePython)
  Dunit = g/cm3
  Dvalue = 1
  Group = -> [H_element130,C_element140,N_element060,O_element121]
  conduct = 2
  density = 1
  expand = 3
  formula = G4_DNA_GUANOSINE
  name = G4_DNA_GUANOSINE
  specific = 4
FEATURE [App::DocumentObjectGroupPython] H_element131  label="H_element : 078"  # scripted group (container) (typed FeaturePython)
  n = 10
  ref = H_element
FEATURE [App::DocumentObjectGroupPython] C_element141  label="C_element : 086"  # scripted group (container) (typed FeaturePython)
  n = 9
  ref = C_element
FEATURE [App::DocumentObjectGroupPython] N_element061  label="N_element : 033"  # scripted group (container) (typed FeaturePython)
  n = 3
  ref = N_element
FEATURE [App::DocumentObjectGroupPython] O_element122  label="O_element : 075"  # scripted group (container) (typed FeaturePython)
  n = 5
  ref = O_element
FEATURE [App::DocumentObjectGroupPython] G4_DNA_CYTIDINE  # scripted group (container) (typed FeaturePython)
  Dunit = g/cm3
  Dvalue = 1
  Group = -> [H_element131,C_element141,N_element061,O_element122]
  conduct = 2
  density = 1
  expand = 3
  formula = G4_DNA_CYTIDINE
  name = G4_DNA_CYTIDINE
  specific = 4
FEATURE [App::DocumentObjectGroupPython] H_element132  label="H_element : 079"  # scripted group (container) (typed FeaturePython)
  n = 9
  ref = H_element
FEATURE [App::DocumentObjectGroupPython] C_element142  label="C_element : 087"  # scripted group (container) (typed FeaturePython)
  n = 9
  ref = C_element
FEATURE [App::DocumentObjectGroupPython] N_element062  label="N_element : 034"  # scripted group (container) (typed FeaturePython)
  n = 2
  ref = N_element
FEATURE [App::DocumentObjectGroupPython] O_element123  label="O_element : 076"  # scripted group (container) (typed FeaturePython)
  n = 6
  ref = O_element
FEATURE [App::DocumentObjectGroupPython] G4_DNA_URIDINE  # scripted group (container) (typed FeaturePython)
  Dunit = g/cm3
  Dvalue = 1
  Group = -> [H_element132,C_element142,N_element062,O_element123]
  conduct = 2
  density = 1
  expand = 3
  formula = G4_DNA_URIDINE
  name = G4_DNA_URIDINE
  specific = 4
FEATURE [App::DocumentObjectGroupPython] H_element133  label="H_element : 080"  # scripted group (container) (typed FeaturePython)
  n = 11
  ref = H_element
FEATURE [App::DocumentObjectGroupPython] C_element143  label="C_element : 088"  # scripted group (container) (typed FeaturePython)
  n = 10
  ref = C_element
FEATURE [App::DocumentObjectGroupPython] N_element063  label="N_element : 035"  # scripted group (container) (typed FeaturePython)
  n = 2
  ref = N_element
FEATURE [App::DocumentObjectGroupPython] O_element124  label="O_element : 077"  # scripted group (container) (typed FeaturePython)
  n = 6
  ref = O_element
FEATURE [App::DocumentObjectGroupPython] G4_DNA_METHYLURIDINE  # scripted group (container) (typed FeaturePython)
  Dunit = g/cm3
  Dvalue = 1
  Group = -> [H_element133,C_element143,N_element063,O_element124]
  conduct = 2
  density = 1
  expand = 3
  formula = G4_DNA_METHYLURIDINE
  name = G4_DNA_METHYLURIDINE
  specific = 4
FEATURE [App::DocumentObjectGroupPython] P_element014  label="P_element : 003"  # scripted group (container) (typed FeaturePython)
  n = 1
  ref = P_element
FEATURE [App::DocumentObjectGroupPython] O_element125  label="O_element : 078"  # scripted group (container) (typed FeaturePython)
  n = 3
  ref = O_element
FEATURE [App::DocumentObjectGroupPython] G4_DNA_MONOPHOSPHATE  # scripted group (container) (typed FeaturePython)
  Dunit = g/cm3
  Dvalue = 1
  Group = -> [P_element014,O_element125]
  conduct = 2
  density = 1
  expand = 3
  formula = G4_DNA_MONOPHOSPHATE
  name = G4_DNA_MONOPHOSPHATE
  specific = 4
FEATURE [App::DocumentObjectGroupPython] H_element134  label="H_element : 081"  # scripted group (container) (typed FeaturePython)
  n = 10
  ref = H_element
FEATURE [App::DocumentObjectGroupPython] C_element144  label="C_element : 089"  # scripted group (container) (typed FeaturePython)
  n = 10
  ref = C_element
FEATURE [App::DocumentObjectGroupPython] N_element064  label="N_element : 036"  # scripted group (container) (typed FeaturePython)
  n = 5
  ref = N_element
FEATURE [App::DocumentObjectGroupPython] O_element126  label="O_element : 079"  # scripted group (container) (typed FeaturePython)
  n = 7
  ref = O_element
FEATURE [App::DocumentObjectGroupPython] P_element015  label="P_element : 004"  # scripted group (container) (typed FeaturePython)
  n = 1
  ref = P_element
FEATURE [App::DocumentObjectGroupPython] G4_DNA_A  # scripted group (container) (typed FeaturePython)
  Dunit = g/cm3
  Dvalue = 1
  Group = -> [H_element134,C_element144,N_element064,O_element126,P_element015]
  conduct = 2
  density = 1
  expand = 3
  formula = G4_DNA_A
  name = G4_DNA_A
  specific = 4
FEATURE [App::DocumentObjectGroupPython] H_element135  label="H_element : 082"  # scripted group (container) (typed FeaturePython)
  n = 10
  ref = H_element
FEATURE [App::DocumentObjectGroupPython] C_element145  label="C_element : 090"  # scripted group (container) (typed FeaturePython)
  n = 10
  ref = C_element
FEATURE [App::DocumentObjectGroupPython] N_element065  label="N_element : 037"  # scripted group (container) (typed FeaturePython)
  n = 5
  ref = N_element
FEATURE [App::DocumentObjectGroupPython] O_element127  label="O_element : 8"  # scripted group (container) (typed FeaturePython)
  n = 8
  ref = O_element
FEATURE [App::DocumentObjectGroupPython] P_element016  label="P_element : 005"  # scripted group (container) (typed FeaturePython)
  n = 1
  ref = P_element
FEATURE [App::DocumentObjectGroupPython] G4_DNA_G  # scripted group (container) (typed FeaturePython)
  Dunit = g/cm3
  Dvalue = 1
  Group = -> [H_element135,C_element145,N_element065,O_element127,P_element016]
  conduct = 2
  density = 1
  expand = 3
  formula = G4_DNA_G
  name = G4_DNA_G
  specific = 4
FEATURE [App::DocumentObjectGroupPython] H_element136  label="H_element : 083"  # scripted group (container) (typed FeaturePython)
  n = 10
  ref = H_element
FEATURE [App::DocumentObjectGroupPython] C_element146  label="C_element : 091"  # scripted group (container) (typed FeaturePython)
  n = 9
  ref = C_element
FEATURE [App::DocumentObjectGroupPython] N_element066  label="N_element : 038"  # scripted group (container) (typed FeaturePython)
  n = 3
  ref = N_element
FEATURE [App::DocumentObjectGroupPython] O_element128  label="O_element : 080"  # scripted group (container) (typed FeaturePython)
  n = 8
  ref = O_element
FEATURE [App::DocumentObjectGroupPython] P_element017  label="P_element : 006"  # scripted group (container) (typed FeaturePython)
  n = 1
  ref = P_element
FEATURE [App::DocumentObjectGroupPython] G4_DNA_C  # scripted group (container) (typed FeaturePython)
  Dunit = g/cm3
  Dvalue = 1
  Group = -> [H_element136,C_element146,N_element066,O_element128,P_element017]
  conduct = 2
  density = 1
  expand = 3
  formula = G4_DNA_C
  name = G4_DNA_C
  specific = 4
FEATURE [App::DocumentObjectGroupPython] H_element137  label="H_element : 084"  # scripted group (container) (typed FeaturePython)
  n = 9
  ref = H_element
FEATURE [App::DocumentObjectGroupPython] C_element147  label="C_element : 092"  # scripted group (container) (typed FeaturePython)
  n = 9
  ref = C_element
FEATURE [App::DocumentObjectGroupPython] N_element067  label="N_element : 039"  # scripted group (container) (typed FeaturePython)
  n = 2
  ref = N_element
FEATURE [App::DocumentObjectGroupPython] O_element129  label="O_element : 9"  # scripted group (container) (typed FeaturePython)
  n = 9
  ref = O_element
FEATURE [App::DocumentObjectGroupPython] P_element018  label="P_element : 007"  # scripted group (container) (typed FeaturePython)
  n = 1
  ref = P_element
FEATURE [App::DocumentObjectGroupPython] G4_DNA_U  # scripted group (container) (typed FeaturePython)
  Dunit = g/cm3
  Dvalue = 1
  Group = -> [H_element137,C_element147,N_element067,O_element129,P_element018]
  conduct = 2
  density = 1
  expand = 3
  formula = G4_DNA_U
  name = G4_DNA_U
  specific = 4
FEATURE [App::DocumentObjectGroupPython] H_element138  label="H_element : 085"  # scripted group (container) (typed FeaturePython)
  n = 11
  ref = H_element
FEATURE [App::DocumentObjectGroupPython] C_element148  label="C_element : 093"  # scripted group (container) (typed FeaturePython)
  n = 10
  ref = C_element
FEATURE [App::DocumentObjectGroupPython] N_element068  label="N_element : 040"  # scripted group (container) (typed FeaturePython)
  n = 2
  ref = N_element
FEATURE [App::DocumentObjectGroupPython] O_element130  label="O_element : 081"  # scripted group (container) (typed FeaturePython)
  n = 9
  ref = O_element
FEATURE [App::DocumentObjectGroupPython] P_element019  label="P_element : 008"  # scripted group (container) (typed FeaturePython)
  n = 1
  ref = P_element
FEATURE [App::DocumentObjectGroupPython] G4_DNA_MU  # scripted group (container) (typed FeaturePython)
  Dunit = g/cm3
  Dvalue = 1
  Group = -> [H_element138,C_element148,N_element068,O_element130,P_element019]
  conduct = 2
  density = 1
  expand = 3
  formula = G4_DNA_MU
  name = G4_DNA_MU
  specific = 4
FEATURE [App::DocumentObjectGroupPython] BioChemical  # scripted group (container) (typed FeaturePython)
  Group = -> [G4_CYTOSINE,G4_THYMINE,G4_URACIL,G4_DNA_ADENINE,G4_DNA_GUANINE,G4_DNA_CYTOSINE,G4_DNA_THYMINE,G4_DNA_URACIL,G4_DNA_ADENOSINE,G4_DNA_GUANOSINE,G4_DNA_CYTIDINE,G4_DNA_URIDINE,G4_DNA_METHYLURIDINE,G4_DNA_MONOPHOSPHATE,G4_DNA_A,G4_DNA_G,G4_DNA_C,G4_DNA_U,G4_DNA_MU]
FEATURE [App::DocumentObjectGroupPython] G4Materials  # scripted group (container) (typed FeaturePython)
  Group = -> [NIST,Element,HEP,Space,BioChemical]
  version = 1
FEATURE [App::DocumentObjectGroupPython] Geant4  # scripted group (container) (typed FeaturePython)
  Group = -> [G4Isotopes,G4Elements,G4Materials]
FEATURE [App::DocumentObjectGroupPython] Materials  # scripted group (container) (typed FeaturePython)
  Group = -> [Geant4]
FEATURE [Part::FeaturePython] GDMLBox_WorldBox  # WARN: FeaturePython — macro-defined, semantics opaque (R4)
  lunit = 2
  material = 5
  x = 273
  y = 273
  z = 130
FEATURE [Part::FeaturePython] GDMLBox_Box  # WARN: FeaturePython — macro-defined, semantics opaque (R4)
  Placement = pos=(20,0,0) rot=(0,0,1;0rad)
  lunit = 2
  material = 0
  x = 10
  y = 10
  z = 10
FEATURE [App::Part] LV_Box
  Group = -> [GDMLBox_Box]
  Origin = -> Origin002
FEATURE [Part::FeaturePython] Array  # Draft array (typed FeaturePython)
  AlwaysSyncPlacement = false
  Angle = 180
  ArrayType = 1
  Axis = (0,0,1)
  Base = -> LV_Box
  Center = (0,0,0)
  Count = 5
  ExpandArray = false
  Fuse = false
  IntervalAxis = (0,0,0)
  IntervalX = (100,0,0)
  IntervalY = (0,100,0)
  IntervalZ = (0,0,100)
  NumberCircles = 3
  NumberPolar = 5
  NumberX = 2
  NumberY = 2
  NumberZ = 1
  PlacementList = 5 placements: [(0,0,0),(0,0,0),(0,0,0),(0,0,0),(0,0,0)]
  RadialDistance = 50
  ScaleList = (5) [(1,1,1),(1,1,1),(1,1,1),(1,1,1),(1,1,1)]
  Symmetry = 1
  TangentialDistance = 25
FEATURE [App::Part] Part  label="experiment"
  Group = -> [LV_Box,Array]
  Origin = -> Origin001
FEATURE [App::Part] worldVOL
  Group = -> [GDMLBox_WorldBox,Part]
  Origin = -> Origin
